# Revit family: ADSK_Балка_Двутавр_ГОСТ Р 57837-2017
name_source: partatom
category: Каркас несущий
units: mm (PartAtom-declared; Revit-internal decimal feet)

## family parameters
Всегда вертикально = Да
Всегда экспортировать в виде геометрии = Нет
Материал для поведения модели = Сталь
Общий = Нет
Округление длины несущего каркаса = 0 мм
Показывать семейство разрезанным на планах = Да
При загрузке вырезать с полостями = Нет
Условное обозначение = Из настроек проекта
Форма сечения = Двутавровая параллельная полка

## types (340) — shared parameters
ADSK_Версия Revit = v2019
ADSK_Версия семейства = 1.3
ADSK_Высота строки_Изображение = 8 мм.png
ADSK_Группа конструкций = 1
ADSK_Деталь наоборот = Нет
ADSK_Наименование профиля = Двутавры стальные горячекатаные с параллельными гранями полок
ADSK_Наименование_Текст1 = Двутавр
ADSK_НаименованиеСоставное_Префикс = <unrecoverable-encoding: 3 bytes ee9ca9>
ADSK_Обозначение = ГОСТ Р 57837-2017
ADSK_Тип элемента КМ = 2
ТВ = Двутавр_ГОСТ Р 57837-2017

## per-type parameters (varying)
- 10Б1: ADSK_Масса на единицу длины=8.10 кг/м; Ix=171.01 см4; Iy=15.92 см4; Sx=19.7 см³; Sy=4.6 см³; Wx=34.2 см³; Wy=5.8 см³; b=55.00 мм; h=100.00 мм; ix=40.70 мм; iy=12.42 мм; r=7.00 мм; s=4.10 мм; t=5.70 мм; Вертикальный центроид=50.00 мм; Высота=100.00 мм; Горизонтальный центроид=27.50 мм; Номинальный вес=8.10 килограмм-сила/м; Носок полки сопряжения=9.05 мм; Носок ребра жесткости сопряжения=12.70 мм; Площадь сечения=10.3 см²; Сопряжение ребра жесткости=7.00 мм; Толщина полки=5.70 мм; Толщина ребра жесткости=4.10 мм; Чистая высота ребра жесткости=88.60 мм; Ширина=55.00 мм
- 12Б1: ADSK_Масса на единицу длины=8.70 кг/м; Ix=257.36 см4; Iy=22.39 см4; Sx=24.9 см³; Sy=5.5 см³; Wx=43.8 см³; Wy=7.0 см³; b=64.00 мм; h=117.60 мм; ix=48.30 мм; iy=14.25 мм; r=7.00 мм; s=3.80 мм; t=5.10 мм; Вертикальный центроид=58.80 мм; Высота=117.60 мм; Горизонтальный центроид=32.00 мм; Номинальный вес=8.70 килограмм-сила/м; Носок полки сопряжения=8.90 мм; Носок ребра жесткости сопряжения=12.10 мм; Площадь сечения=11.0 см²; Сопряжение ребра жесткости=7.00 мм; Толщина полки=5.10 мм; Толщина ребра жесткости=3.80 мм; Чистая высота ребра жесткости=107.40 мм; Ширина=64.00 мм
- 12Б2: ADSK_Масса на единицу длины=10.40 кг/м; Ix=317.75 см4; Iy=27.67 см4; Sx=30.4 см³; Sy=6.8 см³; Wx=53.0 см³; Wy=8.7 см³; b=64.00 мм; h=120.00 мм; ix=49.04 мм; iy=14.47 мм; r=7.00 мм; s=4.40 мм; t=6.30 мм; Вертикальный центроид=60.00 мм; Высота=120.00 мм; Горизонтальный центроид=32.00 мм; Номинальный вес=10.40 килограмм-сила/м; Носок полки сопряжения=9.20 мм; Носок ребра жесткости сопряжения=13.30 мм; Площадь сечения=13.2 см²; Сопряжение ребра жесткости=7.00 мм; Толщина полки=6.30 мм; Толщина ребра жесткости=4.40 мм; Чистая высота ребра жесткости=107.40 мм; Ширина=64.00 мм
- 14Б1: ADSK_Масса на единицу длины=10.50 кг/м; Ix=434.86 см4; Iy=36.42 см4; Sx=35.8 см³; Sy=7.8 см³; Wx=63.3 см³; Wy=10.0 см³; b=73.00 мм; h=137.40 мм; ix=56.98 мм; iy=16.49 мм; r=7.00 мм; s=3.80 мм; t=5.60 мм; Вертикальный центроид=68.70 мм; Высота=137.40 мм; Горизонтальный центроид=36.50 мм; Номинальный вес=10.50 килограмм-сила/м; Носок полки сопряжения=8.90 мм; Носок ребра жесткости сопряжения=12.60 мм; Площадь сечения=13.4 см²; Сопряжение ребра жесткости=7.00 мм; Толщина полки=5.60 мм; Толщина ребра жесткости=3.80 мм; Чистая высота ребра жесткости=126.20 мм; Ширина=73.00 мм
- 14Б2: ADSK_Масса на единицу длины=12.90 кг/м; Ix=541.22 см4; Iy=44.92 см4; Sx=44.2 см³; Sy=9.6 см³; Wx=77.3 см³; Wy=12.3 см³; b=73.00 мм; h=140.00 мм; ix=57.40 мм; iy=16.54 мм; r=7.00 мм; s=4.70 мм; t=6.90 мм; Вертикальный центроид=70.00 мм; Высота=140.00 мм; Горизонтальный центроид=36.50 мм; Номинальный вес=12.90 килограмм-сила/м; Носок полки сопряжения=9.35 мм; Носок ребра жесткости сопряжения=13.90 мм; Площадь сечения=16.4 см²; Сопряжение ребра жесткости=7.00 мм; Толщина полки=6.90 мм; Толщина ребра жесткости=4.70 мм; Чистая высота ребра жесткости=126.20 мм; Ширина=73.00 мм
- 16Б1: ADSK_Масса на единицу длины=12.70 кг/м; Ix=689.28 см4; Iy=54.43 см4; Sx=49.6 см³; Sy=10.4 см³; Wx=87.8 см³; Wy=13.3 см³; b=82.00 мм; h=157.00 мм; ix=65.27 мм; iy=18.34 мм; r=9.00 мм; s=4.00 мм; t=5.90 мм; Вертикальный центроид=78.50 мм; Высота=157.00 мм; Горизонтальный центроид=41.00 мм; Номинальный вес=12.70 килограмм-сила/м; Носок полки сопряжения=11.00 мм; Носок ребра жесткости сопряжения=14.90 мм; Площадь сечения=16.2 см²; Сопряжение ребра жесткости=9.00 мм; Толщина полки=5.90 мм; Толщина ребра жесткости=4.00 мм; Чистая высота ребра жесткости=145.20 мм; Ширина=82.00 мм
- 16Б2: ADSK_Масса на единицу длины=15.80 кг/м; Ix=869.29 см4; Iy=68.31 см4; Sx=61.9 см³; Sy=13.1 см³; Wx=108.7 см³; Wy=16.7 см³; b=82.00 мм; h=160.00 мм; ix=65.78 мм; iy=18.44 мм; r=9.00 мм; s=5.00 мм; t=7.40 мм; Вертикальный центроид=80.00 мм; Высота=160.00 мм; Горизонтальный центроид=41.00 мм; Номинальный вес=15.80 килограмм-сила/м; Носок полки сопряжения=11.50 мм; Носок ребра жесткости сопряжения=16.40 мм; Площадь сечения=20.1 см²; Сопряжение ребра жесткости=9.00 мм; Толщина полки=7.40 мм; Толщина ребра жесткости=5.00 мм; Чистая высота ребра жесткости=145.20 мм; Ширина=82.00 мм
- 18Б1: ADSK_Масса на единицу длины=15.40 кг/м; Ix=1062.74 см4; Iy=81.89 см4; Sx=67.7 см³; Sy=14.0 см³; Wx=120.1 см³; Wy=18.0 см³; b=91.00 мм; h=177.00 мм; ix=73.68 мм; iy=20.45 мм; r=9.00 мм; s=4.30 мм; t=6.50 мм; Вертикальный центроид=88.50 мм; Высота=177.00 мм; Горизонтальный центроид=45.50 мм; Номинальный вес=15.40 килограмм-сила/м; Носок полки сопряжения=11.15 мм; Носок ребра жесткости сопряжения=15.50 мм; Площадь сечения=19.6 см²; Сопряжение ребра жесткости=9.00 мм; Толщина полки=6.50 мм; Толщина ребра жесткости=4.30 мм; Чистая высота ребра жесткости=164.00 мм; Ширина=91.00 мм
- 18Б2: ADSK_Масса на единицу длины=18.80 кг/м; Ix=1316.96 см4; Iy=100.85 см4; Sx=83.2 см³; Sy=17.3 см³; Wx=146.3 см³; Wy=22.2 см³; b=91.00 мм; h=180.00 мм; ix=74.16 мм; iy=20.52 мм; r=9.00 мм; s=5.30 мм; t=8.00 мм; Вертикальный центроид=90.00 мм; Высота=180.00 мм; Горизонтальный центроид=45.50 мм; Номинальный вес=18.80 килограмм-сила/м; Носок полки сопряжения=11.65 мм; Носок ребра жесткости сопряжения=17.00 мм; Площадь сечения=24.0 см²; Сопряжение ребра жесткости=9.00 мм; Толщина полки=8.00 мм; Толщина ребра жесткости=5.30 мм; Чистая высота ребра жесткости=164.00 мм; Ширина=91.00 мм
- 20Б1: ADSK_Масса на единицу длины=21.30 кг/м; Ix=1844.26 см4; Iy=133.91 см4; Sx=104.7 см³; Sy=21.0 см³; Wx=184.4 см³; Wy=26.8 см³; b=100.00 мм; h=200.00 мм; ix=82.41 мм; iy=22.21 мм; r=11.00 мм; s=5.50 мм; t=8.00 мм; Вертикальный центроид=100.00 мм; Высота=200.00 мм; Горизонтальный центроид=50.00 мм; Номинальный вес=21.30 килограмм-сила/м; Носок полки сопряжения=13.75 мм; Носок ребра жесткости сопряжения=19.00 мм; Площадь сечения=27.2 см²; Сопряжение ребра жесткости=11.00 мм; Толщина полки=8.00 мм; Толщина ребра жесткости=5.50 мм; Чистая высота ребра жесткости=184.00 мм; Ширина=100.00 мм
- 20Б2: ADSK_Масса на единицу длины=25.30 кг/м; Ix=2218.49 см4; Iy=163.93 см4; Sx=125.0 см³; Sy=25.5 см³; Wx=218.6 см³; Wy=32.5 см³; b=101.00 мм; h=203.00 мм; ix=83.02 мм; iy=22.57 мм; r=11.00 мм; s=6.50 мм; t=9.50 мм; Вертикальный центроид=101.50 мм; Высота=203.00 мм; Горизонтальный центроид=50.50 мм; Номинальный вес=25.30 килограмм-сила/м; Носок полки сопряжения=14.25 мм; Носок ребра жесткости сопряжения=20.50 мм; Площадь сечения=32.2 см²; Сопряжение ребра жесткости=11.00 мм; Толщина полки=9.50 мм; Толщина ребра жесткости=6.50 мм; Чистая высота ребра жесткости=184.00 мм; Ширина=101.00 мм
- 20Б3: ADSK_Масса на единицу длины=31.60 кг/м; Ix=2852.62 см4; Iy=213.50 см4; Sx=158.5 см³; Sy=33.0 см³; Wx=274.3 см³; Wy=41.9 см³; b=102.00 мм; h=208.00 мм; ix=84.20 мм; iy=23.03 мм; r=11.00 мм; s=8.00 мм; t=12.00 мм; Вертикальный центроид=104.00 мм; Высота=208.00 мм; Горизонтальный центроид=51.00 мм; Номинальный вес=31.60 килограмм-сила/м; Носок полки сопряжения=15.00 мм; Носок ребра жесткости сопряжения=23.00 мм; Площадь сечения=40.2 см²; Сопряжение ребра жесткости=11.00 мм; Толщина полки=12.00 мм; Толщина ребра жесткости=8.00 мм; Чистая высота ребра жесткости=184.00 мм; Ширина=102.00 мм
- 25Б1: ADSK_Масса на единицу длины=25.70 кг/м; Ix=3537.11 см4; Iy=254.85 см4; Sx=159.7 см³; Sy=31.8 см³; Wx=285.3 см³; Wy=41.1 см³; b=124.00 мм; h=248.00 мм; ix=104.04 мм; iy=27.93 мм; r=12.00 мм; s=5.00 мм; t=8.00 мм; Вертикальный центроид=124.00 мм; Высота=248.00 мм; Горизонтальный центроид=62.00 мм; Номинальный вес=25.70 килограмм-сила/м; Носок полки сопряжения=14.50 мм; Носок ребра жесткости сопряжения=20.00 мм; Площадь сечения=32.7 см²; Сопряжение ребра жесткости=12.00 мм; Толщина полки=8.00 мм; Толщина ребра жесткости=5.00 мм; Чистая высота ребра жесткости=232.00 мм; Ширина=124.00 мм
- 25Б2: ADSK_Масса на единицу длины=29.60 кг/м; Ix=4051.73 см4; Iy=293.85 см4; Sx=182.9 см³; Sy=36.6 см³; Wx=324.1 см³; Wy=47.0 см³; b=125.00 мм; h=250.00 мм; ix=103.73 мм; iy=27.93 мм; r=12.00 мм; s=6.00 мм; t=9.00 мм; Вертикальный центроид=125.00 мм; Высота=250.00 мм; Горизонтальный центроид=62.50 мм; Номинальный вес=29.60 килограмм-сила/м; Носок полки сопряжения=15.00 мм; Носок ребра жесткости сопряжения=21.00 мм; Площадь сечения=37.7 см²; Сопряжение ребра жесткости=12.00 мм; Толщина полки=9.00 мм; Толщина ребра жесткости=6.00 мм; Чистая высота ребра жесткости=232.00 мм; Ширина=125.00 мм
- 25Б3: ADSK_Масса на единицу длины=37.40 кг/м; Ix=5238.16 см4; Iy=384.79 см4; Sx=233.9 см³; Sy=47.7 см³; Wx=410.8 см³; Wy=61.1 см³; b=126.00 мм; h=255.00 мм; ix=104.88 мм; iy=28.43 мм; r=12.00 мм; s=7.50 мм; t=11.50 мм; Вертикальный центроид=127.50 мм; Высота=255.00 мм; Горизонтальный центроид=63.00 мм; Номинальный вес=37.40 килограмм-сила/м; Носок полки сопряжения=15.75 мм; Носок ребра жесткости сопряжения=23.50 мм; Площадь сечения=47.6 см²; Сопряжение ребра жесткости=12.00 мм; Толщина полки=11.50 мм; Толщина ребра жесткости=7.50 мм; Чистая высота ребра жесткости=232.00 мм; Ширина=126.00 мм
- 25Б4: ADSK_Масса на единицу длины=45.30 кг/м; Ix=6481.01 см4; Iy=480.07 см4; Sx=286.3 см³; Sy=59.2 см³; Wx=498.5 см³; Wy=75.6 см³; b=127.00 мм; h=260.00 мм; ix=106.00 мм; iy=28.85 мм; r=12.00 мм; s=9.00 мм; t=14.00 мм; Вертикальный центроид=130.00 мм; Высота=260.00 мм; Горизонтальный центроид=63.50 мм; Номинальный вес=45.30 килограмм-сила/м; Носок полки сопряжения=16.50 мм; Носок ребра жесткости сопряжения=26.00 мм; Площадь сечения=57.7 см²; Сопряжение ребра жесткости=12.00 мм; Толщина полки=14.00 мм; Толщина ребра жесткости=9.00 мм; Чистая высота ребра жесткости=232.00 мм; Ширина=127.00 мм
- 30Б1: ADSK_Масса на единицу длины=32.00 кг/м; Ix=6318.22 см4; Iy=442.00 см4; Sx=237.5 см³; Sy=45.9 см³; Wx=424.0 см³; Wy=59.3 см³; b=149.00 мм; h=298.00 мм; ix=124.44 мм; iy=32.91 мм; r=13.00 мм; s=5.50 мм; t=8.00 мм; Вертикальный центроид=149.00 мм; Высота=298.00 мм; Горизонтальный центроид=74.50 мм; Номинальный вес=32.00 килограмм-сила/м; Носок полки сопряжения=15.75 мм; Носок ребра жесткости сопряжения=21.00 мм; Площадь сечения=40.8 см²; Сопряжение ребра жесткости=13.00 мм; Толщина полки=8.00 мм; Толщина ребра жесткости=5.50 мм; Чистая высота ребра жесткости=282.00 мм; Ширина=149.00 мм
- 30Б2: ADSK_Масса на единицу длины=36.70 кг/м; Ix=7209.26 см4; Iy=507.53 см4; Sx=271.1 см³; Sy=52.6 см³; Wx=480.6 см³; Wy=67.7 см³; b=150.00 мм; h=300.00 мм; ix=124.14 мм; iy=32.94 мм; r=13.00 мм; s=6.50 мм; t=9.00 мм; Вертикальный центроид=150.00 мм; Высота=300.00 мм; Горизонтальный центроид=75.00 мм; Номинальный вес=36.70 килограмм-сила/м; Носок полки сопряжения=16.25 мм; Носок ребра жесткости сопряжения=22.00 мм; Площадь сечения=46.8 см²; Сопряжение ребра жесткости=13.00 мм; Толщина полки=9.00 мм; Толщина ребра жесткости=6.50 мм; Чистая высота ребра жесткости=282.00 мм; Ширина=150.00 мм
- 30Б3: ADSK_Масса на единицу длины=46.10 кг/м; Ix=9254.92 см4; Iy=661.88 см4; Sx=344.4 см³; Sy=68.3 см³; Wx=606.9 см³; Wy=87.7 см³; b=151.00 мм; h=305.00 мм; ix=125.52 мм; iy=33.57 мм; r=13.00 мм; s=8.00 мм; t=11.50 мм; Вертикальный центроид=152.50 мм; Высота=305.00 мм; Горизонтальный центроид=75.50 мм; Номинальный вес=46.10 килограмм-сила/м; Носок полки сопряжения=17.00 мм; Носок ребра жесткости сопряжения=24.50 мм; Площадь сечения=58.7 см²; Сопряжение ребра жесткости=13.00 мм; Толщина полки=11.50 мм; Толщина ребра жесткости=8.00 мм; Чистая высота ребра жесткости=282.00 мм; Ширина=151.00 мм
- 30Б4: ADSK_Масса на единицу длины=55.60 кг/м; Ix=11381.41 см4; Iy=822.37 см4; Sx=419.4 см³; Sy=84.6 см³; Wx=734.3 см³; Wy=108.2 см³; b=152.00 мм; h=310.00 мм; ix=126.79 мм; iy=34.08 мм; r=13.00 мм; s=9.50 мм; t=14.00 мм; Вертикальный центроид=155.00 мм; Высота=310.00 мм; Горизонтальный центроид=76.00 мм; Номинальный вес=55.60 килограмм-сила/м; Носок полки сопряжения=17.75 мм; Носок ребра жесткости сопряжения=27.00 мм; Площадь сечения=70.8 см²; Сопряжение ребра жесткости=13.00 мм; Толщина полки=14.00 мм; Толщина ребра жесткости=9.50 мм; Чистая высота ребра жесткости=282.00 мм; Ширина=152.00 мм
- 35Б1: ADSK_Масса на единицу длины=41.40 кг/м; Ix=11094.49 см4; Iy=791.54 см4; Sx=358.1 см³; Sy=70.1 см³; Wx=641.3 см³; Wy=91.0 см³; b=174.00 мм; h=346.00 мм; ix=145.12 мм; iy=38.76 мм; r=14.00 мм; s=6.00 мм; t=9.00 мм; Вертикальный центроид=173.00 мм; Высота=346.00 мм; Горизонтальный центроид=87.00 мм; Номинальный вес=41.40 килограмм-сила/м; Носок полки сопряжения=17.00 мм; Носок ребра жесткости сопряжения=23.00 мм; Площадь сечения=52.7 см²; Сопряжение ребра жесткости=14.00 мм; Толщина полки=9.00 мм; Толщина ребра жесткости=6.00 мм; Чистая высота ребра жесткости=328.00 мм; Ширина=174.00 мм
- 35Б2: ADSK_Масса на единицу длины=49.60 кг/м; Ix=13559.01 см4; Iy=984.34 см4; Sx=434.0 см³; Sy=86.8 см³; Wx=774.8 см³; Wy=112.5 см³; b=175.00 мм; h=350.00 мм; ix=146.54 мм; iy=39.48 мм; r=14.00 мм; s=7.00 мм; t=11.00 мм; Вертикальный центроид=175.00 мм; Высота=350.00 мм; Горизонтальный центроид=87.50 мм; Номинальный вес=49.60 килограмм-сила/м; Носок полки сопряжения=17.50 мм; Носок ребра жесткости сопряжения=25.00 мм; Площадь сечения=63.1 см²; Сопряжение ребра жесткости=14.00 мм; Толщина полки=11.00 мм; Толщина ребра жесткости=7.00 мм; Чистая высота ребра жесткости=328.00 мм; Ширина=175.00 мм
- 35Б3: ADSK_Масса на единицу длины=60.50 кг/м; Ix=16797.02 см4; Iy=1229.36 см4; Sx=533.5 см³; Sy=108.1 см³; Wx=946.3 см³; Wy=139.7 см³; b=176.00 мм; h=355.00 мм; ix=147.62 мм; iy=39.94 мм; r=14.00 мм; s=8.50 мм; t=13.50 мм; Вертикальный центроид=177.50 мм; Высота=355.00 мм; Горизонтальный центроид=88.00 мм; Номинальный вес=60.50 килограмм-сила/м; Носок полки сопряжения=18.25 мм; Носок ребра жесткости сопряжения=27.50 мм; Площадь сечения=77.1 см²; Сопряжение ребра жесткости=14.00 мм; Толщина полки=13.50 мм; Толщина ребра жесткости=8.50 мм; Чистая высота ребра жесткости=328.00 мм; Ширина=176.00 мм
- 35Б4: ADSK_Масса на единицу длины=72.90 кг/м; Ix=20719.71 см4; Iy=1528.90 см4; Sx=651.1 см³; Sy=134.0 см³; Wx=1147.9 см³; Wy=172.8 см³; b=177.00 мм; h=361.00 мм; ix=149.35 мм; iy=40.57 мм; r=14.00 мм; s=10.00 мм; t=16.50 мм; Вертикальный центроид=180.50 мм; Высота=361.00 мм; Горизонтальный центроид=88.50 мм; Номинальный вес=72.90 килограмм-сила/м; Носок полки сопряжения=19.00 мм; Носок ребра жесткости сопряжения=30.50 мм; Площадь сечения=92.9 см²; Сопряжение ребра жесткости=14.00 мм; Толщина полки=16.50 мм; Толщина ребра жесткости=10.00 мм; Чистая высота ребра жесткости=328.00 мм; Ширина=177.00 мм
- 40Б1: ADSK_Масса на единицу длины=56.60 кг/м; Ix=20018.83 см4; Iy=1447.14 см4; Sx=563.9 см³; Sy=112.0 см³; Wx=1011.1 см³; Wy=145.4 см³; b=199.00 мм; h=396.00 мм; ix=166.56 мм; iy=44.78 мм; r=16.00 мм; s=7.00 мм; t=11.00 мм; Вертикальный центроид=198.00 мм; Высота=396.00 мм; Горизонтальный центроид=99.50 мм; Номинальный вес=56.60 килограмм-сила/м; Носок полки сопряжения=19.50 мм; Носок ребра жесткости сопряжения=27.00 мм; Площадь сечения=72.2 см²; Сопряжение ребра жесткости=16.00 мм; Толщина полки=11.00 мм; Толщина ребра жесткости=7.00 мм; Чистая высота ребра жесткости=374.00 мм; Ширина=199.00 мм
- 40Б2: ADSK_Масса на единицу длины=66.00 кг/м; Ix=23704.43 см4; Iy=1736.39 см4; Sx=663.1 см³; Sy=133.8 см³; Wx=1185.2 см³; Wy=173.6 см³; b=200.00 мм; h=400.00 мм; ix=167.87 мм; iy=45.43 мм; r=16.00 мм; s=8.00 мм; t=13.00 мм; Вертикальный центроид=200.00 мм; Высота=400.00 мм; Горизонтальный центроид=100.00 мм; Номинальный вес=66.00 килограмм-сила/м; Носок полки сопряжения=20.00 мм; Носок ребра жесткости сопряжения=29.00 мм; Площадь сечения=84.1 см²; Сопряжение ребра жесткости=16.00 мм; Толщина полки=13.00 мм; Толщина ребра жесткости=8.00 мм; Чистая высота ребра жесткости=374.00 мм; Ширина=200.00 мм
- 40Б3: ADSK_Масса на единицу длины=80.10 кг/м; Ix=29352.45 см4; Iy=2169.89 см4; Sx=813.4 см³; Sy=166.7 см³; Wx=1445.9 см³; Wy=215.9 см³; b=201.00 мм; h=406.00 мм; ix=169.60 мм; iy=46.11 мм; r=16.00 мм; s=9.50 мм; t=16.00 мм; Вертикальный центроид=203.00 мм; Высота=406.00 мм; Горизонтальный центроид=100.50 мм; Номинальный вес=80.10 килограмм-сила/м; Носок полки сопряжения=20.75 мм; Носок ребра жесткости сопряжения=32.00 мм; Площадь сечения=102.1 см²; Сопряжение ребра жесткости=16.00 мм; Толщина полки=16.00 мм; Толщина ребра жесткости=9.50 мм; Чистая высота ребра жесткости=374.00 мм; Ширина=201.00 мм
- 40Б4: ADSK_Масса на единицу длины=94.30 кг/м; Ix=35196.83 см4; Iy=2616.25 см4; Sx=966.7 см³; Sy=200.5 см³; Wx=1708.6 см³; Wy=259.0 см³; b=202.00 мм; h=412.00 мм; ix=171.19 мм; iy=46.67 мм; r=16.00 мм; s=11.00 мм; t=19.00 мм; Вертикальный центроид=206.00 мм; Высота=412.00 мм; Горизонтальный центроид=101.00 мм; Номинальный вес=94.30 килограмм-сила/м; Носок полки сопряжения=21.50 мм; Носок ребра жесткости сопряжения=35.00 мм; Площадь сечения=120.1 см²; Сопряжение ребра жесткости=16.00 мм; Толщина полки=19.00 мм; Толщина ребра жесткости=11.00 мм; Чистая высота ребра жесткости=374.00 мм; Ширина=202.00 мм
- 45Б1: ADSK_Масса на единицу длины=66.20 кг/м; Ix=28697.35 см4; Iy=1580.03 см4; Sx=725.1 см³; Sy=123.3 см³; Wx=1286.9 см³; Wy=158.8 см³; b=199.00 мм; h=446.00 мм; ix=184.50 мм; iy=43.29 мм; r=18.00 мм; s=8.00 мм; t=12.00 мм; Вертикальный центроид=223.00 мм; Высота=446.00 мм; Горизонтальный центроид=99.50 мм; Номинальный вес=66.20 килограмм-сила/м; Носок полки сопряжения=22.00 мм; Носок ребра жесткости сопряжения=30.00 мм; Площадь сечения=84.3 см²; Сопряжение ребра жесткости=18.00 мм; Толщина полки=12.00 мм; Толщина ребра жесткости=8.00 мм; Чистая высота ребра жесткости=422.00 мм; Ширина=199.00 мм
- 45Б2: ADSK_Масса на единицу длины=76.00 кг/м; Ix=33450.76 см4; Iy=1871.57 см4; Sx=839.5 см³; Sy=145.5 см³; Wx=1486.7 см³; Wy=187.2 см³; b=200.00 мм; h=450.00 мм; ix=185.93 мм; iy=43.98 мм; r=18.00 мм; s=9.00 мм; t=14.00 мм; Вертикальный центроид=225.00 мм; Высота=450.00 мм; Горизонтальный центроид=100.00 мм; Номинальный вес=76.00 килограмм-сила/м; Носок полки сопряжения=22.50 мм; Носок ребра жесткости сопряжения=32.00 мм; Площадь сечения=96.8 см²; Сопряжение ребра жесткости=18.00 мм; Толщина полки=14.00 мм; Толщина ребра жесткости=9.00 мм; Чистая высота ребра жесткости=422.00 мм; Ширина=200.00 мм
- 45БЗ: ADSK_Масса на единицу длины=90.60 кг/м; Ix=40710.41 см4; Iy=2307.62 см4; Sx=1012.6 см³; Sy=178.8 см³; Wx=1785.5 см³; Wy=229.6 см³; b=201.00 мм; h=456.00 мм; ix=187.80 мм; iy=44.71 мм; r=18.00 мм; s=10.50 мм; t=17.00 мм; Вертикальный центроид=228.00 мм; Высота=456.00 мм; Горизонтальный центроид=100.50 мм; Номинальный вес=90.60 килограмм-сила/м; Носок полки сопряжения=23.25 мм; Носок ребра жесткости сопряжения=35.00 мм; Площадь сечения=115.4 см²; Сопряжение ребра жесткости=18.00 мм; Толщина полки=17.00 мм; Толщина ребра жесткости=10.50 мм; Чистая высота ребра жесткости=422.00 мм; Ширина=201.00 мм
- 45Б4: ADSK_Масса на единицу длины=105.40 кг/м; Ix=48197.42 см4; Iy=2756.66 см4; Sx=1188.8 см³; Sy=213.0 см³; Wx=2086.5 см³; Wy=272.9 см³; b=202.00 мм; h=462.00 мм; ix=189.50 мм; iy=45.32 мм; r=18.00 мм; s=12.00 мм; t=20.00 мм; Вертикальный центроид=231.00 мм; Высота=462.00 мм; Горизонтальный центроид=101.00 мм; Номинальный вес=105.40 килограмм-сила/м; Носок полки сопряжения=24.00 мм; Носок ребра жесткости сопряжения=38.00 мм; Площадь сечения=134.2 см²; Сопряжение ребра жесткости=18.00 мм; Толщина полки=20.00 мм; Толщина ребра жесткости=12.00 мм; Чистая высота ребра жесткости=422.00 мм; Ширина=202.00 мм
- 50Б1: ADSK_Масса на единицу длины=72.50 кг/м; Ix=36841.89 см4; Iy=1581.96 см4; Sx=853.5 см³; Sy=124.9 см³; Wx=1497.6 см³; Wy=159.0 см³; b=199.00 мм; h=492.00 мм; ix=199.70 мм; iy=41.38 мм; r=20.00 мм; s=8.80 мм; t=12.00 мм; Вертикальный центроид=246.00 мм; Высота=492.00 мм; Горизонтальный центроид=99.50 мм; Номинальный вес=72.50 килограмм-сила/м; Носок полки сопряжения=24.40 мм; Носок ребра жесткости сопряжения=32.00 мм; Площадь сечения=92.4 см²; Сопряжение ребра жесткости=20.00 мм; Толщина полки=12.00 мм; Толщина ребра жесткости=8.80 мм; Чистая высота ребра жесткости=468.00 мм; Ширина=199.00 мм
- 50Б2: ADSK_Масса на единицу длины=79.50 кг/м; Ix=41869.08 см4; Iy=1844.89 см4; Sx=957.2 см³; Sy=144.9 см³; Wx=1688.3 см³; Wy=185.4 см³; b=199.00 мм; h=496.00 мм; ix=203.33 мм; iy=42.68 мм; r=20.00 мм; s=9.00 мм; t=14.00 мм; Вертикальный центроид=248.00 мм; Высота=496.00 мм; Горизонтальный центроид=99.50 мм; Номинальный вес=79.50 килограмм-сила/м; Носок полки сопряжения=24.50 мм; Носок ребра жесткости сопряжения=34.00 мм; Площадь сечения=101.3 см²; Сопряжение ребра жесткости=20.00 мм; Толщина полки=14.00 мм; Толщина ребра жесткости=9.00 мм; Чистая высота ребра жесткости=468.00 мм; Ширина=199.00 мм
- 50Б3: ADSK_Масса на единицу длины=89.70 кг/м; Ix=47846.05 см4; Iy=2140.79 см4; Sx=1087.6 см³; Sy=167.5 см³; Wx=1913.8 см³; Wy=214.1 см³; b=200.00 мм; h=500.00 мм; ix=204.66 мм; iy=43.29 мм; r=20.00 мм; s=10.00 мм; t=16.00 мм; Вертикальный центроид=250.00 мм; Высота=500.00 мм; Горизонтальный центроид=100.00 мм; Номинальный вес=89.70 килограмм-сила/м; Носок полки сопряжения=25.00 мм; Носок ребра жесткости сопряжения=36.00 мм; Площадь сечения=114.2 см²; Сопряжение ребра жесткости=20.00 мм; Толщина полки=16.00 мм; Толщина ребра жесткости=10.00 мм; Чистая высота ребра жесткости=468.00 мм; Ширина=200.00 мм
- 50Б4: ADSK_Масса на единицу длины=109.90 кг/м; Ix=59953.57 см4; Iy=2717.85 см4; Sx=1348.8 см³; Sy=212.2 см³; Wx=2360.4 см³; Wy=270.4 см³; b=201.00 мм; h=508.00 мм; ix=206.94 мм; iy=44.06 мм; r=20.00 мм; s=12.00 мм; t=20.00 мм; Вертикальный центроид=254.00 мм; Высота=508.00 мм; Горизонтальный центроид=100.50 мм; Номинальный вес=109.90 килограмм-сила/м; Носок полки сопряжения=26.00 мм; Носок ребра жесткости сопряжения=40.00 мм; Площадь сечения=140.0 см²; Сопряжение ребра жесткости=20.00 мм; Толщина полки=20.00 мм; Толщина ребра жесткости=12.00 мм; Чистая высота ребра жесткости=468.00 мм; Ширина=201.00 мм
- 50Б5: ADSK_Масса на единицу длины=133.90 кг/м; Ix=73345.26 см4; Iy=3315.53 см4; Sx=1642.7 см³; Sy=260.0 см³; Wx=2842.8 см³; Wy=328.3 см³; b=202.00 мм; h=516.00 мм; ix=207.35 мм; iy=44.09 мм; r=20.00 мм; s=15.00 мм; t=24.00 мм; Вертикальный центроид=258.00 мм; Высота=516.00 мм; Горизонтальный центроид=101.00 мм; Номинальный вес=133.90 килограмм-сила/м; Носок полки сопряжения=27.50 мм; Носок ребра жесткости сопряжения=44.00 мм; Площадь сечения=170.6 см²; Сопряжение ребра жесткости=20.00 мм; Толщина полки=24.00 мм; Толщина ребра жесткости=15.00 мм; Чистая высота ребра жесткости=468.00 мм; Ширина=202.00 мм
- 55Б1: ADSK_Масса на единицу длины=89.00 кг/м; Ix=55677.42 см4; Iy=2405.54 см4; Sx=1164.9 см³; Sy=171.7 см³; Wx=2050.7 см³; Wy=218.7 см³; b=220.00 мм; h=543.00 мм; ix=221.62 мм; iy=46.06 мм; r=24.00 мм; s=9.50 мм; t=13.50 мм; Вертикальный центроид=271.50 мм; Высота=543.00 мм; Горизонтальный центроид=110.00 мм; Номинальный вес=89.00 килограмм-сила/м; Носок полки сопряжения=28.75 мм; Носок ребра жесткости сопряжения=37.50 мм; Площадь сечения=113.4 см²; Сопряжение ребра жесткости=24.00 мм; Толщина полки=13.50 мм; Толщина ребра жесткости=9.50 мм; Чистая высота ребра жесткости=516.00 мм; Ширина=220.00 мм
- 55Б2: ADSK_Масса на единицу длины=97.90 кг/м; Ix=62784.45 см4; Iy=2761.34 см4; Sx=1301.5 см³; Sy=196.6 см³; Wx=2295.6 см³; Wy=251.0 см³; b=220.00 мм; h=547.00 мм; ix=224.34 мм; iy=47.05 мм; r=24.00 мм; s=10.00 мм; t=15.50 мм; Вертикальный центроид=273.50 мм; Высота=547.00 мм; Горизонтальный центроид=110.00 мм; Номинальный вес=97.90 килограмм-сила/м; Носок полки сопряжения=29.00 мм; Носок ребра жесткости сопряжения=39.50 мм; Площадь сечения=124.7 см²; Сопряжение ребра жесткости=24.00 мм; Толщина полки=15.50 мм; Толщина ребра жесткости=10.00 мм; Чистая высота ребра жесткости=516.00 мм; Ширина=220.00 мм
- 55Б3: ADSK_Масса на единицу длины=116.70 кг/м; Ix=75321.22 см4; Iy=3342.92 см4; Sx=1554.5 см³; Sy=238.0 см³; Wx=2724.1 см³; Wy=302.5 см³; b=221.00 мм; h=553.00 мм; ix=225.11 мм; iy=47.42 мм; r=24.00 мм; s=12.00 мм; t=18.50 мм; Вертикальный центроид=276.50 мм; Высота=553.00 мм; Горизонтальный центроид=110.50 мм; Номинальный вес=116.70 килограмм-сила/м; Носок полки сопряжения=30.00 мм; Носок ребра жесткости сопряжения=42.50 мм; Площадь сечения=148.6 см²; Сопряжение ребра жесткости=24.00 мм; Толщина полки=18.50 мм; Толщина ребра жесткости=12.00 мм; Чистая высота ребра жесткости=516.00 мм; Ширина=221.00 мм
- 55Б4: ADSK_Масса на единицу длины=137.30 кг/м; Ix=89907.09 см4; Iy=4032.07 см4; Sx=1842.2 см³; Sy=286.8 см³; Wx=3211.0 см³; Wy=363.3 см³; b=222.00 мм; h=560.00 мм; ix=226.75 мм; iy=48.02 мм; r=24.00 мм; s=14.00 мм; t=22.00 мм; Вертикальный центроид=280.00 мм; Высота=560.00 мм; Горизонтальный центроид=111.00 мм; Номинальный вес=137.30 килограмм-сила/м; Носок полки сопряжения=31.00 мм; Носок ребра жесткости сопряжения=46.00 мм; Площадь сечения=174.9 см²; Сопряжение ребра жесткости=24.00 мм; Толщина полки=22.00 мм; Толщина ребра жесткости=14.00 мм; Чистая высота ребра жесткости=516.00 мм; Ширина=222.00 мм
- 60Б1: ADSK_Масса на единицу длины=94.60 кг/м; Ix=68715.90 см4; Iy=1979.66 см4; Sx=1325.4 см³; Sy=157.6 см³; Wx=2305.9 см³; Wy=199.0 см³; b=199.00 мм; h=596.00 мм; ix=238.85 мм; iy=40.54 мм; r=22.00 мм; s=10.00 мм; t=15.00 мм; Вертикальный центроид=298.00 мм; Высота=596.00 мм; Горизонтальный центроид=99.50 мм; Номинальный вес=94.60 килограмм-сила/м; Носок полки сопряжения=27.00 мм; Носок ребра жесткости сопряжения=37.00 мм; Площадь сечения=120.5 см²; Сопряжение ребра жесткости=22.00 мм; Толщина полки=15.00 мм; Толщина ребра жесткости=10.00 мм; Чистая высота ребра жесткости=566.00 мм; Ширина=199.00 мм
- 60Б2: ADSK_Масса на единицу длины=105.50 кг/м; Ix=77632.25 см4; Iy=2278.16 см4; Sx=1489.4 см³; Sy=180.7 см³; Wx=2587.7 см³; Wy=227.8 см³; b=200.00 мм; h=600.00 мм; ix=240.32 мм; iy=41.17 мм; r=22.00 мм; s=11.00 мм; t=17.00 мм; Вертикальный центроид=300.00 мм; Высота=600.00 мм; Горизонтальный центроид=100.00 мм; Номинальный вес=105.50 килограмм-сила/м; Носок полки сопряжения=27.50 мм; Носок ребра жесткости сопряжения=39.00 мм; Площадь сечения=134.4 см²; Сопряжение ребра жесткости=22.00 мм; Толщина полки=17.00 мм; Толщина ребра жесткости=11.00 мм; Чистая высота ребра жесткости=566.00 мм; Ширина=200.00 мм
- 60Б3: ADSK_Масса на единицу длины=118.80 кг/м; Ix=87472.10 см4; Iy=2586.62 см4; Sx=1675.4 см³; Sy=205.3 см³; Wx=2896.4 см³; Wy=257.4 см³; b=201.00 мм; h=604.00 мм; ix=240.46 мм; iy=41.35 мм; r=22.00 мм; s=12.50 мм; t=19.00 мм; Вертикальный центроид=302.00 мм; Высота=604.00 мм; Горизонтальный центроид=100.50 мм; Номинальный вес=118.80 килограмм-сила/м; Носок полки сопряжения=28.25 мм; Носок ребра жесткости сопряжения=41.00 мм; Площадь сечения=151.3 см²; Сопряжение ребра жесткости=22.00 мм; Толщина полки=19.00 мм; Толщина ребра жесткости=12.50 мм; Чистая высота ребра жесткости=566.00 мм; Ширина=201.00 мм
- 60Б4: ADSK_Масса на единицу длины=142.90 кг/м; Ix=106509.50 см4; Iy=3182.62 см4; Sx=2026.7 см³; Sy=253.1 см³; Wx=3480.7 см³; Wy=315.1 см³; b=202.00 мм; h=612.00 мм; ix=241.93 мм; iy=41.82 мм; r=22.00 мм; s=15.00 мм; t=23.00 мм; Вертикальный центроид=306.00 мм; Высота=612.00 мм; Горизонтальный центроид=101.00 мм; Номинальный вес=142.90 килограмм-сила/м; Носок полки сопряжения=29.50 мм; Носок ребра жесткости сопряжения=45.00 мм; Площадь сечения=182.0 см²; Сопряжение ребра жесткости=22.00 мм; Толщина полки=23.00 мм; Толщина ребра жесткости=15.00 мм; Чистая высота ребра жесткости=566.00 мм; Ширина=202.00 мм
- 70Б1: ADSK_Масса на единицу длины=129.30 кг/м; Ix=125922.20 см4; Iy=4557.35 см4; Sx=2094.8 см³; Sy=276.6 см³; Wx=3644.6 см³; Wy=350.6 см³; b=260.00 мм; h=691.00 мм; ix=276.47 мм; iy=52.60 мм; r=24.00 мм; s=12.00 мм; t=15.50 мм; Вертикальный центроид=345.50 мм; Высота=691.00 мм; Горизонтальный центроид=130.00 мм; Номинальный вес=129.30 килограмм-сила/м; Носок полки сопряжения=30.00 мм; Носок ребра жесткости сопряжения=39.50 мм; Площадь сечения=164.7 см²; Сопряжение ребра жесткости=24.00 мм; Толщина полки=15.50 мм; Толщина ребра жесткости=12.00 мм; Чистая высота ребра жесткости=660.00 мм; Ширина=260.00 мм
- 70Б2: ADSK_Масса на единицу длины=144.16 кг/м; Ix=145904.02 см4; Iy=5437.68 см4; Sx=2392.7 см³; Sy=328.4 см³; Wx=4186.6 см³; Wy=418.3 см³; b=260.00 мм; h=697.00 мм; ix=281.87 мм; iy=54.41 мм; r=24.00 мм; s=12.50 мм; t=18.50 мм; Вертикальный центроид=348.50 мм; Высота=697.00 мм; Горизонтальный центроид=130.00 мм; Номинальный вес=144.16 килограмм-сила/м; Носок полки сопряжения=30.25 мм; Носок ребра жесткости сопряжения=42.50 мм; Площадь сечения=183.6 см²; Сопряжение ребра жесткости=24.00 мм; Толщина полки=18.50 мм; Толщина ребра жесткости=12.50 мм; Чистая высота ребра жесткости=660.00 мм; Ширина=260.00 мм
- 70Б3: ADSK_Масса на единицу длины=165.10 кг/м; Ix=167085.05 см4; Iy=6248.49 см4; Sx=2736.1 см³; Sy=378.1 см³; Wx=4760.3 см³; Wy=478.8 см³; b=261.00 мм; h=702.00 мм; ix=281.89 мм; iy=54.51 мм; r=24.00 мм; s=14.50 мм; t=21.00 мм; Вертикальный центроид=351.00 мм; Высота=702.00 мм; Горизонтальный центроид=130.50 мм; Номинальный вес=165.10 килограмм-сила/м; Носок полки сопряжения=31.25 мм; Носок ребра жесткости сопряжения=45.00 мм; Площадь сечения=210.3 см²; Сопряжение ребра жесткости=24.00 мм; Толщина полки=21.00 мм; Толщина ребра жесткости=14.50 мм; Чистая высота ребра жесткости=660.00 мм; Ширина=261.00 мм
- 70Б4: ADSK_Масса на единицу длины=194.80 кг/м; Ix=199679.98 см4; Iy=7531.16 см4; Sx=3249.3 см³; Sy=456.3 см³; Wx=5624.8 см³; Wy=574.9 см³; b=262.00 мм; h=710.00 мм; ix=283.67 мм; iy=55.09 мм; r=24.00 мм; s=17.00 мм; t=25.00 мм; Вертикальный центроид=355.00 мм; Высота=710.00 мм; Горизонтальный центроид=131.00 мм; Номинальный вес=194.80 килограмм-сила/м; Носок полки сопряжения=32.50 мм; Носок ребра жесткости сопряжения=49.00 мм; Площадь сечения=248.1 см²; Сопряжение ребра жесткости=24.00 мм; Толщина полки=25.00 мм; Толщина ребра жесткости=17.00 мм; Чистая высота ребра жесткости=660.00 мм; Ширина=262.00 мм
- 20Ш0: ADSK_Масса на единицу длины=24.40 кг/м; Ix=2079.60 см4; Iy=386.62 см4; Sx=121.0 см³; Sy=39.8 см³; Wx=218.9 см³; Wy=51.9 см³; b=149.00 мм; h=190.00 мм; ix=81.76 мм; iy=35.25 мм; r=13.00 мм; s=5.00 мм; t=7.00 мм; Вертикальный центроид=95.00 мм; Высота=190.00 мм; Горизонтальный центроид=74.50 мм; Номинальный вес=24.40 килограмм-сила/м; Носок полки сопряжения=15.50 мм; Носок ребра жесткости сопряжения=20.00 мм; Площадь сечения=31.1 см²; Сопряжение ребра жесткости=13.00 мм; Толщина полки=7.00 мм; Толщина ребра жесткости=5.00 мм; Чистая высота ребра жесткости=176.00 мм; Ширина=149.00 мм
- 20Ш1: ADSK_Масса на единицу длины=30.60 кг/м; Ix=2689.74 см4; Iy=507.16 см4; Sx=154.3 см³; Sy=51.9 см³; Wx=277.3 см³; Wy=67.6 см³; b=150.00 мм; h=194.00 мм; ix=83.04 мм; iy=36.06 мм; r=13.00 мм; s=6.00 мм; t=9.00 мм; Вертикальный центроид=97.00 мм; Высота=194.00 мм; Горизонтальный центроид=75.00 мм; Номинальный вес=30.60 килограмм-сила/м; Носок полки сопряжения=16.00 мм; Носок ребра жесткости сопряжения=22.00 мм; Площадь сечения=39.0 см²; Сопряжение ребра жесткости=13.00 мм; Толщина полки=9.00 мм; Толщина ребра жесткости=6.00 мм; Чистая высота ребра жесткости=176.00 мм; Ширина=150.00 мм
- 20Ш2: ADSK_Масса на единицу длины=38.80 кг/м; Ix=3502.14 см4; Iy=661.25 см4; Sx=198.0 см³; Sy=67.3 см³; Wx=352.0 см³; Wy=87.6 см³; b=151.00 мм; h=199.00 мм; ix=84.21 мм; iy=36.59 мм; r=13.00 мм; s=7.50 мм; t=11.50 мм; Вертикальный центроид=99.50 мм; Высота=199.00 мм; Горизонтальный центроид=75.50 мм; Номинальный вес=38.80 килограмм-сила/м; Носок полки сопряжения=16.75 мм; Носок ребра жесткости сопряжения=24.50 мм; Площадь сечения=49.4 см²; Сопряжение ребра жесткости=13.00 мм; Толщина полки=11.50 мм; Толщина ребра жесткости=7.50 мм; Чистая высота ребра жесткости=176.00 мм; Ширина=151.00 мм
- 20Ш3: ADSK_Масса на единицу длины=47.00 кг/м; Ix=4362.01 см4; Iy=821.37 см4; Sx=243.2 см³; Sy=83.2 см³; Wx=427.7 см³; Wy=108.1 см³; b=152.00 мм; h=204.00 мм; ix=85.37 мм; iy=37.05 мм; r=13.00 мм; s=9.00 мм; t=14.00 мм; Вертикальный центроид=102.00 мм; Высота=204.00 мм; Горизонтальный центроид=76.00 мм; Номинальный вес=47.00 килограмм-сила/м; Носок полки сопряжения=17.50 мм; Носок ребра жесткости сопряжения=27.00 мм; Площадь сечения=59.9 см²; Сопряжение ребра жесткости=13.00 мм; Толщина полки=14.00 мм; Толщина ребра жесткости=9.00 мм; Чистая высота ребра жесткости=176.00 мм; Ширина=152.00 мм
- 20Ш4: ADSK_Масса на единицу длины=58.90 кг/м; Ix=5696.83 см4; Iy=1089.19 см4; Sx=311.2 см³; Sy=108.4 см³; Wx=540.0 см³; Wy=140.5 см³; b=155.00 мм; h=211.00 мм; ix=87.12 мм; iy=38.09 мм; r=13.00 мм; s=11.00 мм; t=17.50 мм; Вертикальный центроид=105.50 мм; Высота=211.00 мм; Горизонтальный центроид=77.50 мм; Номинальный вес=58.90 килограмм-сила/м; Носок полки сопряжения=18.50 мм; Носок ребра жесткости сопряжения=30.50 мм; Площадь сечения=75.1 см²; Сопряжение ребра жесткости=13.00 мм; Толщина полки=17.50 мм; Толщина ребра жесткости=11.00 мм; Чистая высота ребра жесткости=176.00 мм; Ширина=155.00 мм
- 20Ш5: ADSK_Масса на единицу длины=70.90 кг/м; Ix=7117.64 см4; Iy=1359.05 см4; Sx=381.3 см³; Sy=133.8 см³; Wx=653.0 см³; Wy=173.1 см³; b=157.00 мм; h=218.00 мм; ix=88.80 мм; iy=38.80 мм; r=13.00 мм; s=13.00 мм; t=21.00 мм; Вертикальный центроид=109.00 мм; Высота=218.00 мм; Горизонтальный центроид=78.50 мм; Номинальный вес=70.90 килограмм-сила/м; Носок полки сопряжения=19.50 мм; Носок ребра жесткости сопряжения=34.00 мм; Площадь сечения=90.3 см²; Сопряжение ребра жесткости=13.00 мм; Толщина полки=21.00 мм; Толщина ребра жесткости=13.00 мм; Чистая высота ребра жесткости=176.00 мм; Ширина=157.00 мм
- 20Ш6: ADSK_Масса на единицу длины=88.20 кг/м; Ix=9312.80 см4; Iy=1749.68 см4; Sx=485.7 см³; Sy=170.8 см³; Wx=816.9 см³; Wy=220.1 см³; b=159.00 мм; h=228.00 мм; ix=91.07 мм; iy=39.47 мм; r=13.00 мм; s=16.00 мм; t=26.00 мм; Вертикальный центроид=114.00 мм; Высота=228.00 мм; Горизонтальный центроид=79.50 мм; Номинальный вес=88.20 килограмм-сила/м; Носок полки сопряжения=21.00 мм; Носок ребра жесткости сопряжения=39.00 мм; Площадь сечения=112.3 см²; Сопряжение ребра жесткости=13.00 мм; Толщина полки=26.00 мм; Толщина ребра жесткости=16.00 мм; Чистая высота ребра жесткости=176.00 мм; Ширина=159.00 мм
- 25Ш0: ADSK_Масса на единицу длины=36.80 кг/м; Ix=4981.13 см4; Iy=791.75 см4; Sx=229.6 см³; Sy=69.8 см³; Wx=415.1 см³; Wy=91.0 см³; b=174.00 мм; h=240.00 мм; ix=103.13 мм; iy=41.11 мм; r=16.00 мм; s=6.00 мм; t=9.00 мм; Вертикальный центроид=120.00 мм; Высота=240.00 мм; Горизонтальный центроид=87.00 мм; Номинальный вес=36.80 килограмм-сила/м; Носок полки сопряжения=19.00 мм; Носок ребра жесткости сопряжения=25.00 мм; Площадь сечения=46.8 см²; Сопряжение ребра жесткости=16.00 мм; Толщина полки=9.00 мм; Толщина ребра жесткости=6.00 мм; Чистая высота ребра жесткости=222.00 мм; Ширина=174.00 мм
- 25Ш1: ADSK_Масса на единицу длины=44.20 кг/м; Ix=6121.23 см4; Iy=984.48 см4; Sx=279.2 см³; Sy=86.4 см³; Wx=501.7 см³; Wy=112.5 см³; b=175.00 мм; h=244.00 мм; ix=104.33 мм; iy=41.84 мм; r=16.00 мм; s=7.00 мм; t=11.00 мм; Вертикальный центроид=122.00 мм; Высота=244.00 мм; Горизонтальный центроид=87.50 мм; Номинальный вес=44.20 килограмм-сила/м; Носок полки сопряжения=19.50 мм; Носок ребра жесткости сопряжения=27.00 мм; Площадь сечения=56.2 см²; Сопряжение ребра жесткости=16.00 мм; Толщина полки=11.00 мм; Толщина ребра жесткости=7.00 мм; Чистая высота ребра жесткости=222.00 мм; Ширина=175.00 мм
- 25Ш2: ADSK_Масса на единицу длины=53.80 кг/м; Ix=7624.69 см4; Iy=1229.33 см4; Sx=343.9 см³; Sy=107.4 см³; Wx=612.4 см³; Wy=139.7 см³; b=176.00 мм; h=249.00 мм; ix=105.44 мм; iy=42.34 мм; r=16.00 мм; s=8.50 мм; t=13.50 мм; Вертикальный центроид=124.50 мм; Высота=249.00 мм; Горизонтальный центроид=88.00 мм; Номинальный вес=53.80 килограмм-сила/м; Носок полки сопряжения=20.25 мм; Носок ребра жесткости сопряжения=29.50 мм; Площадь сечения=68.6 см²; Сопряжение ребра жесткости=16.00 мм; Толщина полки=13.50 мм; Толщина ребра жесткости=8.50 мм; Чистая высота ребра жесткости=222.00 мм; Ширина=176.00 мм
- 25Ш3: ADSK_Масса на единицу длины=67.30 кг/м; Ix=9819.49 см4; Iy=1575.20 см4; Sx=436.1 см³; Sy=137.2 см³; Wx=767.2 см³; Wy=178.0 см³; b=177.00 мм; h=256.00 мм; ix=107.05 мм; iy=42.88 мм; r=16.00 мм; s=10.50 мм; t=17.00 мм; Вертикальный центроид=128.00 мм; Высота=256.00 мм; Горизонтальный центроид=88.50 мм; Номинальный вес=67.30 килограмм-сила/м; Носок полки сопряжения=21.25 мм; Носок ребра жесткости сопряжения=33.00 мм; Площадь сечения=85.7 см²; Сопряжение ребра жесткости=16.00 мм; Толщина полки=17.00 мм; Толщина ребра жесткости=10.50 мм; Чистая высота ребра жесткости=222.00 мм; Ширина=177.00 мм
- 25Ш4: ADSK_Масса на единицу длины=84.40 кг/м; Ix=12751.44 см4; Iy=2116.49 см4; Sx=556.3 см³; Sy=179.7 см³; Wx=966.0 см³; Wy=232.6 см³; b=182.00 мм; h=264.00 мм; ix=108.91 мм; iy=44.37 мм; r=16.00 мм; s=13.00 мм; t=21.00 мм; Вертикальный центроид=132.00 мм; Высота=264.00 мм; Горизонтальный центроид=91.00 мм; Номинальный вес=84.40 килограмм-сила/м; Носок полки сопряжения=22.50 мм; Носок ребра жесткости сопряжения=37.00 мм; Площадь сечения=107.5 см²; Сопряжение ребра жесткости=16.00 мм; Толщина полки=21.00 мм; Толщина ребра жесткости=13.00 мм; Чистая высота ребра жесткости=222.00 мм; Ширина=182.00 мм
- 25Ш5: ADSK_Масса на единицу длины=104.70 кг/м; Ix=16478.26 см4; Iy=2710.17 см4; Sx=703.6 см³; Sy=228.4 см³; Wx=1202.8 см³; Wy=294.6 см³; b=184.00 мм; h=274.00 мм; ix=111.14 мм; iy=45.07 мм; r=16.00 мм; s=16.00 мм; t=26.00 мм; Вертикальный центроид=137.00 мм; Высота=274.00 мм; Горизонтальный центроид=92.00 мм; Номинальный вес=104.70 килограмм-сила/м; Носок полки сопряжения=24.00 мм; Носок ребра жесткости сопряжения=42.00 мм; Площадь сечения=133.4 см²; Сопряжение ребра жесткости=16.00 мм; Толщина полки=26.00 мм; Толщина ребра жесткости=16.00 мм; Чистая высота ребра жесткости=222.00 мм; Ширина=184.00 мм
- 25Ш6: ADSK_Масса на единицу длины=128.30 кг/м; Ix=21287.68 см4; Iy=3448.57 см4; Sx=884.8 см³; Sy=288.2 см³; Wx=1488.7 см³; Wy=370.8 см³; b=186.00 мм; h=286.00 мм; ix=114.13 мм; iy=45.94 мм; r=16.00 мм; s=19.00 мм; t=32.00 мм; Вертикальный центроид=143.00 мм; Высота=286.00 мм; Горизонтальный центроид=93.00 мм; Номинальный вес=128.30 килограмм-сила/м; Носок полки сопряжения=25.50 мм; Носок ребра жесткости сопряжения=48.00 мм; Площадь сечения=163.4 см²; Сопряжение ребра жесткости=16.00 мм; Толщина полки=32.00 мм; Толщина ребра жесткости=19.00 мм; Чистая высота ребра жесткости=222.00 мм; Ширина=186.00 мм
- 30Ш0: ADSK_Масса на единицу длины=48.30 кг/м; Ix=9429.75 см4; Iy=1316.09 см4; Sx=360.6 см³; Sy=101.7 см³; Wx=650.3 см³; Wy=132.3 см³; b=199.00 мм; h=290.00 мм; ix=123.85 мм; iy=46.27 мм; r=18.00 мм; s=7.00 мм; t=10.00 мм; Вертикальный центроид=145.00 мм; Высота=290.00 мм; Горизонтальный центроид=99.50 мм; Номинальный вес=48.30 килограмм-сила/м; Носок полки сопряжения=21.50 мм; Носок ребра жесткости сопряжения=28.00 мм; Площадь сечения=61.5 см²; Сопряжение ребра жесткости=18.00 мм; Толщина полки=10.00 мм; Толщина ребра жесткости=7.00 мм; Чистая высота ребра жесткости=270.00 мм; Ширина=199.00 мм
- 30Ш1: ADSK_Масса на единицу длины=56.80 кг/м; Ix=11338.30 см4; Iy=1603.26 см4; Sx=429.5 см³; Sy=123.3 см³; Wx=771.3 см³; Wy=160.3 см³; b=200.00 мм; h=294.00 мм; ix=125.16 мм; iy=47.06 мм; r=18.00 мм; s=8.00 мм; t=12.00 мм; Вертикальный центроид=147.00 мм; Высота=294.00 мм; Горизонтальный центроид=100.00 мм; Номинальный вес=56.80 килограмм-сила/м; Носок полки сопряжения=22.00 мм; Носок ребра жесткости сопряжения=30.00 мм; Площадь сечения=72.4 см²; Сопряжение ребра жесткости=18.00 мм; Толщина полки=12.00 мм; Толщина ребра жесткости=8.00 мм; Чистая высота ребра жесткости=270.00 мм; Ширина=200.00 мм
- 30Ш2: ADSK_Масса на единицу длины=68.60 кг/м; Ix=14209.66 см4; Iy=2034.13 см4; Sx=529.9 см³; Sy=155.4 см³; Wx=947.3 см³; Wy=202.4 см³; b=201.00 мм; h=300.00 мм; ix=127.52 мм; iy=48.25 мм; r=18.00 мм; s=9.00 мм; t=15.00 мм; Вертикальный центроид=150.00 мм; Высота=300.00 мм; Горизонтальный центроид=100.50 мм; Номинальный вес=68.60 килограмм-сила/м; Носок полки сопряжения=22.50 мм; Носок ребра жесткости сопряжения=33.00 мм; Площадь сечения=87.4 см²; Сопряжение ребра жесткости=18.00 мм; Толщина полки=15.00 мм; Толщина ребра жесткости=9.00 мм; Чистая высота ребра жесткости=270.00 мм; Ширина=201.00 мм
- 30Ш3: ADSK_Масса на единицу длины=82.90 кг/м; Ix=17455.33 см4; Iy=2515.46 см4; Sx=644.6 см³; Sy=190.9 см³; Wx=1140.9 см³; Wy=247.8 см³; b=203.00 мм; h=306.00 мм; ix=128.59 мм; iy=48.82 мм; r=18.00 мм; s=11.00 мм; t=18.00 мм; Вертикальный центроид=153.00 мм; Высота=306.00 мм; Горизонтальный центроид=101.50 мм; Номинальный вес=82.90 килограмм-сила/м; Носок полки сопряжения=23.50 мм; Носок ребра жесткости сопряжения=36.00 мм; Площадь сечения=105.6 см²; Сопряжение ребра жесткости=18.00 мм; Толщина полки=18.00 мм; Толщина ребра жесткости=11.00 мм; Чистая высота ребра жесткости=270.00 мм; Ширина=203.00 мм
- 30Ш4: ADSK_Масса на единицу длины=100.90 кг/м; Ix=21967.16 см4; Iy=3213.67 см4; Sx=798.4 см³; Sy=240.6 см³; Wx=1399.2 см³; Wy=312.0 см³; b=206.00 мм; h=314.00 мм; ix=130.74 мм; iy=50.00 мм; r=18.00 мм; s=13.00 мм; t=22.00 мм; Вертикальный центроид=157.00 мм; Высота=314.00 мм; Горизонтальный центроид=103.00 мм; Номинальный вес=100.90 килограмм-сила/м; Носок полки сопряжения=24.50 мм; Носок ребра жесткости сопряжения=40.00 мм; Площадь сечения=128.5 см²; Сопряжение ребра жесткости=18.00 мм; Толщина полки=22.00 мм; Толщина ребра жесткости=13.00 мм; Чистая высота ребра жесткости=270.00 мм; Ширина=206.00 мм
- 30Ш5: ADSK_Масса на единицу длины=127.50 кг/м; Ix=29037.68 см4; Iy=4213.04 см4; Sx=1031.8 см³; Sy=313.2 см³; Wx=1781.5 см³; Wy=405.1 см³; b=208.00 мм; h=326.00 мм; ix=133.69 мм; iy=50.92 мм; r=18.00 мм; s=16.00 мм; t=28.00 мм; Вертикальный центроид=163.00 мм; Высота=326.00 мм; Горизонтальный центроид=104.00 мм; Номинальный вес=127.50 килограмм-сила/м; Носок полки сопряжения=26.00 мм; Носок ребра жесткости сопряжения=46.00 мм; Площадь сечения=162.5 см²; Сопряжение ребра жесткости=18.00 мм; Толщина полки=28.00 мм; Толщина ребра жесткости=16.00 мм; Чистая высота ребра жесткости=270.00 мм; Ширина=208.00 мм
- 30Ш6: ADSK_Масса на единицу длины=163.30 кг/м; Ix=39315.66 см4; Iy=5580.38 см4; Sx=1357.1 см³; Sy=412.4 см³; Wx=2299.2 см³; Wy=531.5 см³; b=210.00 мм; h=342.00 мм; ix=137.49 мм; iy=51.80 мм; r=18.00 мм; s=20.00 мм; t=95.00 мм; Вертикальный центроид=171.00 мм; Высота=342.00 мм; Горизонтальный центроид=105.00 мм; Номинальный вес=163.30 килограмм-сила/м; Носок полки сопряжения=28.00 мм; Носок ребра жесткости сопряжения=113.00 мм; Площадь сечения=208.0 см²; Сопряжение ребра жесткости=18.00 мм; Толщина полки=95.00 мм; Толщина ребра жесткости=20.00 мм; Чистая высота ребра жесткости=152.00 мм; Ширина=210.00 мм
- 35Ш1: ADSK_Масса на единицу длины=65.30 кг/м; Ix=17107.05 см4; Iy=2834.62 см4; Sx=565.7 см³; Sy=174.5 см³; Wx=1024.4 см³; Wy=227.7 см³; b=249.00 мм; h=334.00 мм; ix=143.42 мм; iy=58.38 мм; r=20.00 мм; s=8.00 мм; t=11.00 мм; Вертикальный центроид=167.00 мм; Высота=334.00 мм; Горизонтальный центроид=124.50 мм; Номинальный вес=65.30 килограмм-сила/м; Носок полки сопряжения=24.00 мм; Носок ребра жесткости сопряжения=31.00 мм; Площадь сечения=83.2 см²; Сопряжение ребра жесткости=20.00 мм; Толщина полки=11.00 мм; Толщина ребра жесткости=8.00 мм; Чистая высота ребра жесткости=312.00 мм; Ширина=249.00 мм
- 35Ш2: ADSK_Масса на единицу длины=79.70 кг/м; Ix=21676.50 см4; Iy=3650.97 см4; Sx=706.0 см³; Sy=223.5 см³; Wx=1275.1 см³; Wy=292.1 см³; b=250.00 мм; h=340.00 мм; ix=146.13 мм; iy=59.97 мм; r=20.00 мм; s=9.00 мм; t=14.00 мм; Вертикальный центроид=170.00 мм; Высота=340.00 мм; Горизонтальный центроид=125.00 мм; Номинальный вес=79.70 килограмм-сила/м; Носок полки сопряжения=24.50 мм; Носок ребра жесткости сопряжения=34.00 мм; Площадь сечения=101.5 см²; Сопряжение ребра жесткости=20.00 мм; Толщина полки=14.00 мм; Толщина ребра жесткости=9.00 мм; Чистая высота ребра жесткости=312.00 мм; Ширина=250.00 мм
- 35Ш3: ADSK_Масса на единицу длины=98.90 кг/м; Ix=27535.21 см4; Iy=4674.90 см4; Sx=886.4 см³; Sy=284.3 см³; Wx=1587.0 см³; Wy=371.0 см³; b=252.00 мм; h=347.00 мм; ix=147.86 мм; iy=60.92 мм; r=20.00 мм; s=11.00 мм; t=17.50 мм; Вертикальный центроид=173.50 мм; Высота=347.00 мм; Горизонтальный центроид=126.00 мм; Номинальный вес=98.90 килограмм-сила/м; Носок полки сопряжения=25.50 мм; Носок ребра жесткости сопряжения=37.50 мм; Площадь сечения=126.0 см²; Сопряжение ребра жесткости=20.00 мм; Толщина полки=17.50 мм; Толщина ребра жесткости=11.00 мм; Чистая высота ребра жесткости=312.00 мм; Ширина=252.00 мм
- 35Ш4: ADSK_Масса на единицу длины=118.30 кг/м; Ix=33692.45 см4; Iy=5745.80 см4; Sx=1072.3 см³; Sy=347.2 см³; Wx=1903.5 см³; Wy=452.4 см³; b=254.00 мм; h=354.00 мм; ix=149.54 мм; iy=61.75 мм; r=20.00 мм; s=13.00 мм; t=21.00 мм; Вертикальный центроид=177.00 мм; Высота=354.00 мм; Горизонтальный центроид=127.00 мм; Номинальный вес=118.30 килограмм-сила/м; Носок полки сопряжения=26.50 мм; Носок ребра жесткости сопряжения=41.00 мм; Площадь сечения=150.7 см²; Сопряжение ребра жесткости=20.00 мм; Толщина полки=21.00 мм; Толщина ребра жесткости=13.00 мм; Чистая высота ребра жесткости=312.00 мм; Ширина=254.00 мм
- 35Ш5: ADSK_Масса на единицу длины=147.20 кг/м; Ix=43231.44 см4; Iy=7458.32 см4; Sx=1354.4 см³; Sy=444.8 см³; Wx=2375.4 см³; Wy=578.2 см³; b=258.00 мм; h=364.00 мм; ix=151.84 мм; iy=63.07 мм; r=20.00 мм; s=16.00 мм; t=26.00 мм; Вертикальный центроид=182.00 мм; Высота=364.00 мм; Горизонтальный центроид=129.00 мм; Номинальный вес=147.20 килограмм-сила/м; Носок полки сопряжения=28.00 мм; Носок ребра жесткости сопряжения=46.00 мм; Площадь сечения=187.5 см²; Сопряжение ребра жесткости=20.00 мм; Толщина полки=26.00 мм; Толщина ребра жесткости=16.00 мм; Чистая высота ребра жесткости=312.00 мм; Ширина=258.00 мм
- 35Ш6: ADSK_Масса на единицу длины=179.90 кг/м; Ix=54967.48 см4; Iy=9398.88 см4; Sx=1688.3 см³; Sy=557.3 см³; Wx=2923.8 см³; Wy=723.0 см³; b=260.00 мм; h=376.00 мм; ix=154.89 мм; iy=64.05 мм; r=20.00 мм; s=19.00 мм; t=32.00 мм; Вертикальный центроид=188.00 мм; Высота=376.00 мм; Горизонтальный центроид=130.00 мм; Номинальный вес=179.90 килограмм-сила/м; Носок полки сопряжения=29.50 мм; Носок ребра жесткости сопряжения=52.00 мм; Площадь сечения=229.1 см²; Сопряжение ребра жесткости=20.00 мм; Толщина полки=32.00 мм; Толщина ребра жесткости=19.00 мм; Чистая высота ребра жесткости=312.00 мм; Ширина=260.00 мм
- 35Ш7: ADSK_Масса на единицу длины=223.60 кг/м; Ix=71815.25 см4; Iy=12030.69 см4; Sx=2150.4 см³; Sy=709.8 см³; Wx=3664.0 см³; Wy=918.4 см³; b=262.00 мм; h=392.00 мм; ix=158.80 мм; iy=65.00 мм; r=20.00 мм; s=23.00 мм; t=40.00 мм; Вертикальный центроид=196.00 мм; Высота=392.00 мм; Горизонтальный центроид=131.00 мм; Номинальный вес=223.60 килограмм-сила/м; Носок полки сопряжения=31.50 мм; Носок ребра жесткости сопряжения=60.00 мм; Площадь сечения=284.8 см²; Сопряжение ребра жесткости=20.00 мм; Толщина полки=40.00 мм; Толщина ребра жесткости=23.00 мм; Чистая высота ребра жесткости=312.00 мм; Ширина=262.00 мм
- 40Ш1: ADSK_Масса на единицу длины=88.60 кг/м; Ix=30554.32 см4; Iy=5576.08 см4; Sx=880.7 см³; Sy=285.4 см³; Wx=1595.5 см³; Wy=373.0 см³; b=299.00 мм; h=383.00 мм; ix=164.50 мм; iy=70.27 мм; r=22.00 мм; s=9.50 мм; t=12.50 мм; Вертикальный центроид=191.50 мм; Высота=383.00 мм; Горизонтальный центроид=149.50 мм; Номинальный вес=88.60 килограмм-сила/м; Носок полки сопряжения=26.75 мм; Носок ребра жесткости сопряжения=34.50 мм; Площадь сечения=112.9 см²; Сопряжение ребра жесткости=22.00 мм; Толщина полки=12.50 мм; Толщина ребра жесткости=9.50 мм; Чистая высота ребра жесткости=358.00 мм; Ширина=299.00 мм
- 40Ш2: ADSK_Масса на единицу длины=106.70 кг/м; Ix=38674.10 см4; Iy=7207.77 см4; Sx=1094.0 см³; Sy=366.5 см³; Wx=1983.3 см³; Wy=480.5 см³; b=300.00 мм; h=390.00 мм; ix=168.66 мм; iy=72.81 мм; r=22.00 мм; s=10.00 мм; t=16.00 мм; Вертикальный центроид=195.00 мм; Высота=390.00 мм; Горизонтальный центроид=150.00 мм; Номинальный вес=106.70 килограмм-сила/м; Носок полки сопряжения=27.00 мм; Носок ребра жесткости сопряжения=38.00 мм; Площадь сечения=136.0 см²; Сопряжение ребра жесткости=22.00 мм; Толщина полки=16.00 мм; Толщина ребра жесткости=10.00 мм; Чистая высота ребра жесткости=358.00 мм; Ширина=300.00 мм
- 40Ш3: ADSK_Масса на единицу длины=129.40 кг/м; Ix=47846.38 см4; Iy=8962.48 см4; Sx=1340.0 см³; Sy=453.3 см³; Wx=2410.4 см³; Wy=593.5 см³; b=302.00 мм; h=397.00 мм; ix=170.34 мм; iy=73.72 мм; r=22.00 мм; s=12.00 мм; t=19.50 мм; Вертикальный центроид=198.50 мм; Высота=397.00 мм; Горизонтальный центроид=151.00 мм; Номинальный вес=129.40 килограмм-сила/м; Носок полки сопряжения=28.00 мм; Носок ребра жесткости сопряжения=41.50 мм; Площадь сечения=164.9 см²; Сопряжение ребра жесткости=22.00 мм; Толщина полки=19.50 мм; Толщина ребра жесткости=12.00 мм; Чистая высота ребра жесткости=358.00 мм; Ширина=302.00 мм
- 40Ш4: ADSK_Масса на единицу длины=158.60 кг/м; Ix=60107.10 см4; Iy=11253.74 см4; Sx=1662.0 см³; Sy=566.4 см³; Wx=2960.9 см³; Wy=740.4 см³; b=304.00 мм; h=406.00 мм; ix=172.51 мм; iy=74.64 мм; r=22.00 мм; s=14.50 мм; t=24.00 мм; Вертикальный центроид=203.00 мм; Высота=406.00 мм; Горизонтальный центроид=152.00 мм; Номинальный вес=158.60 килограмм-сила/м; Носок полки сопряжения=29.25 мм; Носок ребра жесткости сопряжения=46.00 мм; Площадь сечения=202.0 см²; Сопряжение ребра жесткости=22.00 мм; Толщина полки=24.00 мм; Толщина ребра жесткости=14.50 мм; Чистая высота ребра жесткости=358.00 мм; Ширина=304.00 мм
- 40Ш5: ADSK_Масса на единицу длины=198.00 кг/м; Ix=77867.25 см4; Iy=14776.27 см4; Sx=2114.9 см³; Sy=732.7 см³; Wx=3725.7 см³; Wy=956.4 см³; b=309.00 мм; h=418.00 мм; ix=175.71 мм; iy=76.54 мм; r=22.00 мм; s=17.50 мм; t=30.00 мм; Вертикальный центроид=209.00 мм; Высота=418.00 мм; Горизонтальный центроид=154.50 мм; Номинальный вес=198.00 килограмм-сила/м; Носок полки сопряжения=30.75 мм; Носок ребра жесткости сопряжения=52.00 мм; Площадь сечения=252.2 см²; Сопряжение ребра жесткости=22.00 мм; Толщина полки=30.00 мм; Толщина ребра жесткости=17.50 мм; Чистая высота ребра жесткости=358.00 мм; Ширина=309.00 мм
- 40Ш6: ADSK_Масса на единицу длины=238.10 кг/м; Ix=96432.24 см4; Iy=18086.35 см4; Sx=2578.2 см³; Sy=893.4 см³; Wx=4485.2 см³; Wy=1163.1 см³; b=311.00 мм; h=430.00 мм; ix=178.32 мм; iy=77.23 мм; r=22.00 мм; s=21.00 мм; t=36.00 мм; Вертикальный центроид=215.00 мм; Высота=430.00 мм; Горизонтальный центроид=155.50 мм; Номинальный вес=238.10 килограмм-сила/м; Носок полки сопряжения=32.50 мм; Носок ребра жесткости сопряжения=58.00 мм; Площадь сечения=303.3 см²; Сопряжение ребра жесткости=22.00 мм; Толщина полки=36.00 мм; Толщина ребра жесткости=21.00 мм; Чистая высота ребра жесткости=358.00 мм; Ширина=311.00 мм
- 40Ш7: ADSK_Масса на единицу длины=289.70 кг/м; Ix=122543.61 см4; Iy=22547.07 см4; Sx=3204.9 см³; Sy=1109.3 см³; Wx=5495.2 см³; Wy=1440.7 см³; b=313.00 мм; h=446.00 мм; ix=182.21 мм; iy=78.16 мм; r=22.00 мм; s=25.00 мм; t=44.00 мм; Вертикальный центроид=223.00 мм; Высота=446.00 мм; Горизонтальный центроид=156.50 мм; Номинальный вес=289.70 килограмм-сила/м; Носок полки сопряжения=34.50 мм; Носок ребра жесткости сопряжения=66.00 мм; Площадь сечения=369.1 см²; Сопряжение ребра жесткости=22.00 мм; Толщина полки=44.00 мм; Толщина ребра жесткости=25.00 мм; Чистая высота ребра жесткости=358.00 мм; Ширина=313.00 мм
- 45Ш0: ADSK_Масса на единицу длины=106.00 кг/м; Ix=46794.17 см4; Iy=6692.40 см4; Sx=1192.2 см³; Sy=342.9 см³; Wx=2156.4 см³; Wy=447.7 см³; b=299.00 мм; h=434.00 мм; ix=186.15 мм; iy=70.40 мм; r=24.00 мм; s=10.00 мм; t=15.00 мм; Вертикальный центроид=217.00 мм; Высота=434.00 мм; Горизонтальный центроид=149.50 мм; Номинальный вес=106.00 килограмм-сила/м; Носок полки сопряжения=29.00 мм; Носок ребра жесткости сопряжения=39.00 мм; Площадь сечения=135.0 см²; Сопряжение ребра жесткости=24.00 мм; Толщина полки=15.00 мм; Толщина ребра жесткости=10.00 мм; Чистая высота ребра жесткости=404.00 мм; Ширина=299.00 мм
- 45Ш1: ADSK_Масса на единицу длины=123.60 кг/м; Ix=56069.13 см4; Iy=8111.31 см4; Sx=1412.4 см³; Sy=413.8 см³; Wx=2548.6 см³; Wy=540.8 см³; b=300.00 мм; h=440.00 мм; ix=188.75 мм; iy=71.79 мм; r=24.00 мм; s=11.00 мм; t=18.00 мм; Вертикальный центроид=220.00 мм; Высота=440.00 мм; Горизонтальный центроид=150.00 мм; Номинальный вес=123.60 килограмм-сила/м; Носок полки сопряжения=29.50 мм; Носок ребра жесткости сопряжения=42.00 мм; Площадь сечения=157.4 см²; Сопряжение ребра жесткости=24.00 мм; Толщина полки=18.00 мм; Толщина ребра жесткости=11.00 мм; Чистая высота ребра жесткости=404.00 мм; Ширина=300.00 мм
- 45Ш2: ADSK_Масса на единицу длины=144.70 кг/м; Ix=66379.08 см4; Iy=9655.62 см4; Sx=1661.5 см³; Sy=490.3 см³; Wx=2976.6 см³; Wy=639.4 см³; b=302.00 мм; h=446.00 мм; ix=189.78 мм; iy=72.38 мм; r=24.00 мм; s=13.00 мм; t=21.00 мм; Вертикальный центроид=223.00 мм; Высота=446.00 мм; Горизонтальный центроид=151.00 мм; Номинальный вес=144.70 килограмм-сила/м; Носок полки сопряжения=30.50 мм; Носок ребра жесткости сопряжения=45.00 мм; Площадь сечения=184.3 см²; Сопряжение ребра жесткости=24.00 мм; Толщина полки=21.00 мм; Толщина ребра жесткости=13.00 мм; Чистая высота ребра жесткости=404.00 мм; Ширина=302.00 мм
- 45Ш3: ADSK_Масса на единицу длины=166.00 кг/м; Ix=77050.83 см4; Iy=11258.33 см4; Sx=1916.0 см³; Sy=569.0 см³; Wx=3409.3 см³; Wy=740.7 см³; b=304.00 мм; h=452.00 мм; ix=190.88 мм; iy=72.97 мм; r=24.00 мм; s=15.00 мм; t=24.00 мм; Вертикальный центроид=226.00 мм; Высота=452.00 мм; Горизонтальный центроид=152.00 мм; Номинальный вес=166.00 килограмм-сила/м; Носок полки сопряжения=31.50 мм; Носок ребра жесткости сопряжения=48.00 мм; Площадь сечения=211.5 см²; Сопряжение ребра жесткости=24.00 мм; Толщина полки=24.00 мм; Толщина ребра жесткости=15.00 мм; Чистая высота ребра жесткости=404.00 мм; Ширина=304.00 мм
- 45Ш4: ADSK_Масса на единицу длины=206.00 кг/м; Ix=98962.82 см4; Iy=14639.89 см4; Sx=2420.9 см³; Sy=731.4 см³; Wx=4265.6 см³; Wy=950.6 см³; b=308.00 мм; h=464.00 мм; ix=194.18 мм; iy=74.69 мм; r=24.00 мм; s=18.00 мм; t=30.00 мм; Вертикальный центроид=232.00 мм; Высота=464.00 мм; Горизонтальный центроид=154.00 мм; Номинальный вес=206.00 килограмм-сила/м; Носок полки сопряжения=33.00 мм; Носок ребра жесткости сопряжения=54.00 мм; Площадь сечения=262.5 см²; Сопряжение ребра жесткости=24.00 мм; Толщина полки=30.00 мм; Толщина ребра жесткости=18.00 мм; Чистая высота ребра жесткости=404.00 мм; Ширина=308.00 мм
- 45Ш5: ADSK_Масса на единицу длины=245.70 кг/м; Ix=121722.09 см4; Iy=17919.22 см4; Sx=2932.3 см³; Sy=891.1 см³; Wx=5114.4 см³; Wy=1156.1 см³; b=310.00 мм; h=476.00 мм; ix=197.21 мм; iy=75.67 мм; r=24.00 мм; s=21.00 мм; t=36.00 мм; Вертикальный центроид=238.00 мм; Высота=476.00 мм; Горизонтальный центроид=155.00 мм; Номинальный вес=245.70 килограмм-сила/м; Носок полки сопряжения=34.50 мм; Носок ребра жесткости сопряжения=60.00 мм; Площадь сечения=313.0 см²; Сопряжение ребра жесткости=24.00 мм; Толщина полки=36.00 мм; Толщина ребра жесткости=21.00 мм; Чистая высота ребра жесткости=404.00 мм; Ширина=310.00 мм
- 45Ш6: ADSK_Масса на единицу длины=298.70 кг/м; Ix=153856.39 см4; Iy=22341.69 см4; Sx=3633.7 см³; Sy=1106.8 см³; Wx=6254.3 см³; Wy=1432.2 см³; b=312.00 мм; h=492.00 мм; ix=201.08 мм; iy=76.63 мм; r=24.00 мм; s=25.00 мм; t=44.00 мм; Вертикальный центроид=246.00 мм; Высота=492.00 мм; Горизонтальный центроид=156.00 мм; Номинальный вес=298.70 килограмм-сила/м; Носок полки сопряжения=36.50 мм; Носок ребра жесткости сопряжения=68.00 мм; Площадь сечения=380.5 см²; Сопряжение ребра жесткости=24.00 мм; Толщина полки=44.00 мм; Толщина ребра жесткости=25.00 мм; Чистая высота ребра жесткости=404.00 мм; Ширина=312.00 мм
- 50Ш1: ADSK_Масса на единицу длины=114.20 кг/м; Ix=60366.76 см4; Iy=6763.81 см4; Sx=1395.6 см³; Sy=347.6 см³; Wx=2504.8 см³; Wy=450.9 см³; b=300.00 мм; h=482.00 мм; ix=203.67 мм; iy=68.18 мм; r=26.00 мм; s=11.00 мм; t=15.00 мм; Вертикальный центроид=241.00 мм; Высота=482.00 мм; Горизонтальный центроид=150.00 мм; Номинальный вес=114.20 килограмм-сила/м; Носок полки сопряжения=31.50 мм; Носок ребра жесткости сопряжения=41.00 мм; Площадь сечения=145.5 см²; Сопряжение ребра жесткости=26.00 мм; Толщина полки=15.00 мм; Толщина ребра жесткости=11.00 мм; Чистая высота ребра жесткости=452.00 мм; Ширина=300.00 мм
- 50Ш2: ADSK_Масса на единицу длины=138.40 кг/м; Ix=71863.01 см4; Iy=7897.76 см4; Sx=1666.6 см³; Sy=409.4 см³; Wx=2951.3 см³; Wy=526.5 см³; b=300.00 мм; h=487.00 мм; ix=201.87 мм; iy=66.92 мм; r=26.00 мм; s=14.50 мм; t=17.50 мм; Вертикальный центроид=243.50 мм; Высота=487.00 мм; Горизонтальный центроид=150.00 мм; Номинальный вес=138.40 килограмм-сила/м; Носок полки сопряжения=33.25 мм; Носок ребра жесткости сопряжения=43.50 мм; Площадь сечения=176.3 см²; Сопряжение ребра жесткости=26.00 мм; Толщина полки=17.50 мм; Толщина ребра жесткости=14.50 мм; Чистая высота ребра жесткости=452.00 мм; Ширина=300.00 мм
- 50Ш3: ADSK_Масса на единицу длины=156.10 кг/м; Ix=83437.19 см4; Iy=9251.07 см4; Sx=1912.7 см³; Sy=478.8 см³; Wx=3384.9 см³; Wy=616.7 см³; b=300.00 мм; h=493.00 мм; ix=204.83 мм; iy=68.21 мм; r=26.00 мм; s=15.50 мм; t=20.50 мм; Вертикальный центроид=246.50 мм; Высота=493.00 мм; Горизонтальный центроид=150.00 мм; Номинальный вес=156.10 килограмм-сила/м; Носок полки сопряжения=33.75 мм; Носок ребра жесткости сопряжения=46.50 мм; Площадь сечения=198.9 см²; Сопряжение ребра жесткости=26.00 мм; Толщина полки=20.50 мм; Толщина ребра жесткости=15.50 мм; Чистая высота ребра жесткости=452.00 мм; Ширина=300.00 мм
- 50Ш4: ADSK_Масса на единицу длины=173.80 кг/м; Ix=95277.59 см4; Iy=10604.77 см4; Sx=2161.4 см³; Sy=548.2 см³; Wx=3818.7 см³; Wy=707.0 см³; b=300.00 мм; h=499.00 мм; ix=207.45 мм; iy=69.21 мм; r=26.00 мм; s=16.50 мм; t=23.50 мм; Вертикальный центроид=249.50 мм; Высота=499.00 мм; Горизонтальный центроид=150.00 мм; Номинальный вес=173.80 килограмм-сила/м; Носок полки сопряжения=34.25 мм; Носок ребра жесткости сопряжения=49.50 мм; Площадь сечения=221.4 см²; Сопряжение ребра жесткости=26.00 мм; Толщина полки=23.50 мм; Толщина ребра жесткости=16.50 мм; Чистая высота ребра жесткости=452.00 мм; Ширина=300.00 мм
- 50Ш5: ADSK_Масса на единицу длины=204.70 кг/м; Ix=114959.83 см4; Iy=12894.50 см4; Sx=2578.6 см³; Sy=663.3 см³; Wx=4526.0 см³; Wy=853.9 см³; b=302.00 мм; h=508.00 мм; ix=209.95 мм; iy=70.31 мм; r=26.00 мм; s=19.00 мм; t=28.00 мм; Вертикальный центроид=254.00 мм; Высота=508.00 мм; Горизонтальный центроид=151.00 мм; Номинальный вес=204.70 килограмм-сила/м; Носок полки сопряжения=35.50 мм; Носок ребра жесткости сопряжения=54.00 мм; Площадь сечения=260.8 см²; Сопряжение ребра жесткости=26.00 мм; Толщина полки=28.00 мм; Толщина ребра жесткости=19.00 мм; Чистая высота ребра жесткости=452.00 мм; Ширина=302.00 мм
- 50Ш6: ADSK_Масса на единицу длины=243.20 кг/м; Ix=140248.12 см4; Iy=16442.93 см4; Sx=3106.5 см³; Sy=825.1 см³; Wx=5415.0 см³; Wy=1060.8 см³; b=310.00 мм; h=518.00 мм; ix=212.75 мм; iy=72.85 мм; r=26.00 мм; s=22.00 мм; t=33.00 мм; Вертикальный центроид=259.00 мм; Высота=518.00 мм; Горизонтальный центроид=155.00 мм; Номинальный вес=243.20 килограмм-сила/м; Носок полки сопряжения=37.00 мм; Носок ребра жесткости сопряжения=59.00 мм; Площадь сечения=309.8 см²; Сопряжение ребра жесткости=26.00 мм; Толщина полки=33.00 мм; Толщина ребра жесткости=22.00 мм; Чистая высота ребра жесткости=452.00 мм; Ширина=310.00 мм
- 50Ш7: ADSK_Масса на единицу длины=292.70 кг/м; Ix=174203.77 см4; Iy=20335.66 см4; Sx=3798.0 см³; Sy=1017.1 см³; Wx=6549.0 см³; Wy=1303.6 см³; b=312.00 мм; h=532.00 мм; ix=216.13 мм; iy=73.84 мм; r=26.00 мм; s=26.00 мм; t=40.00 мм; Вертикальный центроид=266.00 мм; Высота=532.00 мм; Горизонтальный центроид=156.00 мм; Номинальный вес=292.70 килограмм-сила/м; Носок полки сопряжения=39.00 мм; Носок ребра жесткости сопряжения=66.00 мм; Площадь сечения=372.9 см²; Сопряжение ребра жесткости=26.00 мм; Толщина полки=40.00 мм; Толщина ребра жесткости=26.00 мм; Чистая высота ребра жесткости=452.00 мм; Ширина=312.00 мм
- 50Ш8: ADSK_Масса на единицу длины=347.60 кг/м; Ix=214879.98 см4; Iy=24895.52 см4; Sx=4598.0 см³; Sy=1240.0 см³; Wx=7842.3 см³; Wy=1585.7 см³; b=314.00 мм; h=548.00 мм; ix=220.28 мм; iy=74.98 мм; r=26.00 мм; s=30.00 мм; t=48.00 мм; Вертикальный центроид=274.00 мм; Высота=548.00 мм; Горизонтальный центроид=157.00 мм; Номинальный вес=347.60 килограмм-сила/м; Носок полки сопряжения=41.00 мм; Носок ребра жесткости сопряжения=74.00 мм; Площадь сечения=442.8 см²; Сопряжение ребра жесткости=26.00 мм; Толщина полки=48.00 мм; Толщина ребра жесткости=30.00 мм; Чистая высота ребра жесткости=452.00 мм; Ширина=314.00 мм
- 60Ш1: ADSK_Масса на единицу длины=137.00 кг/м; Ix=102709.98 см4; Iy=7669.85 см4; Sx=1981.3 см³; Sy=396.5 см³; Wx=3529.6 см³; Wy=511.3 см³; b=300.00 мм; h=582.00 мм; ix=242.62 мм; iy=66.30 мм; r=28.00 мм; s=12.00 мм; t=17.00 мм; Вертикальный центроид=291.00 мм; Высота=582.00 мм; Горизонтальный центроид=150.00 мм; Номинальный вес=137.00 килограмм-сила/м; Носок полки сопряжения=34.00 мм; Носок ребра жесткости сопряжения=45.00 мм; Площадь сечения=174.5 см²; Сопряжение ребра жесткости=28.00 мм; Толщина полки=17.00 мм; Толщина ребра жесткости=12.00 мм; Чистая высота ребра жесткости=548.00 мм; Ширина=300.00 мм
- 60Ш2: ADSK_Масса на единицу длины=170.70 кг/м; Ix=126193.28 см4; Iy=9259.23 см4; Sx=2438.8 см³; Sy=483.6 см³; Wx=4285.0 см³; Wy=617.3 см³; b=300.00 мм; h=589.00 мм; ix=240.92 мм; iy=65.26 мм; r=28.00 мм; s=16.00 мм; t=20.50 мм; Вертикальный центроид=294.50 мм; Высота=589.00 мм; Горизонтальный центроид=150.00 мм; Номинальный вес=170.70 килограмм-сила/м; Носок полки сопряжения=36.00 мм; Носок ребра жесткости сопряжения=48.50 мм; Площадь сечения=217.4 см²; Сопряжение ребра жесткости=28.00 мм; Толщина полки=20.50 мм; Толщина ребра жесткости=16.00 мм; Чистая высота ребра жесткости=548.00 мм; Ширина=300.00 мм
- 60Ш3: ADSK_Масса на единицу длины=198.10 кг/м; Ix=150035.32 см4; Iy=11069.15 см4; Sx=2869.7 см³; Sy=578.6 см³; Wx=5026.3 см³; Wy=737.9 см³; b=300.00 мм; h=597.00 мм; ix=243.82 мм; iy=66.23 мм; r=28.00 мм; s=18.00 мм; t=24.50 мм; Вертикальный центроид=298.50 мм; Высота=597.00 мм; Горизонтальный центроид=150.00 мм; Номинальный вес=198.10 килограмм-сила/м; Носок полки сопряжения=37.00 мм; Носок ребра жесткости сопряжения=52.50 мм; Площадь сечения=252.4 см²; Сопряжение ребра жесткости=28.00 мм; Толщина полки=24.50 мм; Толщина ребра жесткости=18.00 мм; Чистая высота ребра жесткости=548.00 мм; Ширина=300.00 мм
- 60Ш4: ADSK_Масса на единицу длины=225.60 кг/м; Ix=174450.48 см4; Iy=12881.17 см4; Sx=3305.4 см³; Sy=674.1 см³; Wx=5767.0 см³; Wy=858.7 см³; b=300.00 мм; h=605.00 мм; ix=246.40 мм; iy=66.96 мм; r=28.00 мм; s=20.00 мм; t=28.50 мм; Вертикальный центроид=302.50 мм; Высота=605.00 мм; Горизонтальный центроид=150.00 мм; Номинальный вес=225.60 килограмм-сила/м; Носок полки сопряжения=38.00 мм; Носок ребра жесткости сопряжения=56.50 мм; Площадь сечения=287.3 см²; Сопряжение ребра жесткости=28.00 мм; Толщина полки=28.50 мм; Толщина ребра жесткости=20.00 мм; Чистая высота ребра жесткости=548.00 мм; Ширина=300.00 мм
- 60Ш5: ADSK_Масса на единицу длины=265.40 кг/м; Ix=210467.04 см4; Iy=15686.68 см4; Sx=3941.5 см³; Sy=817.4 см³; Wx=6833.4 см³; Wy=1038.9 см³; b=302.00 мм; h=616.00 мм; ix=249.49 мм; iy=68.11 мм; r=28.00 мм; s=23.00 мм; t=34.00 мм; Вертикальный центроид=308.00 мм; Высота=616.00 мм; Горизонтальный центроид=151.00 мм; Номинальный вес=265.40 килограмм-сила/м; Носок полки сопряжения=39.50 мм; Носок ребра жесткости сопряжения=62.00 мм; Площадь сечения=338.1 см²; Сопряжение ребра жесткости=28.00 мм; Толщина полки=34.00 мм; Толщина ребра жесткости=23.00 мм; Чистая высота ребра жесткости=548.00 мм; Ширина=302.00 мм
- 60Ш6: ADSK_Масса на единицу длины=324.20 кг/м; Ix=266239.93 см4; Iy=21476.18 см4; Sx=4907.1 см³; Sy=1073.6 см³; Wx=8452.1 см³; Wy=1363.6 см³; b=315.00 мм; h=630.00 мм; ix=253.90 мм; iy=72.11 мм; r=28.00 мм; s=27.00 мм; t=41.00 мм; Вертикальный центроид=315.00 мм; Высота=630.00 мм; Горизонтальный центроид=157.50 мм; Номинальный вес=324.20 килограмм-сила/м; Носок полки сопряжения=41.50 мм; Носок ребра жесткости сопряжения=69.00 мм; Площадь сечения=413.0 см²; Сопряжение ребра жесткости=28.00 мм; Толщина полки=41.00 мм; Толщина ребра жесткости=27.00 мм; Чистая высота ребра жесткости=548.00 мм; Ширина=315.00 мм
- 60Ш7: ADSK_Масса на единицу длины=377.50 кг/м; Ix=318172.04 см4; Iy=25653.76 см4; Sx=5788.1 см³; Sy=1279.0 см³; Wx=9881.1 см³; Wy=1618.5 см³; b=317.00 мм; h=644.00 мм; ix=257.21 мм; iy=73.04 мм; r=28.00 мм; s=31.00 мм; t=48.00 мм; Вертикальный центроид=322.00 мм; Высота=644.00 мм; Горизонтальный центроид=158.50 мм; Номинальный вес=377.50 килограмм-сила/м; Носок полки сопряжения=43.50 мм; Носок ребра жесткости сопряжения=76.00 мм; Площадь сечения=480.9 см²; Сопряжение ребра жесткости=28.00 мм; Толщина полки=48.00 мм; Толщина ребра жесткости=31.00 мм; Чистая высота ребра жесткости=548.00 мм; Ширина=317.00 мм
- 60Ш8: ADSK_Масса на единицу длины=450.60 кг/м; Ix=394963.73 см4; Iy=31634.21 см4; Sx=7047.6 см³; Sy=1572.5 см³; Wx=11896.5 см³; Wy=1983.3 см³; b=319.00 мм; h=664.00 мм; ix=262.30 мм; iy=74.23 мм; r=28.00 мм; s=36.00 мм; t=58.00 мм; Вертикальный центроид=332.00 мм; Высота=664.00 мм; Горизонтальный центроид=159.50 мм; Номинальный вес=450.60 килограмм-сила/м; Носок полки сопряжения=46.00 мм; Носок ребра жесткости сопряжения=86.00 мм; Площадь сечения=574.1 см²; Сопряжение ребра жесткости=28.00 мм; Толщина полки=58.00 мм; Толщина ребра жесткости=36.00 мм; Чистая высота ребра жесткости=548.00 мм; Ширина=319.00 мм
- 70Ш1: ADSK_Масса на единицу длины=166.00 кг/м; Ix=172424.05 см4; Iy=9024.74 см4; Sx=2814.4 см³; Sy=468.1 см³; Wx=4983.4 см³; Wy=601.7 см³; b=300.00 мм; h=692.00 мм; ix=285.53 мм; iy=65.32 мм; r=28.00 мм; s=13.00 мм; t=20.00 мм; Вертикальный центроид=346.00 мм; Высота=692.00 мм; Горизонтальный центроид=150.00 мм; Номинальный вес=166.00 килограмм-сила/м; Носок полки сопряжения=34.50 мм; Носок ребра жесткости сопряжения=48.00 мм; Площадь сечения=211.5 см²; Сопряжение ребра жесткости=28.00 мм; Толщина полки=20.00 мм; Толщина ребра жесткости=13.00 мм; Чистая высота ребра жесткости=652.00 мм; Ширина=300.00 мм
- 70Ш2: ADSK_Масса на единицу длины=190.40 кг/м; Ix=198779.77 см4; Iy=10382.92 см4; Sx=3233.4 см³; Sy=540.5 см³; Wx=5695.7 см³; Wy=692.2 см³; b=300.00 мм; h=698.00 мм; ix=286.29 мм; iy=65.43 мм; r=28.00 мм; s=15.00 мм; t=23.00 мм; Вертикальный центроид=349.00 мм; Высота=698.00 мм; Горизонтальный центроид=150.00 мм; Номинальный вес=190.40 килограмм-сила/м; Носок полки сопряжения=35.50 мм; Носок ребра жесткости сопряжения=51.00 мм; Площадь сечения=242.5 см²; Сопряжение ребра жесткости=28.00 мм; Толщина полки=23.00 мм; Толщина ребра жесткости=15.00 мм; Чистая высота ребра жесткости=652.00 мм; Ширина=300.00 мм
- 70Ш3: ADSK_Масса на единицу длины=226.90 кг/м; Ix=239021.10 см4; Iy=12424.20 см4; Sx=3867.0 см³; Sy=650.3 см³; Wx=6761.6 см³; Wy=828.3 см³; b=300.00 мм; h=707.00 мм; ix=287.54 мм; iy=65.56 мм; r=28.00 мм; s=18.00 мм; t=27.50 мм; Вертикальный центроид=353.50 мм; Высота=707.00 мм; Горизонтальный центроид=150.00 мм; Номинальный вес=226.90 килограмм-сила/м; Носок полки сопряжения=37.00 мм; Носок ребра жесткости сопряжения=55.50 мм; Площадь сечения=289.1 см²; Сопряжение ребра жесткости=28.00 мм; Толщина полки=27.50 мм; Толщина ребра жесткости=18.00 мм; Чистая высота ребра жесткости=652.00 мм; Ширина=300.00 мм
- 70Ш4: ADSK_Масса на единицу длины=258.60 кг/м; Ix=275127.01 см4; Iy=14242.00 см4; Sx=4426.5 см³; Sy=748.6 см³; Wx=7695.9 см³; Wy=949.5 см³; b=300.00 мм; h=715.00 мм; ix=289.01 мм; iy=65.76 мм; r=28.00 мм; s=20.50 мм; t=31.50 мм; Вертикальный центроид=357.50 мм; Высота=715.00 мм; Горизонтальный центроид=150.00 мм; Номинальный вес=258.60 килограмм-сила/м; Носок полки сопряжения=38.25 мм; Носок ребра жесткости сопряжения=59.50 мм; Площадь сечения=329.4 см²; Сопряжение ребра жесткости=28.00 мм; Толщина полки=31.50 мм; Толщина ребра жесткости=20.50 мм; Чистая высота ребра жесткости=652.00 мм; Ширина=300.00 мм
- 70Ш5: ADSK_Масса на единицу длины=294.90 кг/м; Ix=319781.96 см4; Iy=16514.18 см4; Sx=5099.3 см³; Sy=870.3 см³; Wx=8821.6 см³; Wy=1101.0 см³; b=300.00 мм; h=725.00 мм; ix=291.75 мм; iy=66.30 мм; r=28.00 мм; s=23.00 мм; t=36.50 мм; Вертикальный центроид=362.50 мм; Высота=725.00 мм; Горизонтальный центроид=150.00 мм; Номинальный вес=294.90 килограмм-сила/м; Носок полки сопряжения=39.50 мм; Носок ребра жесткости сопряжения=64.50 мм; Площадь сечения=375.7 см²; Сопряжение ребра жесткости=28.00 мм; Толщина полки=36.50 мм; Толщина ребра жесткости=23.00 мм; Чистая высота ребра жесткости=652.00 мм; Ширина=300.00 мм
- 70Ш6: ADSK_Масса на единицу длины=359.70 кг/м; Ix=403258.33 см4; Iy=22622.21 см4; Sx=6335.0 см³; Sy=1143.7 см³; Wx=10898.9 см³; Wy=1445.5 см³; b=313.00 мм; h=740.00 мм; ix=296.66 мм; iy=70.26 мм; r=28.00 мм; s=27.00 мм; t=44.00 мм; Вертикальный центроид=370.00 мм; Высота=740.00 мм; Горизонтальный центроид=156.50 мм; Номинальный вес=359.70 килограмм-сила/м; Носок полки сопряжения=41.50 мм; Носок ребра жесткости сопряжения=72.00 мм; Площадь сечения=458.2 см²; Сопряжение ребра жесткости=28.00 мм; Толщина полки=44.00 мм; Толщина ребра жесткости=27.00 мм; Чистая высота ребра жесткости=652.00 мм; Ширина=313.00 мм
- 70Ш7: ADSK_Масса на единицу длины=431.20 кг/м; Ix=496466.98 см4; Iy=27822.58 см4; Sx=7693.0 см³; Sy=1405.7 см³; Wx=13099.4 см³; Wy=1766.5 см³; b=315.00 мм; h=758.00 мм; ix=300.64 мм; iy=71.17 мм; r=28.00 мм; s=32.00 мм; t=53.00 мм; Вертикальный центроид=379.00 мм; Высота=758.00 мм; Горизонтальный центроид=157.50 мм; Номинальный вес=431.20 килограмм-сила/м; Носок полки сопряжения=44.00 мм; Носок ребра жесткости сопряжения=81.00 мм; Площадь сечения=549.3 см²; Сопряжение ребра жесткости=28.00 мм; Толщина полки=53.00 мм; Толщина ребра жесткости=32.00 мм; Чистая высота ребра жесткости=652.00 мм; Ширина=315.00 мм
- 70Ш8: ADSK_Масса на единицу длины=518.30 кг/м; Ix=616075.38 см4; Iy=34321.60 см4; Sx=9389.9 см³; Sy=1734.0 см³; Wx=15796.8 см³; Wy=2165.4 см³; b=317.00 мм; h=780.00 мм; ix=305.47 мм; iy=72.10 мм; r=28.00 мм; s=38.00 мм; t=64.00 мм; Вертикальный центроид=390.00 мм; Высота=780.00 мм; Горизонтальный центроид=158.50 мм; Номинальный вес=518.30 килограмм-сила/м; Носок полки сопряжения=47.00 мм; Носок ребра жесткости сопряжения=92.00 мм; Площадь сечения=660.3 см²; Сопряжение ребра жесткости=28.00 мм; Толщина полки=64.00 мм; Толщина ребра жесткости=38.00 мм; Чистая высота ребра жесткости=652.00 мм; Ширина=317.00 мм
- 80Ш1: ADSK_Масса на единицу длины=164.60 кг/м; Ix=205458.00 см4; Iy=7676.70 см4; Sx=3018.9 см³; Sy=401.3 см³; Wx=5254.7 см³; Wy=511.8 см³; b=300.00 мм; h=782.00 мм; ix=313.01 мм; iy=60.50 мм; r=28.00 мм; s=13.50 мм; t=17.00 мм; Вертикальный центроид=391.00 мм; Высота=782.00 мм; Горизонтальный центроид=150.00 мм; Номинальный вес=164.60 килограмм-сила/м; Носок полки сопряжения=34.75 мм; Носок ребра жесткости сопряжения=45.00 мм; Площадь сечения=209.7 см²; Сопряжение ребра жесткости=28.00 мм; Толщина полки=17.00 мм; Толщина ребра жесткости=13.50 мм; Чистая высота ребра жесткости=748.00 мм; Ширина=300.00 мм
- 80Ш2: ADSK_Масса на единицу длины=191.10 кг/м; Ix=253655.00 см4; Iy=9928.90 см4; Sx=3644.1 см³; Sy=517.8 см³; Wx=6405.4 см³; Wy=661.9 см³; b=300.00 мм; h=792.00 мм; ix=322.79 мм; iy=63.86 мм; r=28.00 мм; s=14.00 мм; t=22.00 мм; Вертикальный центроид=396.00 мм; Высота=792.00 мм; Горизонтальный центроид=150.00 мм; Номинальный вес=191.10 килограмм-сила/м; Носок полки сопряжения=35.00 мм; Носок ребра жесткости сопряжения=50.00 мм; Площадь сечения=243.5 см²; Сопряжение ребра жесткости=28.00 мм; Толщина полки=22.00 мм; Толщина ребра жесткости=14.00 мм; Чистая высота ребра жесткости=748.00 мм; Ширина=300.00 мм
- 90Ш1: ADSK_Масса на единицу длины=191.50 кг/м; Ix=292583.00 см4; Iy=8278.50 см4; Sx=3861.2 см³; Sy=270.9 см³; Wx=6642.1 см³; Wy=553.7 см³; b=299.00 мм; h=881.00 мм; ix=346.31 мм; iy=58.25 мм; r=28.00 мм; s=15.00 мм; t=18.50 мм; Вертикальный центроид=440.50 мм; Высота=881.00 мм; Горизонтальный центроид=149.50 мм; Номинальный вес=191.50 килограмм-сила/м; Носок полки сопряжения=35.50 мм; Носок ребра жесткости сопряжения=46.50 мм; Площадь сечения=244.0 см²; Сопряжение ребра жесткости=28.00 мм; Толщина полки=18.50 мм; Толщина ребра жесткости=15.00 мм; Чистая высота ребра жесткости=844.00 мм; Ширина=299.00 мм
- 90Ш2: ADSK_Масса на единицу длины=212.60 кг/м; Ix=345335.00 см4; Iy=10283.30 см4; Sx=4457.0 см³; Sy=543.1 см³; Wx=7760.3 см³; Wy=687.8 см³; b=299.00 мм; h=890.00 мм; ix=357.06 мм; iy=61.61 мм; r=28.00 мм; s=15.00 мм; t=23.00 мм; Вертикальный центроид=445.00 мм; Высота=890.00 мм; Горизонтальный центроид=149.50 мм; Номинальный вес=212.60 килограмм-сила/м; Носок полки сопряжения=35.50 мм; Носок ребра жесткости сопряжения=51.00 мм; Площадь сечения=270.9 см²; Сопряжение ребра жесткости=28.00 мм; Толщина полки=23.00 мм; Толщина ребра жесткости=15.00 мм; Чистая высота ребра жесткости=844.00 мм; Ширина=299.00 мм
- 100Ш1: ADSK_Масса на единицу длины=230.60 кг/м; Ix=446000.00 см4; Iy=11520.00 см4; Sx=5234.0 см³; Sy=573.7 см³; Wx=9011.0 см³; Wy=719.9 см³; b=320.00 мм; h=990.00 мм; ix=389.61 мм; iy=62.62 мм; r=30.00 мм; s=16.00 мм; t=21.00 мм; Вертикальный центроид=495.00 мм; Высота=990.00 мм; Горизонтальный центроид=160.00 мм; Номинальный вес=230.60 килограмм-сила/м; Носок полки сопряжения=38.00 мм; Носок ребра жесткости сопряжения=51.00 мм; Площадь сечения=293.8 см²; Сопряжение ребра жесткости=30.00 мм; Толщина полки=21.00 мм; Толщина ребра жесткости=16.00 мм; Чистая высота ребра жесткости=948.00 мм; Ширина=320.00 мм
- 100Ш2: ADSK_Масса на единицу длины=258.20 кг/м; Ix=516400.00 см4; Iy=13710.00 см4; Sx=5980.0 см³; Sy=680.1 см³; Wx=10350.0 см³; Wy=856.9 см³; b=320.00 мм; h=998.00 мм; ix=396.24 мм; iy=64.56 мм; r=30.00 мм; s=17.00 мм; t=25.00 мм; Вертикальный центроид=499.00 мм; Высота=998.00 мм; Горизонтальный центроид=160.00 мм; Номинальный вес=258.20 килограмм-сила/м; Носок полки сопряжения=38.50 мм; Носок ребра жесткости сопряжения=55.00 мм; Площадь сечения=328.9 см²; Сопряжение ребра жесткости=30.00 мм; Толщина полки=25.00 мм; Толщина ребра жесткости=17.00 мм; Чистая высота ребра жесткости=948.00 мм; Ширина=320.00 мм
- 100Ш3: ADSK_Масса на единицу длины=285.70 кг/м; Ix=587700.00 см4; Iy=15900.00 см4; Sx=6736.0 см³; Sy=786.9 см³; Wx=11680.0 см³; Wy=993.9 см³; b=320.00 мм; h=1006.00 мм; ix=401.82 мм; iy=66.09 мм; r=30.00 мм; s=18.00 мм; t=29.00 мм; Вертикальный центроид=503.00 мм; Высота=1006.00 мм; Горизонтальный центроид=160.00 мм; Номинальный вес=285.70 килограмм-сила/м; Носок полки сопряжения=39.00 мм; Носок ребра жесткости сопряжения=59.00 мм; Площадь сечения=364.0 см²; Сопряжение ребра жесткости=30.00 мм; Толщина полки=29.00 мм; Толщина ребра жесткости=18.00 мм; Чистая высота ребра жесткости=948.00 мм; Ширина=320.00 мм
- 100Ш4: ADSK_Масса на единицу длины=314.50 кг/м; Ix=655400.00 см4; Iy=17830.00 см4; Sx=7470.0 см³; Sy=883.5 см³; Wx=12940.0 см³; Wy=1114.3 см³; b=320.00 мм; h=1013.00 мм; ix=404.48 мм; iy=66.71 мм; r=30.00 мм; s=19.50 мм; t=32.50 мм; Вертикальный центроид=506.50 мм; Высота=1013.00 мм; Горизонтальный центроид=160.00 мм; Номинальный вес=314.50 килограмм-сила/м; Носок полки сопряжения=39.75 мм; Носок ребра жесткости сопряжения=62.50 мм; Площадь сечения=400.6 см²; Сопряжение ребра жесткости=30.00 мм; Толщина полки=32.50 мм; Толщина ребра жесткости=19.50 мм; Чистая высота ребра жесткости=948.00 мм; Ширина=320.00 мм
- 15К1: ADSK_Масса на единицу длины=26.80 кг/м; Ix=1366.76 см4; Iy=469.21 см4; Sx=103.6 см³; Sy=48.1 см³; Wx=186.0 см³; Wy=63.0 см³; b=149.00 мм; h=147.00 мм; ix=63.25 мм; iy=37.06 мм; r=11.00 мм; s=6.00 мм; t=8.50 мм; Вертикальный центроид=73.50 мм; Высота=147.00 мм; Горизонтальный центроид=74.50 мм; Номинальный вес=26.80 килограмм-сила/м; Носок полки сопряжения=14.00 мм; Носок ребра жесткости сопряжения=19.50 мм; Площадь сечения=34.2 см²; Сопряжение ребра жесткости=11.00 мм; Толщина полки=8.50 мм; Толщина ребра жесткости=6.00 мм; Чистая высота ребра жесткости=130.00 мм; Ширина=149.00 мм
- 15К2: ADSK_Масса на единицу длины=31.50 кг/м; Ix=1641.33 см4; Iy=563.28 см4; Sx=123.0 см³; Sy=57.4 см³; Wx=218.8 см³; Wy=75.1 см³; b=150.00 мм; h=150.00 мм; ix=63.95 мм; iy=37.46 мм; r=11.00 мм; s=7.00 мм; t=10.00 мм; Вертикальный центроид=75.00 мм; Высота=150.00 мм; Горизонтальный центроид=75.00 мм; Номинальный вес=31.50 килограмм-сила/м; Носок полки сопряжения=14.50 мм; Носок ребра жесткости сопряжения=21.00 мм; Площадь сечения=40.1 см²; Сопряжение ребра жесткости=11.00 мм; Толщина полки=10.00 мм; Толщина ребра жесткости=7.00 мм; Чистая высота ребра жесткости=130.00 мм; Ширина=150.00 мм
- 15К3: ADSK_Масса на единицу длины=39.10 кг/м; Ix=2117.61 см4; Iy=718.46 см4; Sx=155.7 см³; Sy=72.8 см³; Wx=273.2 см³; Wy=95.2 см³; b=151.00 мм; h=155.00 мм; ix=65.18 мм; iy=37.97 мм; r=11.00 мм; s=8.50 мм; t=12.50 мм; Вертикальный центроид=77.50 мм; Высота=155.00 мм; Горизонтальный центроид=75.50 мм; Номинальный вес=39.10 килограмм-сила/м; Носок полки сопряжения=15.25 мм; Носок ребра жесткости сопряжения=23.50 мм; Площадь сечения=49.8 см²; Сопряжение ребра жесткости=11.00 мм; Толщина полки=12.50 мм; Толщина ребра жесткости=8.50 мм; Чистая высота ребра жесткости=130.00 мм; Ширина=151.00 мм
- 15К4: ADSK_Масса на единицу длины=46.80 кг/м; Ix=2629.16 см4; Iy=879.66 см4; Sx=189.7 см³; Sy=88.7 см³; Wx=328.6 см³; Wy=115.7 см³; b=152.00 мм; h=160.00 мм; ix=66.40 мм; iy=38.41 мм; r=11.00 мм; s=10.00 мм; t=15.00 мм; Вертикальный центроид=80.00 мм; Высота=160.00 мм; Горизонтальный центроид=76.00 мм; Номинальный вес=46.80 килограмм-сила/м; Носок полки сопряжения=16.00 мм; Носок ребра жесткости сопряжения=26.00 мм; Площадь сечения=59.6 см²; Сопряжение ребра жесткости=11.00 мм; Толщина полки=15.00 мм; Толщина ребра жесткости=10.00 мм; Чистая высота ребра жесткости=130.00 мм; Ширина=152.00 мм
- 15К5: ADSK_Масса на единицу длины=56.30 кг/м; Ix=3291.43 см4; Iy=1077.13 см4; Sx=232.4 см³; Sy=108.1 см³; Wx=396.6 см³; Wy=140.8 см³; b=153.00 мм; h=166.00 мм; ix=67.74 мм; iy=38.75 мм; r=11.00 мм; s=12.00 мм; t=18.00 мм; Вертикальный центроид=83.00 мм; Высота=166.00 мм; Горизонтальный центроид=76.50 мм; Номинальный вес=56.30 килограмм-сила/м; Носок полки сопряжения=17.00 мм; Носок ребра жесткости сопряжения=29.00 мм; Площадь сечения=71.7 см²; Сопряжение ребра жесткости=11.00 мм; Толщина полки=18.00 мм; Толщина ребра жесткости=12.00 мм; Чистая высота ребра жесткости=130.00 мм; Ширина=153.00 мм
- 20К1: ADSK_Масса на единицу длины=41.40 кг/м; Ix=3846.06 см4; Iy=1314.47 см4; Sx=216.4 см³; Sy=100.4 см³; Wx=392.5 см³; Wy=132.1 см³; b=199.00 мм; h=196.00 мм; ix=85.44 мм; iy=49.95 мм; r=13.00 мм; s=6.50 мм; t=10.00 мм; Вертикальный центроид=98.00 мм; Высота=196.00 мм; Горизонтальный центроид=99.50 мм; Номинальный вес=41.40 килограмм-сила/м; Носок полки сопряжения=16.25 мм; Носок ребра жесткости сопряжения=23.00 мм; Площадь сечения=52.7 см²; Сопряжение ребра жесткости=13.00 мм; Толщина полки=10.00 мм; Толщина ребра жесткости=6.50 мм; Чистая высота ребра жесткости=176.00 мм; Ширина=199.00 мм
- 20К2: ADSK_Масса на единицу длины=49.90 кг/м; Ix=4715.63 см4; Iy=1601.53 см4; Sx=262.8 см³; Sy=121.9 см³; Wx=471.6 см³; Wy=160.2 см³; b=200.00 мм; h=200.00 мм; ix=86.15 мм; iy=50.21 мм; r=13.00 мм; s=8.00 мм; t=12.00 мм; Вертикальный центроид=100.00 мм; Высота=200.00 мм; Горизонтальный центроид=100.00 мм; Номинальный вес=49.90 килограмм-сила/м; Носок полки сопряжения=17.00 мм; Носок ребра жесткости сопряжения=25.00 мм; Площадь сечения=63.5 см²; Сопряжение ребра жесткости=13.00 мм; Толщина полки=12.00 мм; Толщина ребра жесткости=8.00 мм; Чистая высота ребра жесткости=176.00 мм; Ширина=200.00 мм
- 20К3: ADSK_Масса на единицу длины=57.80 кг/м; Ix=5602.48 см4; Iy=1896.76 см4; Sx=308.4 см³; Sy=143.7 см³; Wx=549.3 см³; Wy=188.7 см³; b=201.00 мм; h=204.00 мм; ix=87.26 мм; iy=50.78 мм; r=13.00 мм; s=9.00 мм; t=14.00 мм; Вертикальный центроид=102.00 мм; Высота=204.00 мм; Горизонтальный центроид=100.50 мм; Номинальный вес=57.80 килограмм-сила/м; Носок полки сопряжения=17.50 мм; Носок ребра жесткости сопряжения=27.00 мм; Площадь сечения=73.6 см²; Сопряжение ребра жесткости=13.00 мм; Толщина полки=14.00 мм; Толщина ребра жесткости=9.00 мм; Чистая высота ребра жесткости=176.00 мм; Ширина=201.00 мм
- 20К4: ADSK_Масса на единицу длины=69.30 кг/м; Ix=6962.62 см4; Iy=2303.59 см4; Sx=376.6 см³; Sy=174.7 см³; Wx=663.1 см³; Wy=229.2 см³; b=201.00 мм; h=210.00 мм; ix=88.81 мм; iy=51.09 мм; r=13.00 мм; s=10.50 мм; t=17.00 мм; Вертикальный центроид=105.00 мм; Высота=210.00 мм; Горизонтальный центроид=100.50 мм; Номинальный вес=69.30 килограмм-сила/м; Носок полки сопряжения=18.25 мм; Носок ребра жесткости сопряжения=30.00 мм; Площадь сечения=88.3 см²; Сопряжение ребра жесткости=13.00 мм; Толщина полки=17.00 мм; Толщина ребра жесткости=10.50 мм; Чистая высота ребра жесткости=176.00 мм; Ширина=201.00 мм
- 20К5: ADSK_Масса на единицу длины=78.00 кг/м; Ix=7970.40 см4; Iy=2613.87 см4; Sx=426.8 см³; Sy=197.6 см³; Wx=744.9 см³; Wy=258.8 см³; b=202.00 мм; h=214.00 мм; ix=89.58 мм; iy=51.30 мм; r=13.00 мм; s=12.00 мм; t=19.00 мм; Вертикальный центроид=107.00 мм; Высота=214.00 мм; Горизонтальный центроид=101.00 мм; Номинальный вес=78.00 килограмм-сила/м; Носок полки сопряжения=19.00 мм; Носок ребра жесткости сопряжения=32.00 мм; Площадь сечения=99.3 см²; Сопряжение ребра жесткости=13.00 мм; Толщина полки=19.00 мм; Толщина ребра жесткости=12.00 мм; Чистая высота ребра жесткости=176.00 мм; Ширина=202.00 мм
- 20К6: ADSK_Масса на единицу длины=90.30 кг/м; Ix=9488.15 см4; Iy=3027.75 см4; Sx=500.3 см³; Sy=229.5 см³; Wx=862.6 см³; Wy=299.8 см³; b=202.00 мм; h=220.00 мм; ix=90.84 мм; iy=51.32 мм; r=13.00 мм; s=14.00 мм; t=22.00 мм; Вертикальный центроид=110.00 мм; Высота=220.00 мм; Горизонтальный центроид=101.00 мм; Номинальный вес=90.30 килограмм-сила/м; Носок полки сопряжения=20.00 мм; Носок ребра жесткости сопряжения=35.00 мм; Площадь сечения=115.0 см²; Сопряжение ребра жесткости=13.00 мм; Толщина полки=22.00 мм; Толщина ребра жесткости=14.00 мм; Чистая высота ребра жесткости=176.00 мм; Ширина=202.00 мм
- 20К7: ADSK_Масса на единицу длины=102.90 кг/м; Ix=11136.66 см4; Iy=3493.41 см4; Sx=578.2 см³; Sy=264.0 см³; Wx=985.6 см³; Wy=344.2 см³; b=203.00 мм; h=226.00 мм; ix=92.16 мм; iy=51.62 мм; r=13.00 мм; s=16.00 мм; t=25.00 мм; Вертикальный центроид=113.00 мм; Высота=226.00 мм; Горизонтальный центроид=101.50 мм; Номинальный вес=102.90 килограмм-сила/м; Носок полки сопряжения=21.00 мм; Носок ребра жесткости сопряжения=38.00 мм; Площадь сечения=131.1 см²; Сопряжение ребра жесткости=13.00 мм; Толщина полки=25.00 мм; Толщина ребра жесткости=16.00 мм; Чистая высота ребра жесткости=176.00 мм; Ширина=203.00 мм
- 20К8: ADSK_Масса на единицу длины=118.40 кг/м; Ix=13375.48 см4; Iy=4053.99 см4; Sx=679.3 см³; Sy=306.8 см³; Wx=1143.2 см³; Wy=399.4 см³; b=203.00 мм; h=234.00 мм; ix=94.16 мм; iy=51.84 мм; r=13.00 мм; s=18.00 мм; t=29.00 мм; Вертикальный центроид=117.00 мм; Высота=234.00 мм; Горизонтальный центроид=101.50 мм; Номинальный вес=118.40 килограмм-сила/м; Носок полки сопряжения=22.00 мм; Носок ребра жесткости сопряжения=42.00 мм; Площадь сечения=150.9 см²; Сопряжение ребра жесткости=13.00 мм; Толщина полки=29.00 мм; Толщина ребра жесткости=18.00 мм; Чистая высота ребра жесткости=176.00 мм; Ширина=203.00 мм
- 25К1: ADSK_Масса на единицу длины=62.60 кг/м; Ix=9170.92 см4; Iy=3090.06 см4; Sx=410.7 см³; Sy=188.6 см³; Wx=745.6 см³; Wy=248.2 см³; b=249.00 мм; h=246.00 мм; ix=107.26 мм; iy=62.26 мм; r=16.00 мм; s=8.00 мм; t=12.00 мм; Вертикальный центроид=123.00 мм; Высота=246.00 мм; Горизонтальный центроид=124.50 мм; Номинальный вес=62.60 килограмм-сила/м; Носок полки сопряжения=20.00 мм; Носок ребра жесткости сопряжения=28.00 мм; Площадь сечения=79.7 см²; Сопряжение ребра жесткости=16.00 мм; Толщина полки=12.00 мм; Толщина ребра жесткости=8.00 мм; Чистая высота ребра жесткости=222.00 мм; Ширина=249.00 мм
- 25К2: ADSK_Масса на единицу длины=72.40 кг/м; Ix=10832.61 см4; Iy=3648.81 см4; Sx=480.3 см³; Sy=221.9 см³; Wx=866.6 см³; Wy=291.9 см³; b=250.00 мм; h=250.00 мм; ix=108.41 мм; iy=62.92 мм; r=16.00 мм; s=9.00 мм; t=14.00 мм; Вертикальный центроид=125.00 мм; Высота=250.00 мм; Горизонтальный центроид=125.00 мм; Номинальный вес=72.40 килограмм-сила/м; Носок полки сопряжения=20.50 мм; Носок ребра жесткости сопряжения=30.00 мм; Площадь сечения=92.2 см²; Сопряжение ребра жесткости=16.00 мм; Толщина полки=14.00 мм; Толщина ребра жесткости=9.00 мм; Чистая высота ребра жесткости=222.00 мм; Ширина=250.00 мм
- 25К3: ADSK_Масса на единицу длины=80.20 кг/м; Ix=12153.56 см4; Iy=4088.75 см4; Sx=535.4 см³; Sy=247.9 см³; Wx=960.8 см³; Wy=325.8 см³; b=251.00 мм; h=253.00 мм; ix=109.05 мм; iy=63.25 мм; r=16.00 мм; s=10.00 мм; t=15.50 мм; Вертикальный центроид=126.50 мм; Высота=253.00 мм; Горизонтальный центроид=125.50 мм; Номинальный вес=80.20 килограмм-сила/м; Носок полки сопряжения=21.00 мм; Носок ребра жесткости сопряжения=31.50 мм; Площадь сечения=102.2 см²; Сопряжение ребра жесткости=16.00 мм; Толщина полки=15.50 мм; Толщина ребра жесткости=10.00 мм; Чистая высота ребра жесткости=222.00 мм; Ширина=251.00 мм
- 25К4: ADSK_Масса на единицу длины=90.10 кг/м; Ix=13927.17 см4; Iy=4672.01 см4; Sx=607.7 см³; Sy=282.2 см³; Wx=1083.8 см³; Wy=370.8 см³; b=252.00 мм; h=257.00 мм; ix=110.14 мм; iy=63.79 мм; r=16.00 мм; s=11.00 мм; t=17.50 мм; Вертикальный центроид=128.50 мм; Высота=257.00 мм; Горизонтальный центроид=126.00 мм; Номинальный вес=90.10 килограмм-сила/м; Носок полки сопряжения=21.50 мм; Носок ребра жесткости сопряжения=33.50 мм; Площадь сечения=114.8 см²; Сопряжение ребра жесткости=16.00 мм; Толщина полки=17.50 мм; Толщина ребра жесткости=11.00 мм; Чистая высота ребра жесткости=222.00 мм; Ширина=252.00 мм
- 25К5: ADSK_Масса на единицу длины=103.00 кг/м; Ix=16243.92 см4; Iy=5404.02 см4; Sx=701.1 см³; Sy=325.5 см³; Wx=1240.0 см³; Wy=427.2 см³; b=253.00 мм; h=262.00 мм; ix=111.29 мм; iy=64.19 мм; r=16.00 мм; s=12.50 мм; t=20.00 мм; Вертикальный центроид=131.00 мм; Высота=262.00 мм; Горизонтальный центроид=126.50 мм; Номинальный вес=103.00 килограмм-сила/м; Носок полки сопряжения=22.25 мм; Носок ребра жесткости сопряжения=36.00 мм; Площадь сечения=131.2 см²; Сопряжение ребра жесткости=16.00 мм; Толщина полки=20.00 мм; Толщина ребра жесткости=12.50 мм; Чистая высота ребра жесткости=222.00 мм; Ширина=253.00 мм
- 25К6: ADSK_Масса на единицу длины=115.50 кг/м; Ix=18593.24 см4; Iy=6080.59 см4; Sx=794.0 см³; Sy=366.7 см³; Wx=1392.8 см³; Wy=480.7 см³; b=253.00 мм; h=267.00 мм; ix=112.42 мм; iy=64.29 мм; r=16.00 мм; s=14.00 мм; t=22.50 мм; Вертикальный центроид=133.50 мм; Высота=267.00 мм; Горизонтальный центроид=126.50 мм; Номинальный вес=115.50 килограмм-сила/м; Носок полки сопряжения=23.00 мм; Носок ребра жесткости сопряжения=38.50 мм; Площадь сечения=147.1 см²; Сопряжение ребра жесткости=16.00 мм; Толщина полки=22.50 мм; Толщина ребра жесткости=14.00 мм; Чистая высота ребра жесткости=222.00 мм; Ширина=253.00 мм
- 25К7: ADSK_Масса на единицу длины=134.90 кг/м; Ix=22416.62 см4; Iy=7452.57 см4; Sx=942.2 см³; Sy=441.0 см³; Wx=1636.3 см³; Wy=577.7 см³; b=258.00 мм; h=274.00 мм; ix=114.20 мм; iy=65.85 мм; r=16.00 мм; s=16.00 мм; t=26.00 мм; Вертикальный центроид=137.00 мм; Высота=274.00 мм; Горизонтальный центроид=129.00 мм; Номинальный вес=134.90 килограмм-сила/м; Носок полки сопряжения=24.00 мм; Носок ребра жесткости сопряжения=42.00 мм; Площадь сечения=171.9 см²; Сопряжение ребра жесткости=16.00 мм; Толщина полки=26.00 мм; Толщина ребра жесткости=16.00 мм; Чистая высота ребра жесткости=222.00 мм; Ширина=258.00 мм
- 25К8: ADSK_Масса на единицу длины=153.10 кг/м; Ix=26169.72 см4; Iy=8556.67 см4; Sx=1083.5 см³; Sy=505.1 см³; Wx=1862.6 см³; Wy=660.8 см³; b=259.00 мм; h=281.00 мм; ix=115.86 мм; iy=66.25 мм; r=16.00 мм; s=18.00 мм; t=29.50 мм; Вертикальный центроид=140.50 мм; Высота=281.00 мм; Горизонтальный центроид=129.50 мм; Номинальный вес=153.10 килограмм-сила/м; Носок полки сопряжения=25.00 мм; Носок ребра жесткости сопряжения=45.50 мм; Площадь сечения=195.0 см²; Сопряжение ребра жесткости=16.00 мм; Толщина полки=29.50 мм; Толщина ребра жесткости=18.00 мм; Чистая высота ребра жесткости=222.00 мм; Ширина=259.00 мм
- 25К9: ADSK_Масса на единицу длины=171.30 кг/м; Ix=30128.76 см4; Iy=9685.85 см4; Sx=1229.0 см³; Sy=570.3 см³; Wx=2092.3 см³; Wy=745.1 см³; b=260.00 мм; h=288.00 мм; ix=117.51 мм; iy=66.63 мм; r=16.00 мм; s=20.00 мм; t=33.00 мм; Вертикальный центроид=144.00 мм; Высота=288.00 мм; Горизонтальный центроид=130.00 мм; Номинальный вес=171.30 килограмм-сила/м; Носок полки сопряжения=26.00 мм; Носок ребра жесткости сопряжения=49.00 мм; Площадь сечения=218.2 см²; Сопряжение ребра жесткости=16.00 мм; Толщина полки=33.00 мм; Толщина ребра жесткости=20.00 мм; Чистая высота ребра жесткости=222.00 мм; Ширина=260.00 мм
- 25К10: ADSK_Масса на единицу длины=197.50 кг/м; Ix=36112.37 см4; Iy=11288.10 см4; Sx=1442.8 см³; Sy=663.5 см³; Wx=2423.7 см³; Wy=865.0 см³; b=261.00 мм; h=298.00 мм; ix=119.80 мм; iy=66.98 мм; r=16.00 мм; s=23.00 мм; t=38.00 мм; Вертикальный центроид=149.00 мм; Высота=298.00 мм; Горизонтальный центроид=130.50 мм; Номинальный вес=197.50 килограмм-сила/м; Носок полки сопряжения=27.50 мм; Носок ребра жесткости сопряжения=54.00 мм; Площадь сечения=251.6 см²; Сопряжение ребра жесткости=16.00 мм; Толщина полки=38.00 мм; Толщина ребра жесткости=23.00 мм; Чистая высота ребра жесткости=222.00 мм; Ширина=261.00 мм
- 30К1: ADSK_Масса на единицу длины=87.00 кг/м; Ix=18848.66 см4; Iy=6241.19 см4; Sx=694.6 см³; Sy=316.8 см³; Wx=1265.0 см³; Wy=417.5 см³; b=299.00 мм; h=298.00 мм; ix=130.43 мм; iy=75.05 мм; r=18.00 мм; s=9.00 мм; t=14.00 мм; Вертикальный центроид=149.00 мм; Высота=298.00 мм; Горизонтальный центроид=149.50 мм; Номинальный вес=87.00 килограмм-сила/м; Носок полки сопряжения=22.50 мм; Носок ребра жесткости сопряжения=32.00 мм; Площадь сечения=110.8 см²; Сопряжение ребра жесткости=18.00 мм; Толщина полки=14.00 мм; Толщина ребра жесткости=9.00 мм; Чистая высота ребра жесткости=270.00 мм; Ширина=299.00 мм
- 30К2: ADSK_Масса на единицу длины=94.00 кг/м; Ix=20410.21 см4; Iy=6754.83 см4; Sx=750.6 см³; Sy=342.1 см³; Wx=1360.7 см³; Wy=450.3 см³; b=300.00 мм; h=300.00 мм; ix=130.54 мм; iy=75.10 мм; r=18.00 мм; s=10.00 мм; t=15.00 мм; Вертикальный центроид=150.00 мм; Высота=300.00 мм; Горизонтальный центроид=150.00 мм; Номинальный вес=94.00 килограмм-сила/м; Носок полки сопряжения=23.00 мм; Носок ребра жесткости сопряжения=33.00 мм; Площадь сечения=119.8 см²; Сопряжение ребра жесткости=18.00 мм; Толщина полки=15.00 мм; Толщина ребра жесткости=10.00 мм; Чистая высота ребра жесткости=270.00 мм; Ширина=300.00 мм
- 30К3: ADSK_Масса на единицу длины=105.80 кг/м; Ix=21535.21 см4; Iy=7104.76 см4; Sx=806.8 см³; Sy=358.0 см³; Wx=1435.7 см³; Wy=465.9 см³; b=305.00 мм; h=300.00 мм; ix=126.40 мм; iy=72.60 мм; r=18.00 мм; s=15.00 мм; t=15.00 мм; Вертикальный центроид=150.00 мм; Высота=300.00 мм; Горизонтальный центроид=152.50 мм; Номинальный вес=105.80 килограмм-сила/м; Носок полки сопряжения=25.50 мм; Носок ребра жесткости сопряжения=33.00 мм; Площадь сечения=134.8 см²; Сопряжение ребра жесткости=18.00 мм; Толщина полки=15.00 мм; Толщина ребра жесткости=15.00 мм; Чистая высота ребра жесткости=270.00 мм; Ширина=305.00 мм
- 30К4: ADSK_Масса на единицу длины=105.80 кг/м; Ix=23380.49 см4; Iy=7732.59 см4; Sx=852.7 см³; Sy=390.5 см³; Wx=1538.2 см³; Wy=513.8 см³; b=301.00 мм; h=304.00 мм; ix=131.69 мм; iy=75.73 мм; r=18.00 мм; s=11.00 мм; t=17.00 мм; Вертикальный центроид=152.00 мм; Высота=304.00 мм; Горизонтальный центроид=150.50 мм; Номинальный вес=105.80 килограмм-сила/м; Носок полки сопряжения=23.50 мм; Носок ребра жесткости сопряжения=35.00 мм; Площадь сечения=134.8 см²; Сопряжение ребра жесткости=18.00 мм; Толщина полки=17.00 мм; Толщина ребра жесткости=11.00 мм; Чистая высота ребра жесткости=270.00 мм; Ширина=301.00 мм
- 30К5: ADSK_Масса на единицу длины=117.40 кг/м; Ix=26362.99 см4; Iy=8642.78 см4; Sx=954.0 см³; Sy=436.6 см³; Wx=1711.9 см³; Wy=574.3 см³; b=301.00 мм; h=308.00 мм; ix=132.77 мм; iy=76.02 мм; r=18.00 мм; s=12.00 мм; t=19.00 мм; Вертикальный центроид=154.00 мм; Высота=308.00 мм; Горизонтальный центроид=150.50 мм; Номинальный вес=117.40 килограмм-сила/м; Носок полки сопряжения=24.00 мм; Носок ребра жесткости сопряжения=37.00 мм; Площадь сечения=149.6 см²; Сопряжение ребра жесткости=18.00 мм; Толщина полки=19.00 мм; Толщина ребра жесткости=12.00 мм; Чистая высота ребра жесткости=270.00 мм; Ширина=301.00 мм
- 30К6: ADSK_Масса на единицу длины=129.30 кг/м; Ix=29508.74 см4; Iy=9648.60 см4; Sx=1059.4 см³; Sy=486.0 см³; Wx=1891.6 см³; Wy=639.0 см³; b=302.00 мм; h=312.00 мм; ix=133.84 мм; iy=76.53 мм; r=18.00 мм; s=13.00 мм; t=21.00 мм; Вертикальный центроид=156.00 мм; Высота=312.00 мм; Горизонтальный центроид=151.00 мм; Номинальный вес=129.30 килограмм-сила/м; Носок полки сопряжения=24.50 мм; Носок ребра жесткости сопряжения=39.00 мм; Площадь сечения=164.7 см²; Сопряжение ребра жесткости=18.00 мм; Толщина полки=21.00 мм; Толщина ребра жесткости=13.00 мм; Чистая высота ребра жесткости=270.00 мм; Ширина=302.00 мм
- 30К7: ADSK_Масса на единицу длины=142.00 кг/м; Ix=32732.42 см4; Iy=10569.09 см4; Sx=1167.9 см³; Sy=533.1 см³; Wx=2071.7 см³; Wy=699.9 см³; b=302.00 мм; h=316.00 мм; ix=134.53 мм; iy=76.45 мм; r=18.00 мм; s=14.50 мм; t=23.00 мм; Вертикальный центроид=158.00 мм; Высота=316.00 мм; Горизонтальный центроид=151.00 мм; Номинальный вес=142.00 килограмм-сила/м; Носок полки сопряжения=25.25 мм; Носок ребра жесткости сопряжения=41.00 мм; Площадь сечения=180.9 см²; Сопряжение ребра жесткости=18.00 мм; Толщина полки=23.00 мм; Толщина ребра жесткости=14.50 мм; Чистая высота ребра жесткости=270.00 мм; Ширина=302.00 мм
- 30К8: ADSK_Масса на единицу длины=161.80 кг/м; Ix=38173.52 см4; Iy=17452.10 см4; Sx=1353.3 см³; Sy=741.5 см³; Wx=2416.1 см³; Wy=977.7 см³; b=357.00 мм; h=316.00 мм; ix=136.08 мм; iy=92.01 мм; r=18.00 мм; s=14.50 мм; t=23.00 мм; Вертикальный центроид=158.00 мм; Высота=316.00 мм; Горизонтальный центроид=178.50 мм; Номинальный вес=161.80 килограмм-сила/м; Носок полки сопряжения=25.25 мм; Носок ребра жесткости сопряжения=41.00 мм; Площадь сечения=206.2 см²; Сопряжение ребра жесткости=18.00 мм; Толщина полки=23.00 мм; Толщина ребра жесткости=14.50 мм; Чистая высота ребра жесткости=270.00 мм; Ширина=357.00 мм
- 30К9: ADSK_Масса на единицу длины=182.20 кг/м; Ix=43983.21 см4; Iy=19896.06 см4; Sx=1541.6 см³; Sy=843.4 см³; Wx=2731.9 см³; Wy=1111.5 см³; b=358.00 мм; h=322.00 мм; ix=137.65 мм; iy=92.58 мм; r=18.00 мм; s=16.00 мм; t=26.00 мм; Вертикальный центроид=161.00 мм; Высота=322.00 мм; Горизонтальный центроид=179.00 мм; Номинальный вес=182.20 килограмм-сила/м; Носок полки сопряжения=26.00 мм; Носок ребра жесткости сопряжения=44.00 мм; Площадь сечения=232.1 см²; Сопряжение ребра жесткости=18.00 мм; Толщина полки=26.00 мм; Толщина ребра жесткости=16.00 мм; Чистая высота ребра жесткости=270.00 мм; Ширина=358.00 мм
- 30К10: ADSK_Масса на единицу длины=203.80 кг/м; Ix=50113.52 см4; Iy=22381.16 см4; Sx=1738.7 см³; Sy=947.1 см³; Wx=3055.7 см³; Wy=1246.9 см³; b=359.00 мм; h=328.00 мм; ix=138.94 мм; iy=92.85 мм; r=18.00 мм; s=18.00 мм; t=29.00 мм; Вертикальный центроид=164.00 мм; Высота=328.00 мм; Горизонтальный центроид=179.50 мм; Номинальный вес=203.80 килограмм-сила/м; Носок полки сопряжения=27.00 мм; Носок ребра жесткости сопряжения=47.00 мм; Площадь сечения=259.6 см²; Сопряжение ребра жесткости=18.00 мм; Толщина полки=29.00 мм; Толщина ребра жесткости=18.00 мм; Чистая высота ребра жесткости=270.00 мм; Ширина=359.00 мм
- 30К11: ADSK_Масса на единицу длины=225.40 кг/м; Ix=56488.07 см4; Iy=24906.98 см4; Sx=1940.0 см³; Sy=1052.3 см³; Wx=3382.5 см³; Wy=1383.7 см³; b=360.00 мм; h=334.00 мм; ix=140.25 мм; iy=93.13 мм; r=18.00 мм; s=20.00 мм; t=32.00 мм; Вертикальный центроид=167.00 мм; Высота=334.00 мм; Горизонтальный центроид=180.00 мм; Номинальный вес=225.40 килограмм-сила/м; Носок полки сопряжения=28.00 мм; Носок ребра жесткости сопряжения=50.00 мм; Площадь сечения=287.2 см²; Сопряжение ребра жесткости=18.00 мм; Толщина полки=32.00 мм; Толщина ребра жесткости=20.00 мм; Чистая высота ребра жесткости=270.00 мм; Ширина=360.00 мм
- 30К12: ADSK_Масса на единицу длины=250.00 кг/м; Ix=64158.87 см4; Iy=27866.03 см4; Sx=2176.3 см³; Sy=1175.0 см³; Wx=3763.0 см³; Wy=1543.8 см³; b=361.00 мм; h=341.00 мм; ix=141.93 мм; iy=93.54 мм; r=18.00 мм; s=22.00 мм; t=35.50 мм; Вертикальный центроид=170.50 мм; Высота=341.00 мм; Горизонтальный центроид=180.50 мм; Номинальный вес=250.00 килограмм-сила/м; Носок полки сопряжения=29.00 мм; Носок ребра жесткости сопряжения=53.50 мм; Площадь сечения=318.5 см²; Сопряжение ребра жесткости=18.00 мм; Толщина полки=35.50 мм; Толщина ребра жесткости=22.00 мм; Чистая высота ребра жесткости=270.00 мм; Ширина=361.00 мм
- 30К13: ADSK_Масса на единицу длины=280.40 кг/м; Ix=74376.59 см4; Iy=31663.84 см4; Sx=2481.3 см³; Sy=1332.1 см³; Wx=4250.1 см³; Wy=1749.4 см³; b=362.00 мм; h=350.00 мм; ix=144.30 мм; iy=94.15 мм; r=18.00 мм; s=24.00 мм; t=40.00 мм; Вертикальный центроид=175.00 мм; Высота=350.00 мм; Горизонтальный центроид=181.00 мм; Номинальный вес=280.40 килограмм-сила/м; Носок полки сопряжения=30.00 мм; Носок ребра жесткости сопряжения=58.00 мм; Площадь сечения=357.2 см²; Сопряжение ребра жесткости=18.00 мм; Толщина полки=40.00 мм; Толщина ребра жесткости=24.00 мм; Чистая высота ребра жесткости=270.00 мм; Ширина=362.00 мм
- 30К14: ADSK_Масса на единицу длины=309.90 кг/м; Ix=83542.72 см4; Iy=36649.59 см4; Sx=2760.9 см³; Sy=1506.7 см³; Wx=4693.4 см³; Wy=1975.7 см³; b=371.00 мм; h=356.00 мм; ix=145.48 мм; iy=96.36 мм; r=18.00 мм; s=27.00 мм; t=43.00 мм; Вертикальный центроид=178.00 мм; Высота=356.00 мм; Горизонтальный центроид=185.50 мм; Номинальный вес=309.90 килограмм-сила/м; Носок полки сопряжения=31.50 мм; Носок ребра жесткости сопряжения=61.00 мм; Площадь сечения=394.7 см²; Сопряжение ребра жесткости=18.00 мм; Толщина полки=43.00 мм; Толщина ребра жесткости=27.00 мм; Чистая высота ребра жесткости=270.00 мм; Ширина=371.00 мм
- 30К15: ADSK_Масса на единицу длины=340.30 кг/м; Ix=93889.39 см4; Iy=40396.23 см4; Sx=3062.8 см³; Sy=1659.0 см³; Wx=5158.8 см³; Wy=2171.8 см³; b=372.00 мм; h=364.00 мм; ix=147.17 мм; iy=96.54 мм; r=18.00 мм; s=30.00 мм; t=47.00 мм; Вертикальный центроид=182.00 мм; Высота=364.00 мм; Горизонтальный центроид=186.00 мм; Номинальный вес=340.30 килограмм-сила/м; Носок полки сопряжения=33.00 мм; Носок ребра жесткости сопряжения=65.00 мм; Площадь сечения=433.5 см²; Сопряжение ребра жесткости=18.00 мм; Толщина полки=47.00 мм; Толщина ребра жесткости=30.00 мм; Чистая высота ребра жесткости=270.00 мм; Ширина=372.00 мм
- 30К16: ADSK_Масса на единицу длины=376.60 кг/м; Ix=107317.14 см4; Iy=45068.65 см4; Sx=3441.7 см³; Sy=1848.3 см³; Wx=5738.9 см³; Wy=2416.6 см³; b=373.00 мм; h=374.00 мм; ix=149.56 мм; iy=96.92 мм; r=18.00 мм; s=33.00 мм; t=52.00 мм; Вертикальный центроид=187.00 мм; Высота=374.00 мм; Горизонтальный центроид=186.50 мм; Номинальный вес=376.60 килограмм-сила/м; Носок полки сопряжения=34.50 мм; Носок ребра жесткости сопряжения=70.00 мм; Площадь сечения=479.8 см²; Сопряжение ребра жесткости=18.00 мм; Толщина полки=52.00 мм; Толщина ребра жесткости=33.00 мм; Чистая высота ребра жесткости=270.00 мм; Ширина=373.00 мм
- 30К17: ADSK_Масса на единицу длины=413.20 кг/м; Ix=121512.35 см4; Iy=49816.72 см4; Sx=3831.8 см³; Sy=2040.0 см³; Wx=6328.8 см³; Wy=2664.0 см³; b=374.00 мм; h=384.00 мм; ix=151.94 мм; iy=97.29 мм; r=18.00 мм; s=36.00 мм; t=57.00 мм; Вертикальный центроид=192.00 мм; Высота=384.00 мм; Горизонтальный центроид=187.00 мм; Номинальный вес=413.20 килограмм-сила/м; Носок полки сопряжения=36.00 мм; Носок ребра жесткости сопряжения=75.00 мм; Площадь сечения=526.3 см²; Сопряжение ребра жесткости=18.00 мм; Толщина полки=57.00 мм; Толщина ребра жесткости=36.00 мм; Чистая высота ребра жесткости=270.00 мм; Ширина=374.00 мм
- 30К18: ADSK_Масса на единицу длины=455.80 кг/м; Ix=139424.86 см4; Iy=55520.26 см4; Sx=4307.2 см³; Sy=2269.5 см³; Wx=7041.7 см³; Wy=2961.1 см³; b=375.00 мм; h=396.00 мм; ix=154.97 мм; iy=97.79 мм; r=18.00 мм; s=39.00 мм; t=63.00 мм; Вертикальный центроид=198.00 мм; Высота=396.00 мм; Горизонтальный центроид=187.50 мм; Номинальный вес=455.80 килограмм-сила/м; Носок полки сопряжения=37.50 мм; Носок ребра жесткости сопряжения=81.00 мм; Площадь сечения=580.6 см²; Сопряжение ребра жесткости=18.00 мм; Толщина полки=63.00 мм; Толщина ребра жесткости=39.00 мм; Чистая высота ребра жесткости=270.00 мм; Ширина=375.00 мм
- 30К19: ADSK_Масса на единицу длины=510.40 кг/м; Ix=162282.28 см4; Iy=65823.94 см4; Sx=4912.8 см³; Sy=2622.8 см³; Wx=7955.0 см³; Wy=3419.4 см³; b=385.00 мм; h=408.00 мм; ix=157.99 мм; iy=100.62 мм; r=18.00 мм; s=43.00 мм; t=69.00 мм; Вертикальный центроид=204.00 мм; Высота=408.00 мм; Горизонтальный центроид=192.50 мм; Номинальный вес=510.40 килограмм-сила/м; Носок полки сопряжения=39.50 мм; Носок ребра жесткости сопряжения=87.00 мм; Площадь сечения=650.2 см²; Сопряжение ребра жесткости=18.00 мм; Толщина полки=69.00 мм; Толщина ребра жесткости=43.00 мм; Чистая высота ребра жесткости=270.00 мм; Ширина=385.00 мм
- 30К20: ADSK_Масса на единицу длины=563.60 кг/м; Ix=187072.37 см4; Iy=73671.75 см4; Sx=5534.8 см³; Sy=2924.0 см³; Wx=8866.0 см³; Wy=3807.3 см³; b=387.00 мм; h=422.00 мм; ix=161.42 мм; iy=101.30 мм; r=18.00 мм; s=47.00 мм; t=76.00 мм; Вертикальный центроид=211.00 мм; Высота=422.00 мм; Горизонтальный центроид=193.50 мм; Номинальный вес=563.60 килограмм-сила/м; Носок полки сопряжения=41.50 мм; Носок ребра жесткости сопряжения=94.00 мм; Площадь сечения=717.9 см²; Сопряжение ребра жесткости=18.00 мм; Толщина полки=76.00 мм; Толщина ребра жесткости=47.00 мм; Чистая высота ребра жесткости=270.00 мм; Ширина=387.00 мм
- 30К21: ADSK_Масса на единицу длины=631.50 кг/м; Ix=221339.16 см4; Iy=83732.23 см4; Sx=6361.1 см³; Sy=3311.0 см³; Wx=10060.9 см³; Wy=4305.0 см³; b=389.00 мм; h=440.00 мм; ix=165.87 мм; iy=102.02 мм; r=18.00 мм; s=52.00 мм; t=85.00 мм; Вертикальный центроид=220.00 мм; Высота=440.00 мм; Горизонтальный центроид=194.50 мм; Номинальный вес=631.50 килограмм-сила/м; Носок полки сопряжения=44.00 мм; Носок ребра жесткости сопряжения=103.00 мм; Площадь сечения=804.5 см²; Сопряжение ребра жесткости=18.00 мм; Толщина полки=85.00 мм; Толщина ребра жесткости=52.00 мм; Чистая высота ребра жесткости=270.00 мм; Ширина=389.00 мм
- 35К1: ADSK_Масса на единицу длины=109.10 кг/м; Ix=31247.91 см4; Iy=10542.21 см4; Sx=1001.2 см³; Sy=459.7 см³; Wx=1827.4 см³; Wy=605.9 см³; b=348.00 мм; h=342.00 мм; ix=149.92 мм; iy=87.08 мм; r=20.00 мм; s=10.00 мм; t=15.00 мм; Вертикальный центроид=171.00 мм; Высота=342.00 мм; Горизонтальный центроид=174.00 мм; Номинальный вес=109.10 килограмм-сила/м; Носок полки сопряжения=25.00 мм; Носок ребра жесткости сопряжения=35.00 мм; Площадь сечения=139.0 см²; Сопряжение ребра жесткости=20.00 мм; Толщина полки=15.00 мм; Толщина ребра жесткости=10.00 мм; Чистая высота ребра жесткости=312.00 мм; Ширина=348.00 мм
- 35К1.5: ADSK_Масса на единицу длины=122.80 кг/м; Ix=35711.23 см4; Iy=12051.44 см4; Sx=1135.8 см³; Sy=524.1 см³; Wx=2064.2 см³; Wy=690.6 см³; b=349.00 мм; h=346.00 мм; ix=151.10 мм; iy=87.78 мм; r=20.00 мм; s=11.00 мм; t=17.00 мм; Вертикальный центроид=173.00 мм; Высота=346.00 мм; Горизонтальный центроид=174.50 мм; Номинальный вес=122.80 килограмм-сила/м; Носок полки сопряжения=25.50 мм; Носок ребра жесткости сопряжения=37.00 мм; Площадь сечения=156.4 см²; Сопряжение ребра жесткости=20.00 мм; Толщина полки=17.00 мм; Толщина ребра жесткости=11.00 мм; Чистая высота ребра жесткости=312.00 мм; Ширина=349.00 мм
- 35К2: ADSK_Масса на единицу длины=136.50 кг/м; Ix=40295.09 см4; Iy=13585.82 см4; Sx=1272.6 см³; Sy=589.3 см³; Wx=2302.6 см³; Wy=776.3 см³; b=350.00 мм; h=350.00 мм; ix=152.23 мм; iy=88.39 мм; r=20.00 мм; s=12.00 мм; t=19.00 мм; Вертикальный центроид=175.00 мм; Высота=350.00 мм; Горизонтальный центроид=175.00 мм; Номинальный вес=136.50 килограмм-сила/м; Носок полки сопряжения=26.00 мм; Носок ребра жесткости сопряжения=39.00 мм; Площадь сечения=173.9 см²; Сопряжение ребра жесткости=20.00 мм; Толщина полки=19.00 мм; Толщина ребра жесткости=12.00 мм; Чистая высота ребра жесткости=312.00 мм; Ширина=350.00 мм
- 35К3: ADSK_Масса на единицу длины=154.20 кг/м; Ix=46230.77 см4; Iy=15506.81 см4; Sx=1448.7 см³; Sy=671.2 см³; Wx=2604.6 см³; Wy=883.6 см³; b=351.00 мм; h=355.00 мм; ix=153.39 мм; iy=88.84 мм; r=20.00 мм; s=13.50 мм; t=21.50 мм; Вертикальный центроид=177.50 мм; Высота=355.00 мм; Горизонтальный центроид=175.50 мм; Номинальный вес=154.20 килограмм-сила/м; Носок полки сопряжения=26.75 мм; Носок ребра жесткости сопряжения=41.50 мм; Площадь сечения=196.5 см²; Сопряжение ребра жесткости=20.00 мм; Толщина полки=21.50 мм; Толщина ребра жесткости=13.50 мм; Чистая высота ребра жесткости=312.00 мм; Ширина=351.00 мм
- 35К4: ADSK_Масса на единицу длины=172.10 кг/м; Ix=52353.70 см4; Iy=17459.86 см4; Sx=1627.8 см³; Sy=754.3 см³; Wx=2908.5 см³; Wy=992.0 см³; b=352.00 мм; h=360.00 мм; ix=154.55 мм; iy=89.25 мм; r=20.00 мм; s=15.00 мм; t=24.00 мм; Вертикальный центроид=180.00 мм; Высота=360.00 мм; Горизонтальный центроид=176.00 мм; Номинальный вес=172.10 килограмм-сила/м; Носок полки сопряжения=27.50 мм; Носок ребра жесткости сопряжения=44.00 мм; Площадь сечения=219.2 см²; Сопряжение ребра жесткости=20.00 мм; Толщина полки=24.00 мм; Толщина ребра жесткости=15.00 мм; Чистая высота ребра жесткости=312.00 мм; Ширина=352.00 мм
- 35К5: ADSK_Масса на единицу длины=190.00 кг/м; Ix=58667.44 см4; Iy=19445.30 см4; Sx=1810.0 см³; Sy=838.3 см³; Wx=3214.7 см³; Wy=1101.7 см³; b=353.00 мм; h=365.00 мм; ix=155.70 мм; iy=89.64 мм; r=20.00 мм; s=16.50 мм; t=26.50 мм; Вертикальный центроид=182.50 мм; Высота=365.00 мм; Горизонтальный центроид=176.50 мм; Номинальный вес=190.00 килограмм-сила/м; Носок полки сопряжения=28.25 мм; Носок ребра жесткости сопряжения=46.50 мм; Площадь сечения=242.0 см²; Сопряжение ребра жесткости=20.00 мм; Толщина полки=26.50 мм; Толщина ребра жесткости=16.50 мм; Чистая высота ребра жесткости=312.00 мм; Ширина=353.00 мм
- 35К6: ADSK_Масса на единицу длины=207.90 кг/м; Ix=64960.86 см4; Iy=22183.47 см4; Sx=1991.8 см³; Sy=938.4 см³; Wx=3520.9 см³; Wy=1232.4 см³; b=360.00 мм; h=369.00 мм; ix=156.63 мм; iy=91.53 мм; r=20.00 мм; s=18.00 мм; t=28.50 мм; Вертикальный центроид=184.50 мм; Высота=369.00 мм; Горизонтальный центроид=180.00 мм; Номинальный вес=207.90 килограмм-сила/м; Носок полки сопряжения=29.00 мм; Носок ребра жесткости сопряжения=48.50 мм; Площадь сечения=264.8 см²; Сопряжение ребра жесткости=20.00 мм; Толщина полки=28.50 мм; Толщина ребра жесткости=18.00 мм; Чистая высота ребра жесткости=312.00 мм; Ширина=360.00 мм
- 35К7: ADSK_Масса на единицу длины=233.10 кг/м; Ix=74398.83 см4; Iy=25119.61 см4; Sx=2256.3 см³; Sy=1060.7 см³; Wx=3957.4 см³; Wy=1391.7 см³; b=361.00 мм; h=376.00 мм; ix=158.31 мм; iy=91.99 мм; r=20.00 мм; s=20.00 мм; t=32.00 мм; Вертикальный центроид=188.00 мм; Высота=376.00 мм; Горизонтальный центроид=180.50 мм; Номинальный вес=233.10 килограмм-сила/м; Носок полки сопряжения=30.00 мм; Носок ребра жесткости сопряжения=52.00 мм; Площадь сечения=296.9 см²; Сопряжение ребра жесткости=20.00 мм; Толщина полки=32.00 мм; Толщина ребра жесткости=20.00 мм; Чистая высота ребра жесткости=312.00 мм; Ширина=361.00 мм
- 35К8: ADSK_Масса на единицу длины=255.50 кг/м; Ix=82894.78 см4; Iy=27708.51 см4; Sx=2492.0 см³; Sy=1168.2 см³; Wx=4340.0 см³; Wy=1530.9 см³; b=362.00 мм; h=382.00 мм; ix=159.59 мм; iy=92.27 мм; r=20.00 мм; s=22.00 мм; t=35.00 мм; Вертикальный центроид=191.00 мм; Высота=382.00 мм; Горизонтальный центроид=181.00 мм; Номинальный вес=255.50 килограмм-сила/м; Носок полки сопряжения=31.00 мм; Носок ребра жесткости сопряжения=55.00 мм; Площадь сечения=325.5 см²; Сопряжение ребра жесткости=20.00 мм; Толщина полки=35.00 мм; Толщина ребра жесткости=22.00 мм; Чистая высота ребра жесткости=312.00 мм; Ширина=362.00 мм
- 35К9: ADSK_Масса на единицу длины=280.90 кг/м; Ix=93053.12 см4; Iy=30738.03 см4; Sx=2767.3 см³; Sy=1293.6 см³; Wx=4784.2 см³; Wy=1693.6 см³; b=363.00 мм; h=389.00 мм; ix=161.26 мм; iy=92.68 мм; r=20.00 мм; s=24.00 мм; t=38.50 мм; Вертикальный центроид=194.50 мм; Высота=389.00 мм; Горизонтальный центроид=181.50 мм; Номинальный вес=280.90 килограмм-сила/м; Носок полки сопряжения=32.00 мм; Носок ребра жесткости сопряжения=58.50 мм; Площадь сечения=357.8 см²; Сопряжение ребра жесткости=20.00 мм; Толщина полки=38.50 мм; Толщина ребра жесткости=24.00 мм; Чистая высота ребра жесткости=312.00 мм; Ширина=363.00 мм
- 35К10: ADSK_Масса на единицу длины=307.60 кг/м; Ix=103736.94 см4; Iy=33819.63 см4; Sx=3054.4 см³; Sy=1421.6 см³; Wx=5239.2 см³; Wy=1858.2 см³; b=364.00 мм; h=396.00 мм; ix=162.70 мм; iy=92.90 мм; r=20.00 мм; s=26.50 мм; t=42.00 мм; Вертикальный центроид=198.00 мм; Высота=396.00 мм; Горизонтальный центроид=182.00 мм; Номинальный вес=307.60 килограмм-сила/м; Носок полки сопряжения=33.25 мм; Носок ребра жесткости сопряжения=62.00 мм; Площадь сечения=391.9 см²; Сопряжение ребра жесткости=20.00 мм; Толщина полки=42.00 мм; Толщина ребра жесткости=26.50 мм; Чистая высота ребра жесткости=312.00 мм; Ширина=364.00 мм
- 35К11: ADSK_Масса на единицу длины=343.80 кг/м; Ix=118982.06 см4; Iy=40183.36 см4; Sx=3458.4 см³; Sy=1644.6 см³; Wx=5890.2 см³; Wy=2148.8 см³; b=374.00 мм; h=404.00 мм; ix=164.82 мм; iy=95.78 мм; r=20.00 мм; s=29.00 мм; t=46.00 мм; Вертикальный центроид=202.00 мм; Высота=404.00 мм; Горизонтальный центроид=187.00 мм; Номинальный вес=343.80 килограмм-сила/м; Носок полки сопряжения=34.50 мм; Носок ребра жесткости сопряжения=66.00 мм; Площадь сечения=438.0 см²; Сопряжение ребра жесткости=20.00 мм; Толщина полки=46.00 мм; Толщина ребра жесткости=29.00 мм; Чистая высота ребра жесткости=312.00 мм; Ширина=374.00 мм
- 35К12: ADSK_Масса на единицу длины=381.30 кг/м; Ix=135721.11 см4; Iy=44924.28 см4; Sx=3886.6 см³; Sy=1836.4 см³; Wx=6556.6 см³; Wy=2396.0 см³; b=375.00 мм; h=414.00 мм; ix=167.15 мм; iy=96.17 мм; r=20.00 мм; s=32.00 мм; t=51.00 мм; Вертикальный центроид=207.00 мм; Высота=414.00 мм; Горизонтальный центроид=187.50 мм; Номинальный вес=381.30 килограмм-сила/м; Носок полки сопряжения=36.00 мм; Носок ребра жесткости сопряжения=71.00 мм; Площадь сечения=485.8 см²; Сопряжение ребра жесткости=20.00 мм; Толщина полки=51.00 мм; Толщина ребра жесткости=32.00 мм; Чистая высота ребра жесткости=312.00 мм; Ширина=375.00 мм
- 35К13: ADSK_Масса на единицу длины=419.00 кг/м; Ix=153322.14 см4; Iy=49742.08 см4; Sx=4326.2 см³; Sy=2030.8 см³; Wx=7232.2 см³; Wy=2645.9 см³; b=376.00 мм; h=424.00 мм; ix=169.49 мм; iy=96.54 мм; r=20.00 мм; s=35.00 мм; t=56.00 мм; Вертикальный центроид=212.00 мм; Высота=424.00 мм; Горизонтальный центроид=188.00 мм; Номинальный вес=419.00 килограмм-сила/м; Носок полки сопряжения=37.50 мм; Носок ребра жесткости сопряжения=76.00 мм; Площадь сечения=533.8 см²; Сопряжение ребра жесткости=20.00 мм; Толщина полки=56.00 мм; Толщина ребра жесткости=35.00 мм; Чистая высота ребра жесткости=312.00 мм; Ширина=376.00 мм
- 35К14: ADSK_Масса на единицу длины=456.80 кг/м; Ix=171810.18 см4; Iy=54637.74 см4; Sx=4777.3 см³; Sy=2227.8 см³; Wx=7917.5 см³; Wy=2898.6 см³; b=377.00 мм; h=434.00 мм; ix=171.83 мм; iy=96.90 мм; r=20.00 мм; s=38.00 мм; t=61.00 мм; Вертикальный центроид=217.00 мм; Высота=434.00 мм; Горизонтальный центроид=188.50 мм; Номинальный вес=456.80 килограмм-сила/м; Носок полки сопряжения=39.00 мм; Носок ребра жесткости сопряжения=81.00 мм; Площадь сечения=581.9 см²; Сопряжение ребра жесткости=20.00 мм; Толщина полки=61.00 мм; Толщина ребра жесткости=38.00 мм; Чистая высота ребра жесткости=312.00 мм; Ширина=377.00 мм
- 35К15: ADSK_Масса на единицу длины=503.20 кг/м; Ix=195206.29 см4; Iy=60526.72 см4; Sx=5336.4 см³; Sy=2466.5 см³; Wx=8753.7 см³; Wy=3202.5 см³; b=378.00 мм; h=446.00 мм; ix=174.51 мм; iy=97.17 мм; r=20.00 мм; s=42.00 мм; t=67.00 мм; Вертикальный центроид=223.00 мм; Высота=446.00 мм; Горизонтальный центроид=189.00 мм; Номинальный вес=503.20 килограмм-сила/м; Носок полки сопряжения=41.00 мм; Носок ребра жесткости сопряжения=87.00 мм; Площадь сечения=641.0 см²; Сопряжение ребра жесткости=20.00 мм; Толщина полки=67.00 мм; Толщина ребра жесткости=42.00 мм; Чистая высота ребра жесткости=312.00 мм; Ширина=378.00 мм
- 35К16: ADSK_Масса на единицу длины=564.60 кг/м; Ix=227053.17 см4; Iy=73566.95 см4; Sx=6094.3 см³; Sy=2891.6 см³; Wx=9915.0 см³; Wy=3753.4 см³; b=392.00 мм; h=458.00 мм; ix=177.67 мм; iy=101.13 мм; r=20.00 мм; s=46.00 мм; t=73.00 мм; Вертикальный центроид=229.00 мм; Высота=458.00 мм; Горизонтальный центроид=196.00 мм; Номинальный вес=564.60 килограмм-сила/м; Носок полки сопряжения=43.00 мм; Носок ребра жесткости сопряжения=93.00 мм; Площадь сечения=719.3 см²; Сопряжение ребра жесткости=20.00 мм; Толщина полки=73.00 мм; Толщина ребра жесткости=46.00 мм; Чистая высота ребра жесткости=312.00 мм; Ширина=392.00 мм
- 35К17: ADSK_Масса на единицу длины=618.80 кг/м; Ix=258357.05 см4; Iy=81286.57 см4; Sx=6796.7 см³; Sy=3191.5 см³; Wx=10947.3 см³; Wy=4136.7 см³; b=393.00 мм; h=472.00 мм; ix=181.04 мм; iy=101.55 мм; r=20.00 мм; s=50.00 мм; t=80.00 мм; Вертикальный центроид=236.00 мм; Высота=472.00 мм; Горизонтальный центроид=196.50 мм; Номинальный вес=618.80 килограмм-сила/м; Носок полки сопряжения=45.00 мм; Носок ребра жесткости сопряжения=100.00 мм; Площадь сечения=788.2 см²; Сопряжение ребра жесткости=20.00 мм; Толщина полки=80.00 мм; Толщина ребра жесткости=50.00 мм; Чистая высота ребра жесткости=312.00 мм; Ширина=393.00 мм
- 35К18: ADSK_Масса на единицу длины=681.80 кг/м; Ix=296560.11 см4; Iy=90173.86 см4; Sx=7629.7 см³; Sy=3538.7 см³; Wx=12154.1 см³; Wy=4577.4 см³; b=394.00 мм; h=488.00 мм; ix=184.79 мм; iy=101.90 мм; r=20.00 мм; s=55.00 мм; t=88.00 мм; Вертикальный центроид=244.00 мм; Высота=488.00 мм; Горизонтальный центроид=197.00 мм; Номинальный вес=681.80 килограмм-сила/м; Носок полки сопряжения=47.50 мм; Носок ребра жесткости сопряжения=108.00 мм; Площадь сечения=868.5 см²; Сопряжение ребра жесткости=20.00 мм; Толщина полки=88.00 мм; Толщина ребра жесткости=55.00 мм; Чистая высота ребра жесткости=312.00 мм; Ширина=394.00 мм
- 35К19: ADSK_Масса на единицу длины=751.20 кг/м; Ix=342451.59 см4; Iy=100237.84 см4; Sx=8591.5 см³; Sy=3929.9 см³; Wx=13535.6 см³; Wy=5075.3 см³; b=395.00 мм; h=506.00 мм; ix=189.17 мм; iy=102.35 мм; r=20.00 мм; s=60.00 мм; t=97.00 мм; Вертикальный центроид=253.00 мм; Высота=506.00 мм; Горизонтальный центроид=197.50 мм; Номинальный вес=751.20 килограмм-сила/м; Носок полки сопряжения=50.00 мм; Носок ребра жесткости сопряжения=117.00 мм; Площадь сечения=956.9 см²; Сопряжение ребра жесткости=20.00 мм; Толщина полки=97.00 мм; Толщина ребра жесткости=60.00 мм; Чистая высота ребра жесткости=312.00 мм; Ширина=395.00 мм
- 35К20: ADSK_Масса на единицу длины=829.70 кг/м; Ix=392963.38 см4; Iy=119352.51 см4; Sx=9664.4 см³; Sy=4520.4 см³; Wx=15114.0 см³; Wy=5836.3 см³; b=409.00 мм; h=520.00 мм; ix=192.82 мм; iy=106.26 мм; r=20.00 мм; s=65.00 мм; t=104.00 мм; Вертикальный центроид=260.00 мм; Высота=520.00 мм; Горизонтальный центроид=204.50 мм; Номинальный вес=829.70 килограмм-сила/м; Носок полки сопряжения=52.50 мм; Носок ребра жесткости сопряжения=124.00 мм; Площадь сечения=1057.0 см²; Сопряжение ребра жесткости=20.00 мм; Толщина полки=104.00 мм; Толщина ребра жесткости=65.00 мм; Чистая высота ребра жесткости=312.00 мм; Ширина=409.00 мм
- 35К21: ADSK_Масса на единицу длины=912.20 кг/м; Ix=454051.02 см4; Iy=132896.31 см4; Sx=10869.9 см³; Sy=5017.7 см³; Wx=16816.7 см³; Wy=6467.0 см³; b=411.00 мм; h=540.00 мм; ix=197.67 мм; iy=106.94 мм; r=20.00 мм; s=71.00 мм; t=114.00 мм; Вертикальный центроид=270.00 мм; Высота=540.00 мм; Горизонтальный центроид=205.50 мм; Номинальный вес=912.20 килограмм-сила/м; Носок полки сопряжения=55.50 мм; Носок ребра жесткости сопряжения=134.00 мм; Площадь сечения=1162.0 см²; Сопряжение ребра жесткости=20.00 мм; Толщина полки=114.00 мм; Толщина ребра жесткости=71.00 мм; Чистая высота ребра жесткости=312.00 мм; Ширина=411.00 мм
- 35К22: ADSK_Масса на единицу длины=1001.80 кг/м; Ix=526659.93 см4; Iy=148011.27 см4; Sx=12243.0 см³; Sy=5568.9 см³; Wx=18742.4 см³; Wy=7167.6 см³; b=413.00 мм; h=562.00 мм; ix=203.15 мм; iy=107.69 мм; r=20.00 мм; s=77.00 мм; t=125.00 мм; Вертикальный центроид=281.00 мм; Высота=562.00 мм; Горизонтальный центроид=206.50 мм; Номинальный вес=1001.80 килограмм-сила/м; Носок полки сопряжения=58.50 мм; Носок ребра жесткости сопряжения=145.00 мм; Площадь сечения=1276.2 см²; Сопряжение ребра жесткости=20.00 мм; Толщина полки=125.00 мм; Толщина ребра жесткости=77.00 мм; Чистая высота ребра жесткости=312.00 мм; Ширина=413.00 мм
- 35К23: ADSK_Масса на единицу длины=1104.70 кг/м; Ix=606878.23 см4; Iy=174271.92 см4; Sx=13777.9 см³; Sy=6362.6 см³; Wx=20926.8 см³; Wy=8181.8 см³; b=426.00 мм; h=580.00 мм; ix=207.67 мм; iy=111.29 мм; r=20.00 мм; s=84.00 мм; t=134.00 мм; Вертикальный центроид=290.00 мм; Высота=580.00 мм; Горизонтальный центроид=213.00 мм; Номинальный вес=1104.70 килограмм-сила/м; Носок полки сопряжения=62.00 мм; Носок ребра жесткости сопряжения=154.00 мм; Площадь сечения=1407.2 см²; Сопряжение ребра жесткости=20.00 мм; Толщина полки=134.00 мм; Толщина ребра жесткости=84.00 мм; Чистая высота ребра жесткости=312.00 мм; Ширина=426.00 мм
- 35К24: ADSK_Масса на единицу длины=1213.70 кг/м; Ix=704826.44 см4; Iy=195579.56 см4; Sx=15522.1 см³; Sy=7087.6 см³; Wx=23338.6 см³; Wy=9096.7 см³; b=430.00 мм; h=604.00 мм; ix=213.51 мм; iy=112.47 мм; r=20.00 мм; s=92.00 мм; t=146.00 мм; Вертикальный центроид=302.00 мм; Высота=604.00 мм; Горизонтальный центроид=215.00 мм; Номинальный вес=1213.70 килограмм-сила/м; Носок полки сопряжения=66.00 мм; Носок ребра жесткости сопряжения=166.00 мм; Площадь сечения=1546.1 см²; Сопряжение ребра жесткости=20.00 мм; Толщина полки=146.00 мм; Толщина ребра жесткости=92.00 мм; Чистая высота ребра жесткости=312.00 мм; Ширина=430.00 мм
- 40К1: ADSK_Масса на единицу длины=146.70 кг/м; Ix=56145.31 см4; Iy=18922.62 см4; Sx=1559.2 см³; Sy=720.4 см³; Wx=2850.0 см³; Wy=950.9 см³; b=398.00 мм; h=394.00 мм; ix=173.36 мм; iy=100.64 мм; r=22.00 мм; s=11.00 мм; t=18.00 мм; Вертикальный центроид=197.00 мм; Высота=394.00 мм; Горизонтальный центроид=199.00 мм; Номинальный вес=146.70 килограмм-сила/м; Носок полки сопряжения=27.50 мм; Носок ребра жесткости сопряжения=40.00 мм; Площадь сечения=186.8 см²; Сопряжение ребра жесткости=22.00 мм; Толщина полки=18.00 мм; Толщина ребра жесткости=11.00 мм; Чистая высота ребра жесткости=358.00 мм; Ширина=398.00 мм
- 40К2: ADSK_Масса на единицу длины=171.70 кг/м; Ix=66621.41 см4; Iy=22412.67 см4; Sx=1836.2 см³; Sy=849.9 см³; Wx=3331.1 см³; Wy=1120.6 см³; b=400.00 мм; h=400.00 мм; ix=174.54 мм; iy=101.23 мм; r=22.00 мм; s=13.00 мм; t=21.00 мм; Вертикальный центроид=200.00 мм; Высота=400.00 мм; Горизонтальный центроид=200.00 мм; Номинальный вес=171.70 килограмм-сила/м; Носок полки сопряжения=28.50 мм; Носок ребра жесткости сопряжения=43.00 мм; Площадь сечения=218.7 см²; Сопряжение ребра жесткости=22.00 мм; Толщина полки=21.00 мм; Толщина ребра жесткости=13.00 мм; Чистая высота ребра жесткости=358.00 мм; Ширина=400.00 мм
- 40К3: ADSK_Масса на единицу длины=200.10 кг/м; Ix=78039.22 см4; Iy=26200.19 см4; Sx=2139.8 см³; Sy=988.6 см³; Wx=3844.3 см³; Wy=1300.3 см³; b=403.00 мм; h=406.00 мм; ix=174.98 мм; iy=101.39 мм; r=22.00 мм; s=16.00 мм; t=24.00 мм; Вертикальный центроид=203.00 мм; Высота=406.00 мм; Горизонтальный центроид=201.50 мм; Номинальный вес=200.10 килограмм-сила/м; Носок полки сопряжения=30.00 мм; Носок ребра жесткости сопряжения=46.00 мм; Площадь сечения=254.9 см²; Сопряжение ребра жесткости=22.00 мм; Толщина полки=24.00 мм; Толщина ребра жесткости=16.00 мм; Чистая высота ребра жесткости=358.00 мм; Ширина=403.00 мм
- 40К4: ADSK_Масса на единицу длины=231.90 кг/м; Ix=92771.14 см4; Iy=31026.87 см4; Sx=2513.2 см³; Sy=1165.6 см³; Wx=4481.7 см³; Wy=1532.2 см³; b=405.00 мм; h=414.00 мм; ix=177.22 мм; iy=102.49 мм; r=22.00 мм; s=18.00 мм; t=28.00 мм; Вертикальный центроид=207.00 мм; Высота=414.00 мм; Горизонтальный центроид=202.50 мм; Номинальный вес=231.90 килограмм-сила/м; Носок полки сопряжения=31.00 мм; Носок ребра жесткости сопряжения=50.00 мм; Площадь сечения=295.4 см²; Сопряжение ребра жесткости=22.00 мм; Толщина полки=28.00 мм; Толщина ребра жесткости=18.00 мм; Чистая высота ребра жесткости=358.00 мм; Ширина=405.00 мм
- 40К4.5: ADSK_Масса на единицу длины=255.60 кг/м; Ix=103629.70 см4; Iy=33850.08 см4; Sx=2786.5 см³; Sy=1279.7 см³; Wx=4934.8 см³; Wy=1679.9 см³; b=403.00 мм; h=420.00 мм; ix=178.40 мм; iy=101.96 мм; r=22.00 мм; s=20.00 мм; t=31.00 мм; Вертикальный центроид=210.00 мм; Высота=420.00 мм; Горизонтальный центроид=201.50 мм; Номинальный вес=255.60 килограмм-сила/м; Носок полки сопряжения=32.00 мм; Носок ребра жесткости сопряжения=53.00 мм; Площадь сечения=325.6 см²; Сопряжение ребра жесткости=22.00 мм; Толщина полки=31.00 мм; Толщина ребра жесткости=20.00 мм; Чистая высота ребра жесткости=358.00 мм; Ширина=403.00 мм
- 40К5: ADSK_Масса на единицу длины=290.80 кг/м; Ix=120290.27 см4; Iy=37914.87 см4; Sx=3198.5 см³; Sy=1447.1 см³; Wx=5607.9 см³; Wy=1895.7 см³; b=400.00 мм; h=429.00 мм; ix=180.19 мм; iy=101.16 мм; r=22.00 мм; s=23.00 мм; t=35.50 мм; Вертикальный центроид=214.50 мм; Высота=429.00 мм; Горизонтальный центроид=200.00 мм; Номинальный вес=290.80 килограмм-сила/м; Носок полки сопряжения=33.50 мм; Носок ребра жесткости сопряжения=57.50 мм; Площадь сечения=370.5 см²; Сопряжение ребра жесткости=22.00 мм; Толщина полки=35.50 мм; Толщина ребра жесткости=23.00 мм; Чистая высота ребра жесткости=358.00 мм; Ширина=400.00 мм
- 40К6: ADSK_Масса на единицу длины=305.90 кг/м; Ix=128432.35 см4; Iy=33828.59 см4; Sx=3381.9 см³; Sy=1400.6 см³; Wx=5864.5 см³; Wy=1828.6 см³; b=370.00 мм; h=438.00 мм; ix=181.55 мм; iy=93.18 мм; r=22.00 мм; s=25.00 мм; t=40.00 мм; Вертикальный центроид=219.00 мм; Высота=438.00 мм; Горизонтальный центроид=185.00 мм; Номинальный вес=305.90 килограмм-сила/м; Носок полки сопряжения=34.50 мм; Носок ребра жесткости сопряжения=62.00 мм; Площадь сечения=389.7 см²; Сопряжение ребра жесткости=22.00 мм; Толщина полки=40.00 мм; Толщина ребра жесткости=25.00 мм; Чистая высота ребра жесткости=358.00 мм; Ширина=370.00 мм
- 40К7: ADSK_Масса на единицу длины=344.10 кг/м; Ix=148100.16 см4; Iy=38379.67 см4; Sx=3848.8 см³; Sy=1587.5 см³; Wx=6611.6 см³; Wy=2069.0 см³; b=371.00 мм; h=448.00 мм; ix=183.82 мм; iy=93.58 мм; r=22.00 мм; s=28.00 мм; t=45.00 мм; Вертикальный центроид=224.00 мм; Высота=448.00 мм; Горизонтальный центроид=185.50 мм; Номинальный вес=344.10 килограмм-сила/м; Носок полки сопряжения=36.00 мм; Носок ребра жесткости сопряжения=67.00 мм; Площадь сечения=438.3 см²; Сопряжение ребра жесткости=22.00 мм; Толщина полки=45.00 мм; Толщина ребра жесткости=28.00 мм; Чистая высота ребра жесткости=358.00 мм; Ширина=371.00 мм
- 40К8: ADSK_Масса на единицу длины=382.40 кг/м; Ix=168699.38 см4; Iy=43005.94 см4; Sx=4327.2 см³; Sy=1777.1 см³; Wx=7366.8 см³; Wy=2312.2 см³; b=372.00 мм; h=458.00 мм; ix=186.09 мм; iy=93.96 мм; r=22.00 мм; s=31.00 мм; t=50.00 мм; Вертикальный центроид=229.00 мм; Высота=458.00 мм; Горизонтальный центроид=186.00 мм; Номинальный вес=382.40 килограмм-сила/м; Носок полки сопряжения=37.50 мм; Носок ребра жесткости сопряжения=72.00 мм; Площадь сечения=487.1 см²; Сопряжение ребра жесткости=22.00 мм; Толщина полки=50.00 мм; Толщина ребра жесткости=31.00 мм; Чистая высота ребра жесткости=358.00 мм; Ширина=372.00 мм
- 40К9: ADSK_Масса на единицу длины=429.60 кг/м; Ix=194740.01 см4; Iy=48584.93 см4; Sx=4920.7 см³; Sy=2007.3 см³; Wx=8286.8 см³; Wy=2605.1 см³; b=373.00 мм; h=470.00 мм; ix=188.65 мм; iy=94.23 мм; r=22.00 мм; s=35.00 мм; t=56.00 мм; Вертикальный центроид=235.00 мм; Высота=470.00 мм; Горизонтальный центроид=186.50 мм; Номинальный вес=429.60 килограмм-сила/м; Носок полки сопряжения=39.50 мм; Носок ребра жесткости сопряжения=78.00 мм; Площадь сечения=547.2 см²; Сопряжение ребра жесткости=22.00 мм; Толщина полки=56.00 мм; Толщина ребра жесткости=35.00 мм; Чистая высота ребра жесткости=358.00 мм; Ширина=373.00 мм
- 40К10: ADSK_Масса на единицу длины=482.80 кг/м; Ix=226537.95 см4; Iy=55131.74 см4; Sx=5620.8 см³; Sy=2276.2 см³; Wx=9361.1 см³; Wy=2948.2 см³; b=374.00 мм; h=484.00 мм; ix=191.92 мм; iy=94.68 мм; r=22.00 мм; s=39.00 мм; t=63.00 мм; Вертикальный центроид=242.00 мм; Высота=484.00 мм; Горизонтальный центроид=187.00 мм; Номинальный вес=482.80 килограмм-сила/м; Носок полки сопряжения=41.50 мм; Носок ребра жесткости сопряжения=85.00 мм; Площадь сечения=615.0 см²; Сопряжение ребра жесткости=22.00 мм; Толщина полки=63.00 мм; Толщина ребра жесткости=39.00 мм; Чистая высота ребра жесткости=358.00 мм; Ширина=374.00 мм
- 40К11: ADSK_Масса на единицу длины=542.60 кг/м; Ix=261626.63 см4; Iy=68534.68 см4; Sx=6402.8 см³; Sy=2700.5 см³; Wx=10592.2 см³; Wy=3496.7 см³; b=392.00 мм; h=494.00 мм; ix=194.55 мм; iy=99.57 мм; r=22.00 мм; s=43.00 мм; t=68.00 мм; Вертикальный центроид=247.00 мм; Высота=494.00 мм; Горизонтальный центроид=196.00 мм; Номинальный вес=542.60 килограмм-сила/м; Носок полки сопряжения=43.50 мм; Носок ребра жесткости сопряжения=90.00 мм; Площадь сечения=691.2 см²; Сопряжение ребра жесткости=22.00 мм; Толщина полки=68.00 мм; Толщина ребра жесткости=43.00 мм; Чистая высота ребра жесткости=358.00 мм; Ширина=392.00 мм
- 40К12: ADSK_Масса на единицу длины=607.10 кг/м; Ix=303779.05 см4; Iy=77250.09 см4; Sx=7286.5 см³; Sy=3043.6 см³; Wx=11912.9 см³; Wy=3931.3 см³; b=393.00 мм; h=510.00 мм; ix=198.19 мм; iy=99.94 мм; r=22.00 мм; s=48.00 мм; t=76.00 мм; Вертикальный центроид=255.00 мм; Высота=510.00 мм; Горизонтальный центроид=196.50 мм; Номинальный вес=607.10 килограмм-сила/м; Носок полки сопряжения=46.00 мм; Носок ребра жесткости сопряжения=98.00 мм; Площадь сечения=773.4 см²; Сопряжение ребра жесткости=22.00 мм; Толщина полки=76.00 мм; Толщина ребра жесткости=48.00 мм; Чистая высота ребра жесткости=358.00 мм; Ширина=393.00 мм
- 40К13: ADSK_Масса на единицу длины=678.00 кг/м; Ix=354176.39 см4; Iy=87133.42 см4; Sx=8303.3 см³; Sy=3431.0 см³; Wx=13415.8 см³; Wy=4423.0 см³; b=394.00 мм; h=528.00 мм; ix=202.50 мм; iy=100.44 мм; r=22.00 мм; s=53.00 мм; t=85.00 мм; Вертикальный центроид=264.00 мм; Высота=528.00 мм; Горизонтальный центроид=197.00 мм; Номинальный вес=678.00 килограмм-сила/м; Носок полки сопряжения=48.50 мм; Носок ребра жесткости сопряжения=107.00 мм; Площадь сечения=863.7 см²; Сопряжение ребра жесткости=22.00 мм; Толщина полки=85.00 мм; Толщина ребра жесткости=53.00 мм; Чистая высота ребра жесткости=358.00 мм; Ширина=394.00 мм
- 40К14: ADSK_Масса на единицу длины=758.20 кг/м; Ix=414486.60 см4; Iy=98243.26 см4; Sx=9480.8 см³; Sy=3868.5 см³; Wx=15127.3 см³; Wy=4974.3 см³; b=395.00 мм; h=548.00 мм; ix=207.15 мм; iy=100.85 мм; r=22.00 мм; s=59.00 мм; t=95.00 мм; Вертикальный центроид=274.00 мм; Высота=548.00 мм; Горизонтальный центроид=197.50 мм; Номинальный вес=758.20 килограмм-сила/м; Носок полки сопряжения=51.50 мм; Носок ребра жесткости сопряжения=117.00 мм; Площадь сечения=965.9 см²; Сопряжение ребра жесткости=22.00 мм; Толщина полки=95.00 мм; Толщина ребра жесткости=59.00 мм; Чистая высота ребра жесткости=358.00 мм; Ширина=395.00 мм
- 40К15: ADSK_Масса на единицу длины=848.90 кг/м; Ix=482318.02 см4; Iy=119192.55 см4; Sx=10811.5 см³; Sy=4525.4 см³; Wx=17103.5 см³; Wy=5814.3 см³; b=410.00 мм; h=564.00 мм; ix=211.18 мм; iy=104.98 мм; r=22.00 мм; s=65.00 мм; t=103.00 мм; Вертикальный центроид=282.00 мм; Высота=564.00 мм; Горизонтальный центроид=205.00 мм; Номинальный вес=848.90 килограмм-сила/м; Носок полки сопряжения=54.50 мм; Носок ребра жесткости сопряжения=125.00 мм; Площадь сечения=1081.5 см²; Сопряжение ребра жесткости=22.00 мм; Толщина полки=103.00 мм; Толщина ребра жесткости=65.00 мм; Чистая высота ребра жесткости=358.00 мм; Ширина=410.00 мм
- 40К16: ADSK_Масса на единицу длины=949.50 кг/м; Ix=569246.79 см4; Iy=135224.96 см4; Sx=12395.0 см³; Sy=5120.6 см³; Wx=19362.1 см³; Wy=6564.3 см³; b=412.00 мм; h=588.00 мм; ix=216.94 мм; iy=105.74 мм; r=22.00 мм; s=72.00 мм; t=115.00 мм; Вертикальный центроид=294.00 мм; Высота=588.00 мм; Горизонтальный центроид=206.00 мм; Номинальный вес=949.50 килограмм-сила/м; Носок полки сопряжения=58.00 мм; Носок ребра жесткости сопряжения=137.00 мм; Площадь сечения=1209.5 см²; Сопряжение ребра жесткости=22.00 мм; Толщина полки=115.00 мм; Толщина ребра жесткости=72.00 мм; Чистая высота ребра жесткости=358.00 мм; Ширина=412.00 мм
- 40К17: ADSK_Масса на единицу длины=1066.60 кг/м; Ix=679972.83 см4; Iy=154171.56 см4; Sx=14322.2 см³; Sy=5823.3 см³; Wx=22077.0 см³; Wy=7447.9 см³; b=414.00 мм; h=616.00 мм; ix=223.71 мм; iy=106.52 мм; r=22.00 мм; s=80.00 мм; t=129.00 мм; Вертикальный центроид=308.00 мм; Высота=616.00 мм; Горизонтальный центроид=207.00 мм; Номинальный вес=1066.60 килограмм-сила/м; Носок полки сопряжения=62.00 мм; Носок ребра жесткости сопряжения=151.00 мм; Площадь сечения=1358.7 см²; Сопряжение ребра жесткости=22.00 мм; Толщина полки=129.00 мм; Толщина ребра жесткости=80.00 мм; Чистая высота ребра жесткости=358.00 мм; Ширина=414.00 мм
- 40К18: ADSK_Масса на единицу длины=1192.90 кг/м; Ix=800682.16 см4; Iy=187578.96 см4; Sx=16419.8 см³; Sy=6820.3 см³; Wx=25099.8 см³; Wy=8724.6 см³; b=430.00 мм; h=638.00 мм; ix=229.54 мм; iy=111.10 мм; r=22.00 мм; s=87.00 мм; t=140.00 мм; Вертикальный центроид=319.00 мм; Высота=638.00 мм; Горизонтальный центроид=215.00 мм; Номинальный вес=1192.90 килограмм-сила/м; Носок полки сопряжения=65.50 мм; Носок ребра жесткости сопряжения=162.00 мм; Площадь сечения=1519.6 см²; Сопряжение ребра жесткости=22.00 мм; Толщина полки=140.00 мм; Толщина ребра жесткости=87.00 мм; Чистая высота ребра жесткости=358.00 мм; Ширина=430.00 мм
- 40К19: ADSK_Масса на единицу длины=1331.60 кг/м; Ix=952172.58 см4; Iy=215398.09 см4; Sx=18868.6 см³; Sy=7755.9 см³; Wx=28508.2 см³; Wy=9903.4 см³; b=435.00 мм; h=668.00 мм; ix=236.92 мм; iy=112.68 мм; r=22.00 мм; s=96.00 мм; t=155.00 мм; Вертикальный центроид=334.00 мм; Высота=668.00 мм; Горизонтальный центроид=217.50 мм; Номинальный вес=1331.60 килограмм-сила/м; Носок полки сопряжения=70.00 мм; Носок ребра жесткости сопряжения=177.00 мм; Площадь сечения=1696.3 см²; Сопряжение ребра жесткости=22.00 мм; Толщина полки=155.00 мм; Толщина ребра жесткости=96.00 мм; Чистая высота ребра жесткости=358.00 мм; Ширина=435.00 мм
- 13С1: ADSK_Масса на единицу длины=24.74 кг/м; Ix=838.38 см4; Iy=223.59 см4; Sx=76.7 см³; Sy=30.8 см³; Wx=132.6 см³; Wy=39.2 см³; b=114.00 мм; h=126.50 мм; ix=51.57 мм; iy=26.63 мм; r=12.00 мм; s=9.00 мм; t=9.00 мм; Вертикальный центроид=63.25 мм; Высота=126.50 мм; Горизонтальный центроид=57.00 мм; Номинальный вес=24.74 килограмм-сила/м; Носок полки сопряжения=16.50 мм; Носок ребра жесткости сопряжения=21.00 мм; Площадь сечения=31.5 см²; Сопряжение ребра жесткости=12.00 мм; Толщина полки=9.00 мм; Толщина ребра жесткости=9.00 мм; Чистая высота ребра жесткости=108.50 мм; Ширина=114.00 мм
- 20С1: ADSK_Масса на единицу длины=56.20 кг/м; Ix=4982.30 см4; Iy=1701.70 см4; Sx=282.8 см³; Sy=128.7 см³; Wx=498.2 см³; Wy=166.8 см³; b=204.00 мм; h=200.00 мм; ix=83.46 мм; iy=48.77 мм; r=13.00 мм; s=12.00 мм; t=12.00 мм; Вертикальный центроид=100.00 мм; Высота=200.00 мм; Горизонтальный центроид=102.00 мм; Номинальный вес=56.20 килограмм-сила/м; Носок полки сопряжения=19.00 мм; Носок ребра жесткости сопряжения=25.00 мм; Площадь сечения=71.5 см²; Сопряжение ребра жесткости=13.00 мм; Толщина полки=12.00 мм; Толщина ребра жесткости=12.00 мм; Чистая высота ребра жесткости=176.00 мм; Ширина=204.00 мм
- 25С1: ADSK_Масса на единицу длины=64.40 кг/м; Ix=8786.78 см4; Iy=2938.35 см4; Sx=402.5 см³; Sy=179.0 см³; Wx=720.2 см³; Wy=233.2 см³; b=252.00 мм; h=244.00 мм; ix=103.48 мм; iy=59.84 мм; r=16.00 мм; s=11.00 мм; t=11.00 мм; Вертикальный центроид=122.00 мм; Высота=244.00 мм; Горизонтальный центроид=126.00 мм; Номинальный вес=64.40 килограмм-сила/м; Носок полки сопряжения=21.50 мм; Носок ребра жесткости сопряжения=27.00 мм; Площадь сечения=82.1 см²; Сопряжение ребра жесткости=16.00 мм; Толщина полки=11.00 мм; Толщина ребра жесткости=11.00 мм; Чистая высота ребра жесткости=222.00 мм; Ширина=252.00 мм
- 25С2: ADSK_Масса на единицу длины=82.20 кг/м; Ix=11483.65 см4; Iy=3876.72 см4; Sx=519.3 см³; Sy=234.2 см³; Wx=918.7 см³; Wy=304.1 см³; b=255.00 мм; h=250.00 мм; ix=104.74 мм; iy=60.86 мм; r=16.00 мм; s=14.00 мм; t=14.00 мм; Вертикальный центроид=125.00 мм; Высота=250.00 мм; Горизонтальный центроид=127.50 мм; Номинальный вес=82.20 килограмм-сила/м; Носок полки сопряжения=23.00 мм; Носок ребра жесткости сопряжения=30.00 мм; Площадь сечения=104.7 см²; Сопряжение ребра жесткости=16.00 мм; Толщина полки=14.00 мм; Толщина ребра жесткости=14.00 мм; Чистая высота ребра жесткости=222.00 мм; Ширина=255.00 мм
- 30С1: ADSK_Масса на единицу длины=84.50 кг/м; Ix=16864.20 см4; Iy=5515.72 см4; Sx=638.6 см³; Sy=279.9 см³; Wx=1147.2 см³; Wy=365.3 см³; b=302.00 мм; h=294.00 мм; ix=125.16 мм; iy=71.58 мм; r=18.00 мм; s=12.00 мм; t=12.00 мм; Вертикальный центроид=147.00 мм; Высота=294.00 мм; Горизонтальный центроид=151.00 мм; Номинальный вес=84.50 килограмм-сила/м; Носок полки сопряжения=24.00 мм; Носок ребра жесткости сопряжения=30.00 мм; Площадь сечения=107.7 см²; Сопряжение ребра жесткости=18.00 мм; Толщина полки=12.00 мм; Толщина ребра жесткости=12.00 мм; Чистая высота ребра жесткости=270.00 мм; Ширина=302.00 мм
- 30С2: ADSK_Масса на единицу длины=105.80 кг/м; Ix=21535.21 см4; Iy=7104.76 см4; Sx=806.8 см³; Sy=358.0 см³; Wx=1435.7 см³; Wy=465.9 см³; b=305.00 мм; h=300.00 мм; ix=126.40 мм; iy=72.60 мм; r=18.00 мм; s=15.00 мм; t=15.00 мм; Вертикальный центроид=150.00 мм; Высота=300.00 мм; Горизонтальный центроид=152.50 мм; Номинальный вес=105.80 килограмм-сила/м; Носок полки сопряжения=25.50 мм; Носок ребра жесткости сопряжения=33.00 мм; Площадь сечения=134.8 см²; Сопряжение ребра жесткости=18.00 мм; Толщина полки=15.00 мм; Толщина ребра жесткости=15.00 мм; Чистая высота ребра жесткости=270.00 мм; Ширина=305.00 мм
- 32С1: ADSK_Масса на единицу длины=180.00 кг/м; Ix=40972.83 см4; Iy=13546.38 см4; Sx=1448.3 см³; Sy=656.6 см³; Wx=2508.3 см³; Wy=847.4 см³; b=319.70 мм; h=326.70 мм; ix=133.68 мм; iy=76.87 мм; r=15.20 мм; s=24.80 мм; t=24.80 мм; Вертикальный центроид=163.35 мм; Высота=326.70 мм; Горизонтальный центроид=159.85 мм; Номинальный вес=180.00 килограмм-сила/м; Носок полки сопряжения=27.60 мм; Носок ребра жесткости сопряжения=40.00 мм; Площадь сечения=229.3 см²; Сопряжение ребра жесткости=15.20 мм; Толщина полки=24.80 мм; Толщина ребра жесткости=24.80 мм; Чистая высота ребра жесткости=277.10 мм; Ширина=319.70 мм
- 32С2: ADSK_Масса на единицу длины=222.90 кг/м; Ix=52698.77 см4; Iy=17576.76 см4; Sx=1826.6 см³; Sy=839.9 см³; Wx=3119.2 см³; Wy=1079.3 см³; b=325.70 мм; h=337.90 мм; ix=136.23 мм; iy=78.67 мм; r=15.20 мм; s=30.30 мм; t=30.40 мм; Вертикальный центроид=168.95 мм; Высота=337.90 мм; Горизонтальный центроид=162.85 мм; Номинальный вес=222.90 килограмм-сила/м; Носок полки сопряжения=30.35 мм; Носок ребра жесткости сопряжения=45.60 мм; Площадь сечения=284.0 см²; Сопряжение ребра жесткости=15.20 мм; Толщина полки=30.40 мм; Толщина ребра жесткости=30.30 мм; Чистая высота ребра жесткости=277.10 мм; Ширина=325.70 мм
- 35С1: ADSK_Масса на единицу длины=106.20 кг/м; Ix=28190.34 см4; Iy=9379.76 см4; Sx=925.7 см³; Sy=408.9 см³; Wx=1668.1 см³; Wy=534.5 см³; b=351.00 мм; h=338.00 мм; ix=144.37 мм; iy=83.28 мм; r=20.00 мм; s=13.00 мм; t=13.00 мм; Вертикальный центроид=169.00 мм; Высота=338.00 мм; Горизонтальный центроид=175.50 мм; Номинальный вес=106.20 килограмм-сила/м; Носок полки сопряжения=26.50 мм; Носок ребра жесткости сопряжения=33.00 мм; Площадь сечения=135.3 см²; Сопряжение ребра жесткости=20.00 мм; Толщина полки=13.00 мм; Толщина ребра жесткости=13.00 мм; Чистая высота ребра жесткости=312.00 мм; Ширина=351.00 мм
- 35С2: ADSK_Масса на единицу длины=130.80 кг/м; Ix=35330.38 см4; Iy=11846.30 см4; Sx=1149.6 см³; Sy=513.4 см³; Wx=2054.1 см³; Wy=669.3 см³; b=354.00 мм; h=344.00 мм; ix=145.61 мм; iy=84.32 мм; r=20.00 мм; s=16.00 мм; t=16.00 мм; Вертикальный центроид=172.00 мм; Высота=344.00 мм; Горизонтальный центроид=177.00 мм; Номинальный вес=130.80 килограмм-сила/м; Носок полки сопряжения=28.00 мм; Носок ребра жесткости сопряжения=36.00 мм; Площадь сечения=166.6 см²; Сопряжение ребра жесткости=20.00 мм; Толщина полки=16.00 мм; Толщина ребра жесткости=16.00 мм; Чистая высота ребра жесткости=312.00 мм; Ширина=354.00 мм
- 35С3: ADSK_Масса на единицу длины=155.70 кг/м; Ix=42796.14 см4; Iy=14433.12 см4; Sx=1379.8 см³; Sy=621.9 см³; Wx=2445.5 см³; Wy=808.6 см³; b=357.00 мм; h=350.00 мм; ix=146.88 мм; iy=85.30 мм; r=20.00 мм; s=19.00 мм; t=19.00 мм; Вертикальный центроид=175.00 мм; Высота=350.00 мм; Горизонтальный центроид=178.50 мм; Номинальный вес=155.70 килограмм-сила/м; Носок полки сопряжения=29.50 мм; Носок ребра жесткости сопряжения=39.00 мм; Площадь сечения=198.4 см²; Сопряжение ребра жесткости=20.00 мм; Толщина полки=19.00 мм; Толщина ребра жесткости=19.00 мм; Чистая высота ребра жесткости=312.00 мм; Ширина=357.00 мм
- 40С1: ADSK_Масса на единицу длины=140.10 кг/м; Ix=48965.17 см4; Iy=16258.38 см4; Sx=1401.1 см³; Sy=618.7 см³; Wx=2524.0 см³; Wy=808.9 см³; b=402.00 мм; h=388.00 мм; ix=165.65 мм; iy=95.45 мм; r=22.00 мм; s=15.00 мм; t=15.00 мм; Вертикальный центроид=194.00 мм; Высота=388.00 мм; Горизонтальный центроид=201.00 мм; Номинальный вес=140.10 килограмм-сила/м; Носок полки сопряжения=29.50 мм; Носок ребра жесткости сопряжения=37.00 мм; Площадь сечения=178.5 см²; Сопряжение ребра жесткости=22.00 мм; Толщина полки=15.00 мм; Толщина ребра жесткости=15.00 мм; Чистая высота ребра жесткости=358.00 мм; Ширина=402.00 мм
- 40С2: ADSK_Масса на единицу длины=168.30 кг/м; Ix=59713.15 см4; Iy=19955.19 см4; Sx=1695.1 см³; Sy=755.5 см³; Wx=3031.1 см³; Wy=985.4 см³; b=405.00 мм; h=394.00 мм; ix=166.89 мм; iy=96.48 мм; r=22.00 мм; s=18.00 мм; t=18.00 мм; Вертикальный центроид=197.00 мм; Высота=394.00 мм; Горизонтальный центроид=202.50 мм; Номинальный вес=168.30 килограмм-сила/м; Носок полки сопряжения=31.00 мм; Носок ребра жесткости сопряжения=40.00 мм; Площадь сечения=214.4 см²; Сопряжение ребра жесткости=22.00 мм; Толщина полки=18.00 мм; Толщина ребра жесткости=18.00 мм; Чистая высота ребра жесткости=358.00 мм; Ширина=405.00 мм
- 40С3: ADSK_Масса на единицу длины=196.80 кг/м; Ix=70888.08 см4; Iy=23809.27 см4; Sx=1996.2 см³; Sy=896.9 см³; Wx=3544.4 см³; Wy=1167.1 см³; b=408.00 мм; h=400.00 мм; ix=168.16 мм; iy=97.45 мм; r=22.00 мм; s=21.00 мм; t=21.00 мм; Вертикальный центроид=200.00 мм; Высота=400.00 мм; Горизонтальный центроид=204.00 мм; Номинальный вес=196.80 килограмм-сила/м; Носок полки сопряжения=32.50 мм; Носок ребра жесткости сопряжения=43.00 мм; Площадь сечения=250.7 см²; Сопряжение ребра жесткости=22.00 мм; Толщина полки=21.00 мм; Толщина ребра жесткости=21.00 мм; Чистая высота ребра жесткости=358.00 мм; Ширина=408.00 мм
- 20ДБ1: ADSK_Масса на единицу длины=26.60 кг/м; Ix=2580.37 см4; Iy=329.79 см4; Sx=139.5 см³; Sy=38.1 см³; Wx=249.3 см³; Wy=49.6 см³; b=133.00 мм; h=207.00 мм; ix=87.28 мм; iy=31.20 мм; r=7.60 мм; s=5.80 мм; t=8.40 мм; Вертикальный центроид=103.50 мм; Высота=207.00 мм; Горизонтальный центроид=66.50 мм; Номинальный вес=26.60 килограмм-сила/м; Носок полки сопряжения=10.50 мм; Носок ребра жесткости сопряжения=16.00 мм; Площадь сечения=33.9 см²; Сопряжение ребра жесткости=7.60 мм; Толщина полки=8.40 мм; Толщина ребра жесткости=5.80 мм; Чистая высота ребра жесткости=190.20 мм; Ширина=133.00 мм
- 20ДБ2: ADSK_Масса на единицу длины=31.40 кг/м; Ix=3137.00 см4; Iy=409.58 см4; Sx=167.6 см³; Sy=46.9 см³; Wx=298.8 см³; Wy=61.1 см³; b=134.00 мм; h=210.00 мм; ix=88.60 мм; iy=32.01 мм; r=7.60 мм; s=6.40 мм; t=10.20 мм; Вертикальный центроид=105.00 мм; Высота=210.00 мм; Горизонтальный центроид=67.00 мм; Номинальный вес=31.40 килограмм-сила/м; Носок полки сопряжения=10.80 мм; Носок ребра жесткости сопряжения=17.80 мм; Площадь сечения=40.0 см²; Сопряжение ребра жесткости=7.60 мм; Толщина полки=10.20 мм; Толщина ребра жесткости=6.40 мм; Чистая высота ребра жесткости=189.60 мм; Ширина=134.00 мм
- 25ДБ1: ADSK_Масса на единицу длины=31.10 кг/м; Ix=4395.18 см4; Iy=446.61 см4; Sx=196.0 см³; Sy=47.0 см³; Wx=350.2 см³; Wy=61.2 см³; b=146.00 мм; h=251.00 мм; ix=105.30 мм; iy=33.57 мм; r=7.60 мм; s=6.00 мм; t=8.60 мм; Вертикальный центроид=125.50 мм; Высота=251.00 мм; Горизонтальный центроид=73.00 мм; Номинальный вес=31.10 килограмм-сила/м; Носок полки сопряжения=10.60 мм; Носок ребра жесткости сопряжения=16.20 мм; Площадь сечения=39.6 см²; Сопряжение ребра жесткости=7.60 мм; Толщина полки=8.60 мм; Толщина ребра жесткости=6.00 мм; Чистая высота ребра жесткости=233.80 мм; Ширина=146.00 мм
- 25ДБ2: ADSK_Масса на единицу длины=37.00 кг/м; Ix=5523.69 см4; Iy=565.99 см4; Sx=241.1 см³; Sy=59.4 см³; Wx=431.5 см³; Wy=77.5 см³; b=146.00 мм; h=256.00 мм; ix=108.32 мм; iy=34.67 мм; r=7.60 мм; s=6.30 мм; t=10.90 мм; Вертикальный центроид=128.00 мм; Высота=256.00 мм; Горизонтальный центроид=73.00 мм; Номинальный вес=37.00 килограмм-сила/м; Носок полки сопряжения=10.75 мм; Носок ребра жесткости сопряжения=18.50 мм; Площадь сечения=47.1 см²; Сопряжение ребра жесткости=7.60 мм; Толщина полки=10.90 мм; Толщина ребра жесткости=6.30 мм; Чистая высота ребра жесткости=234.20 мм; Ширина=146.00 мм
- 25ДБ3: ADSK_Масса на единицу длины=43.00 кг/м; Ix=6554.72 см4; Iy=673.24 см4; Sx=283.2 см³; Sy=70.3 см³; Wx=504.2 см³; Wy=91.6 см³; b=147.00 мм; h=260.00 мм; ix=109.44 мм; iy=35.07 мм; r=7.60 мм; s=7.20 мм; t=12.70 мм; Вертикальный центроид=130.00 мм; Высота=260.00 мм; Горизонтальный центроид=73.50 мм; Номинальный вес=43.00 килограмм-сила/м; Носок полки сопряжения=11.20 мм; Носок ребра жесткости сопряжения=20.30 мм; Площадь сечения=54.7 см²; Сопряжение ребра жесткости=7.60 мм; Толщина полки=12.70 мм; Толщина ребра жесткости=7.20 мм; Чистая высота ребра жесткости=234.60 мм; Ширина=147.00 мм
- 25ДБ4: ADSK_Масса на единицу длины=32.70 кг/м; Ix=4887.50 см4; Iy=472.58 см4; Sx=212.1 см³; Sy=49.7 см³; Wx=378.9 см³; Wy=64.7 см³; b=146.00 мм; h=258.00 мм; ix=108.27 мм; iy=33.67 мм; r=7.60 мм; s=6.10 мм; t=9.10 мм; Вертикальный центроид=129.00 мм; Высота=258.00 мм; Горизонтальный центроид=73.00 мм; Номинальный вес=32.70 килограмм-сила/м; Носок полки сопряжения=10.65 мм; Носок ребра жесткости сопряжения=16.70 мм; Площадь сечения=41.7 см²; Сопряжение ребра жесткости=7.60 мм; Толщина полки=9.10 мм; Толщина ребра жесткости=6.10 мм; Чистая высота ребра жесткости=239.80 мм; Ширина=146.00 мм
- 25ДБ5: ADSK_Масса на единицу длины=38.70 кг/м; Ix=6007.11 см4; Iy=593.66 см4; Sx=256.8 см³; Sy=61.9 см³; Wx=458.6 см³; Wy=80.8 см³; b=147.00 мм; h=262.00 мм; ix=110.45 мм; iy=34.72 мм; r=7.60 мм; s=6.60 мм; t=11.20 мм; Вертикальный центроид=131.00 мм; Высота=262.00 мм; Горизонтальный центроид=73.50 мм; Номинальный вес=38.70 килограмм-сила/м; Носок полки сопряжения=10.90 мм; Носок ребра жесткости сопряжения=18.80 мм; Площадь сечения=49.2 см²; Сопряжение ребра жесткости=7.60 мм; Толщина полки=11.20 мм; Толщина ребра жесткости=6.60 мм; Чистая высота ребра жесткости=239.60 мм; Ширина=147.00 мм
- 25ДБ6: ADSK_Масса на единицу длины=44.90 кг/м; Ix=7108.01 см4; Iy=703.43 см4; Sx=301.0 см³; Sy=73.1 см³; Wx=534.4 см³; Wy=95.1 см³; b=148.00 мм; h=266.00 мм; ix=111.46 мм; iy=35.06 мм; r=7.60 мм; s=7.60 мм; t=13.00 мм; Вертикальный центроид=133.00 мм; Высота=266.00 мм; Горизонтальный центроид=74.00 мм; Номинальный вес=44.90 килограмм-сила/м; Носок полки сопряжения=11.40 мм; Носок ребра жесткости сопряжения=20.60 мм; Площадь сечения=57.2 см²; Сопряжение ребра жесткости=7.60 мм; Толщина полки=13.00 мм; Толщина ребра жесткости=7.60 мм; Чистая высота ребра жесткости=240.00 мм; Ширина=148.00 мм
- 30ДБ1: ADSK_Масса на единицу длины=28.40 кг/м; Ix=5426.36 см4; Iy=158.06 см4; Sx=203.4 см³; Sy=24.6 см³; Wx=351.2 см³; Wy=31.0 см³; b=102.00 мм; h=309.00 мм; ix=122.56 мм; iy=20.92 мм; r=7.60 мм; s=6.00 мм; t=8.90 мм; Вертикальный центроид=154.50 мм; Высота=309.00 мм; Горизонтальный центроид=51.00 мм; Номинальный вес=28.40 килограмм-сила/м; Носок полки сопряжения=10.60 мм; Носок ребра жесткости сопряжения=16.50 мм; Площадь сечения=36.1 см²; Сопряжение ребра жесткости=7.60 мм; Толщина полки=8.90 мм; Толщина ребра жесткости=6.00 мм; Чистая высота ребра жесткости=291.20 мм; Ширина=102.00 мм
- 30ДБ2: ADSK_Масса на единицу длины=32.80 кг/м; Ix=6496.06 см4; Iy=191.85 см4; Sx=240.1 см³; Sy=29.8 см³; Wx=415.1 см³; Wy=37.6 см³; b=102.00 мм; h=313.00 мм; ix=124.72 мм; iy=21.43 мм; r=7.60 мм; s=6.60 мм; t=10.80 мм; Вертикальный центроид=156.50 мм; Высота=313.00 мм; Горизонтальный центроид=51.00 мм; Номинальный вес=32.80 килограмм-сила/м; Носок полки сопряжения=10.90 мм; Носок ребра жесткости сопряжения=18.40 мм; Площадь сечения=41.8 см²; Сопряжение ребра жесткости=7.60 мм; Толщина полки=10.80 мм; Толщина ребра жесткости=6.60 мм; Чистая высота ребра жесткости=291.40 мм; Ширина=102.00 мм
- 30ДБ3: ADSK_Масса на единицу длины=38.90 кг/м; Ix=8544.97 см4; Iy=726.88 см4; Sx=306.4 см³; Sy=67.4 см³; Wx=551.3 см³; Wy=88.1 см³; b=165.00 мм; h=310.00 мм; ix=131.33 мм; iy=38.30 мм; r=8.90 мм; s=5.80 мм; t=9.70 мм; Вертикальный центроид=155.00 мм; Высота=310.00 мм; Горизонтальный центроид=82.50 мм; Номинальный вес=38.90 килограмм-сила/м; Носок полки сопряжения=11.80 мм; Носок ребра жесткости сопряжения=18.60 мм; Площадь сечения=49.5 см²; Сопряжение ребра жесткости=8.90 мм; Толщина полки=9.70 мм; Толщина ребра жесткости=5.80 мм; Чистая высота ребра жесткости=290.60 мм; Ширина=165.00 мм
- 30ДБ4: ADSK_Масса на единицу длины=44.80 кг/м; Ix=9960.39 см4; Iy=854.77 см4; Sx=355.1 см³; Sy=78.9 см³; Wx=636.5 см³; Wy=103.0 см³; b=166.00 мм; h=313.00 мм; ix=132.14 мм; iy=38.71 мм; r=8.90 мм; s=6.60 мм; t=11.20 мм; Вертикальный центроид=156.50 мм; Высота=313.00 мм; Горизонтальный центроид=83.00 мм; Номинальный вес=44.80 килограмм-сила/м; Носок полки сопряжения=12.20 мм; Носок ребра жесткости сопряжения=20.10 мм; Площадь сечения=57.0 см²; Сопряжение ребра жесткости=8.90 мм; Толщина полки=11.20 мм; Толщина ребра жесткости=6.60 мм; Чистая высота ребра жесткости=290.60 мм; Ширина=166.00 мм
- 30ДБ5: ADSK_Масса на единицу длины=52.50 кг/м; Ix=11873.01 см4; Iy=1025.95 см4; Sx=420.0 см³; Sy=94.3 см³; Wx=749.1 см³; Wy=122.9 см³; b=167.00 мм; h=317.00 мм; ix=133.27 мм; iy=39.17 мм; r=8.90 мм; s=7.60 мм; t=13.20 мм; Вертикальный центроид=158.50 мм; Высота=317.00 мм; Горизонтальный центроид=83.50 мм; Номинальный вес=52.50 килограмм-сила/м; Носок полки сопряжения=12.70 мм; Носок ребра жесткости сопряжения=22.10 мм; Площадь сечения=66.9 см²; Сопряжение ребра жесткости=8.90 мм; Толщина полки=13.20 мм; Толщина ребра жесткости=7.60 мм; Чистая высота ребра жесткости=290.60 мм; Ширина=167.00 мм
- 30ДБ6: ADSK_Масса на единицу длины=40.30 кг/м; Ix=8477.69 см4; Iy=764.36 см4; Sx=311.0 см³; Sy=70.9 см³; Wx=559.6 см³; Wy=92.7 см³; b=165.00 мм; h=303.00 мм; ix=128.56 мм; iy=38.60 мм; r=8.90 мм; s=6.00 мм; t=10.20 мм; Вертикальный центроид=151.50 мм; Высота=303.00 мм; Горизонтальный центроид=82.50 мм; Номинальный вес=40.30 килограмм-сила/м; Носок полки сопряжения=11.90 мм; Носок ребра жесткости сопряжения=19.10 мм; Площадь сечения=51.3 см²; Сопряжение ребра жесткости=8.90 мм; Толщина полки=10.20 мм; Толщина ребра жесткости=6.00 мм; Чистая высота ребра жесткости=282.60 мм; Ширина=165.00 мм
- 30ДБ7: ADSK_Масса на единицу длины=46.20 кг/м; Ix=9942.92 см4; Iy=900.53 см4; Sx=361.1 см³; Sy=83.1 см³; Wx=647.8 см³; Wy=108.5 см³; b=166.00 мм; h=307.00 мм; ix=129.99 мм; iy=39.12 мм; r=8.90 мм; s=6.70 мм; t=11.80 мм; Вертикальный центроид=153.50 мм; Высота=307.00 мм; Горизонтальный центроид=83.00 мм; Номинальный вес=46.20 килограмм-сила/м; Носок полки сопряжения=12.25 мм; Носок ребра жесткости сопряжения=20.70 мм; Площадь сечения=58.8 см²; Сопряжение ребра жесткости=8.90 мм; Толщина полки=11.80 мм; Толщина ребра жесткости=6.70 мм; Чистая высота ребра жесткости=283.40 мм; Ширина=166.00 мм
- 30ДБ8: ADSK_Масса на единицу длины=54.00 кг/м; Ix=11668.10 см4; Iy=1064.87 см4; Sx=422.6 см³; Sy=97.9 см³; Wx=752.8 см³; Wy=127.5 см³; b=167.00 мм; h=310.00 мм; ix=130.26 мм; iy=39.35 мм; r=8.90 мм; s=7.90 мм; t=13.70 мм; Вертикальный центроид=155.00 мм; Высота=310.00 мм; Горизонтальный центроид=83.50 мм; Номинальный вес=54.00 килограмм-сила/м; Носок полки сопряжения=12.85 мм; Носок ребра жесткости сопряжения=22.60 мм; Площадь сечения=68.8 см²; Сопряжение ребра жесткости=8.90 мм; Толщина полки=13.70 мм; Толщина ребра жесткости=7.90 мм; Чистая высота ребра жесткости=282.60 мм; Ширина=167.00 мм
- 35ДБ1: ADSK_Масса на единицу длины=32.80 кг/м; Ix=8267.33 см4; Iy=291.00 см4; Sx=271.0 см³; Sy=35.9 см³; Wx=473.8 см³; Wy=45.8 см³; b=127.00 мм; h=349.00 мм; ix=140.74 мм; iy=26.40 мм; r=10.20 мм; s=5.80 мм; t=8.50 мм; Вертикальный центроид=174.50 мм; Высота=349.00 мм; Горизонтальный центроид=63.50 мм; Номинальный вес=32.80 килограмм-сила/м; Носок полки сопряжения=13.10 мм; Носок ребра жесткости сопряжения=18.70 мм; Площадь сечения=41.7 см²; Сопряжение ребра жесткости=10.20 мм; Толщина полки=8.50 мм; Толщина ребра жесткости=5.80 мм; Чистая высота ребра жесткости=332.00 мм; Ширина=127.00 мм
- 35ДБ2: ADSK_Масса на единицу длины=39.10 кг/м; Ix=10240.24 см4; Iy=375.06 см4; Sx=331.1 см³; Sy=45.8 см³; Wx=580.2 см³; Wy=58.6 см³; b=128.00 мм; h=353.00 мм; ix=143.34 мм; iy=27.43 мм; r=10.20 мм; s=6.50 мм; t=10.70 мм; Вертикальный центроид=176.50 мм; Высота=353.00 мм; Горизонтальный центроид=64.00 мм; Номинальный вес=39.10 килограмм-сила/м; Носок полки сопряжения=13.45 мм; Носок ребра жесткости сопряжения=20.90 мм; Площадь сечения=49.8 см²; Сопряжение ребра жесткости=10.20 мм; Толщина полки=10.70 мм; Толщина ребра жесткости=6.50 мм; Чистая высота ребра жесткости=331.60 мм; Ширина=128.00 мм
- 35ДБ3: ADSK_Масса на единицу длины=45.00 кг/м; Ix=12166.36 см4; Iy=817.94 см4; Sx=389.4 см³; Sy=73.9 см³; Wx=691.3 см³; Wy=95.7 см³; b=171.00 мм; h=352.00 мм; ix=145.66 мм; iy=37.77 мм; r=10.20 мм; s=6.90 мм; t=9.80 мм; Вертикальный центроид=176.00 мм; Высота=352.00 мм; Горизонтальный центроид=85.50 мм; Номинальный вес=45.00 килограмм-сила/м; Носок полки сопряжения=13.65 мм; Носок ребра жесткости сопряжения=20.00 мм; Площадь сечения=57.3 см²; Сопряжение ребра жесткости=10.20 мм; Толщина полки=9.80 мм; Толщина ребра жесткости=6.90 мм; Чистая высота ребра жесткости=332.40 мм; Ширина=171.00 мм
- 35ДБ4: ADSK_Масса на единицу длины=50.60 кг/м; Ix=14130.93 см4; Iy=968.08 см4; Sx=447.0 см³; Sy=87.2 см³; Wx=796.1 см³; Wy=113.2 см³; b=171.00 мм; h=355.00 мм; ix=148.07 мм; iy=38.76 мм; r=10.20 мм; s=7.20 мм; t=11.60 мм; Вертикальный центроид=177.50 мм; Высота=355.00 мм; Горизонтальный центроид=85.50 мм; Номинальный вес=50.60 килограмм-сила/м; Носок полки сопряжения=13.80 мм; Носок ребра жесткости сопряжения=21.80 мм; Площадь сечения=64.5 см²; Сопряжение ребра жесткости=10.20 мм; Толщина полки=11.60 мм; Толщина ребра жесткости=7.20 мм; Чистая высота ребра жесткости=331.80 мм; Ширина=171.00 мм
- 35ДБ5: ADSK_Масса на единицу длины=56.70 кг/м; Ix=16051.94 см4; Iy=1112.72 см4; Sx=504.6 см³; Sy=99.8 см³; Wx=896.8 см³; Wy=129.4 см³; b=172.00 мм; h=358.00 мм; ix=149.14 мм; iy=39.27 мм; r=10.20 мм; s=7.90 мм; t=13.10 мм; Вертикальный центроид=179.00 мм; Высота=358.00 мм; Горизонтальный центроид=86.00 мм; Номинальный вес=56.70 килограмм-сила/м; Носок полки сопряжения=14.15 мм; Носок ребра жесткости сопряжения=23.30 мм; Площадь сечения=72.2 см²; Сопряжение ребра жесткости=10.20 мм; Толщина полки=13.10 мм; Толщина ребра жесткости=7.90 мм; Чистая высота ребра жесткости=331.80 мм; Ширина=172.00 мм
- 35ДБ6: ADSK_Масса на единицу длины=67.10 кг/м; Ix=19414.43 см4; Iy=1362.07 см4; Sx=604.6 см³; Sy=121.5 см³; Wx=1069.7 см³; Wy=157.3 см³; b=173.20 мм; h=363.00 мм; ix=150.73 мм; iy=39.92 мм; r=10.20 мм; s=9.10 мм; t=15.70 мм; Вертикальный центроид=181.50 мм; Высота=363.00 мм; Горизонтальный центроид=86.60 мм; Номинальный вес=67.10 килограмм-сила/м; Носок полки сопряжения=14.75 мм; Носок ребра жесткости сопряжения=25.90 мм; Площадь сечения=85.5 см²; Сопряжение ребра жесткости=10.20 мм; Толщина полки=15.70 мм; Толщина ребра жесткости=9.10 мм; Чистая высота ребра жесткости=331.60 мм; Ширина=173.20 мм
- 35ДБ7: ADSK_Масса на единицу длины=91.00 кг/м; Ix=26754.31 см4; Iy=4483.14 см4; Sx=840.0 см³; Sy=269.0 см³; Wx=1515.8 см³; Wy=353.0 см³; b=254.00 мм; h=353.00 мм; ix=151.92 мм; iy=62.19 мм; r=16.00 мм; s=9.50 мм; t=16.40 мм; Вертикальный центроид=176.50 мм; Высота=353.00 мм; Горизонтальный центроид=127.00 мм; Номинальный вес=91.00 килограмм-сила/м; Носок полки сопряжения=20.75 мм; Носок ребра жесткости сопряжения=32.40 мм; Площадь сечения=115.9 см²; Сопряжение ребра жесткости=16.00 мм; Толщина полки=16.40 мм; Толщина ребра жесткости=9.50 мм; Чистая высота ребра жесткости=320.20 мм; Ширина=254.00 мм
- 35ДБ8: ADSK_Масса на единицу длины=101.40 кг/м; Ix=30209.80 см4; Iy=5062.32 см4; Sx=942.2 см³; Sy=302.9 см³; Wx=1692.4 см³; Wy=397.0 см³; b=255.00 мм; h=357.00 мм; ix=152.93 мм; iy=62.60 мм; r=16.00 мм; s=10.50 мм; t=18.30 мм; Вертикальный центроид=178.50 мм; Высота=357.00 мм; Горизонтальный центроид=127.50 мм; Номинальный вес=101.40 килограмм-сила/м; Носок полки сопряжения=21.25 мм; Носок ребра жесткости сопряжения=34.30 мм; Площадь сечения=129.2 см²; Сопряжение ребра жесткости=16.00 мм; Толщина полки=18.30 мм; Толщина ребра жесткости=10.50 мм; Чистая высота ребра жесткости=320.40 мм; Ширина=255.00 мм
- 35ДБ9: ADSK_Масса на единицу длины=110.40 кг/м; Ix=33153.98 см4; Iy=5570.48 см4; Sx=1029.6 см³; Sy=332.3 см³; Wx=1841.9 см³; Wy=435.2 см³; b=256.00 мм; h=360.00 мм; ix=153.57 мм; iy=62.95 мм; r=16.00 мм; s=11.40 мм; t=19.90 мм; Вертикальный центроид=180.00 мм; Высота=360.00 мм; Горизонтальный центроид=128.00 мм; Номинальный вес=110.40 килограмм-сила/м; Носок полки сопряжения=21.70 мм; Носок ребра жесткости сопряжения=35.90 мм; Площадь сечения=140.6 см²; Сопряжение ребра жесткости=16.00 мм; Толщина полки=19.90 мм; Толщина ребра жесткости=11.40 мм; Чистая высота ребра жесткости=320.20 мм; Ширина=256.00 мм
- 35ДБ10: ADSK_Масса на единицу длины=121.90 кг/м; Ix=36598.33 см4; Iy=6147.42 см4; Sx=1134.9 см³; Sy=366.2 см³; Wx=2016.4 см³; Wy=478.4 см³; b=257.00 мм; h=363.00 мм; ix=153.52 мм; iy=62.92 мм; r=16.00 мм; s=13.00 мм; t=21.70 мм; Вертикальный центроид=181.50 мм; Высота=363.00 мм; Горизонтальный центроид=128.50 мм; Номинальный вес=121.90 килограмм-сила/м; Носок полки сопряжения=22.50 мм; Носок ребра жесткости сопряжения=37.70 мм; Площадь сечения=155.3 см²; Сопряжение ребра жесткости=16.00 мм; Толщина полки=21.70 мм; Толщина ребра жесткости=13.00 мм; Чистая высота ребра жесткости=319.60 мм; Ширина=257.00 мм
- 40ДБ1: ADSK_Масса на единицу длины=39.20 кг/м; Ix=12656.64 см4; Iy=403.59 см4; Sx=365.2 см³; Sy=45.3 см³; Wx=634.4 см³; Wy=57.7 см³; b=140.00 мм; h=399.00 мм; ix=159.19 мм; iy=28.43 мм; r=10.20 мм; s=6.40 мм; t=8.80 мм; Вертикальный центроид=199.50 мм; Высота=399.00 мм; Горизонтальный центроид=70.00 мм; Номинальный вес=39.20 килограмм-сила/м; Носок полки сопряжения=13.40 мм; Носок ребра жесткости сопряжения=19.00 мм; Площадь сечения=49.9 см²; Сопряжение ребра жесткости=10.20 мм; Толщина полки=8.80 мм; Толщина ребра жесткости=6.40 мм; Чистая высота ребра жесткости=381.40 мм; Ширина=140.00 мм
- 40ДБ2: ADSK_Масса на единицу длины=46.20 кг/м; Ix=15570.06 см4; Iy=513.63 см4; Sx=442.3 см³; Sy=57.5 см³; Wx=772.7 см³; Wy=73.4 см³; b=140.00 мм; h=403.00 мм; ix=162.59 мм; iy=29.53 мм; r=10.20 мм; s=7.00 мм; t=11.20 мм; Вертикальный центроид=201.50 мм; Высота=403.00 мм; Горизонтальный центроид=70.00 мм; Номинальный вес=46.20 килограмм-сила/м; Носок полки сопряжения=13.70 мм; Носок ребра жесткости сопряжения=21.40 мм; Площадь сечения=58.9 см²; Сопряжение ребра жесткости=10.20 мм; Толщина полки=11.20 мм; Толщина ребра жесткости=7.00 мм; Чистая высота ребра жесткости=380.60 мм; Ширина=140.00 мм
- 40ДБ3: ADSK_Масса на единицу длины=53.40 кг/м; Ix=18613.44 см4; Iy=1009.08 см4; Sx=522.9 см³; Sy=88.3 см³; Wx=923.7 см³; Wy=114.0 см³; b=177.00 мм; h=403.00 мм; ix=165.36 мм; iy=38.50 мм; r=10.20 мм; s=7.50 мм; t=10.90 мм; Вертикальный центроид=201.50 мм; Высота=403.00 мм; Горизонтальный центроид=88.50 мм; Номинальный вес=53.40 килограмм-сила/м; Носок полки сопряжения=13.95 мм; Носок ребра жесткости сопряжения=21.10 мм; Площадь сечения=68.1 см²; Сопряжение ребра жесткости=10.20 мм; Толщина полки=10.90 мм; Толщина ребра жесткости=7.50 мм; Чистая высота ребра жесткости=381.20 мм; Ширина=177.00 мм
- 40ДБ4: ADSK_Масса на единицу длины=59.50 кг/м; Ix=21585.78 см4; Iy=1204.97 см4; Sx=597.5 см³; Sy=104.5 см³; Wx=1060.7 см³; Wy=135.4 см³; b=178.00 мм; h=407.00 мм; ix=168.72 мм; iy=39.86 мм; r=10.20 мм; s=7.70 мм; t=12.80 мм; Вертикальный центроид=203.50 мм; Высота=407.00 мм; Горизонтальный центроид=89.00 мм; Номинальный вес=59.50 килограмм-сила/м; Носок полки сопряжения=14.05 мм; Носок ребра жесткости сопряжения=23.00 мм; Площадь сечения=75.8 см²; Сопряжение ребра жесткости=10.20 мм; Толщина полки=12.80 мм; Толщина ребра жесткости=7.70 мм; Чистая высота ребра жесткости=381.40 мм; Ширина=178.00 мм
- 40ДБ5: ADSK_Масса на единицу длины=67.50 кг/м; Ix=24557.50 см4; Iy=1379.08 см4; Sx=678.1 см³; Sy=119.3 см³; Wx=1197.9 см³; Wy=154.1 см³; b=179.00 мм; h=410.00 мм; ix=168.99 мм; iy=40.05 мм; r=10.20 мм; s=8.80 мм; t=14.40 мм; Вертикальный центроид=205.00 мм; Высота=410.00 мм; Горизонтальный центроид=89.50 мм; Номинальный вес=67.50 килограмм-сила/м; Носок полки сопряжения=14.60 мм; Носок ребра жесткости сопряжения=24.60 мм; Площадь сечения=86.0 см²; Сопряжение ребра жесткости=10.20 мм; Толщина полки=14.40 мм; Толщина ребра жесткости=8.80 мм; Чистая высота ребра жесткости=381.20 мм; Ширина=179.00 мм
- 40ДБ6: ADSK_Масса на единицу длины=74.90 кг/м; Ix=27495.01 см4; Iy=1558.58 см4; Sx=756.1 см³; Sy=134.4 см³; Wx=1331.5 см³; Wy=173.2 см³; b=180.00 мм; h=413.00 мм; ix=169.72 мм; iy=40.41 мм; r=10.20 мм; s=9.70 мм; t=16.00 мм; Вертикальный центроид=206.50 мм; Высота=413.00 мм; Горизонтальный центроид=90.00 мм; Номинальный вес=74.90 килограмм-сила/м; Носок полки сопряжения=15.05 мм; Носок ребра жесткости сопряжения=26.20 мм; Площадь сечения=95.5 см²; Сопряжение ребра жесткости=10.20 мм; Толщина полки=16.00 мм; Толщина ребра жесткости=9.70 мм; Чистая высота ребра жесткости=381.00 мм; Ширина=180.00 мм
- 40ДБ7: ADSK_Масса на единицу длины=85.00 кг/м; Ix=31537.51 см4; Iy=1803.36 см4; Sx=862.6 см³; Sy=155.1 см³; Wx=1512.6 см³; Wy=199.3 см³; b=181.00 мм; h=417.00 мм; ix=170.68 мм; iy=40.81 мм; r=10.20 мм; s=10.90 мм; t=18.20 мм; Вертикальный центроид=208.50 мм; Высота=417.00 мм; Горизонтальный центроид=90.50 мм; Номинальный вес=85.00 килограмм-сила/м; Носок полки сопряжения=15.65 мм; Носок ребра жесткости сопряжения=28.40 мм; Площадь сечения=108.3 см²; Сопряжение ребра жесткости=10.20 мм; Толщина полки=18.20 мм; Толщина ребра жесткости=10.90 мм; Чистая высота ребра жесткости=380.60 мм; Ширина=181.00 мм
- 45ДБ1: ADSK_Масса на единицу длины=52.00 кг/м; Ix=21216.72 см4; Iy=634.06 см4; Sx=544.3 см³; Sy=65.8 см³; Wx=943.0 см³; Wy=83.4 см³; b=152.00 мм; h=450.00 мм; ix=178.91 мм; iy=30.93 мм; r=10.20 мм; s=7.60 мм; t=10.80 мм; Вертикальный центроид=225.00 мм; Высота=450.00 мм; Горизонтальный центроид=76.00 мм; Номинальный вес=52.00 килограмм-сила/м; Носок полки сопряжения=14.00 мм; Носок ребра жесткости сопряжения=21.00 мм; Площадь сечения=66.3 см²; Сопряжение ребра жесткости=10.20 мм; Толщина полки=10.80 мм; Толщина ребра жесткости=7.60 мм; Чистая высота ребра жесткости=428.40 мм; Ширина=152.00 мм
- 45ДБ2: ADSK_Масса на единицу длины=59.60 кг/м; Ix=25498.98 см4; Iy=796.13 см4; Sx=642.4 см³; Sy=81.5 см³; Wx=1120.8 см³; Wy=104.1 см³; b=153.00 мм; h=455.00 мм; ix=183.34 мм; iy=32.39 мм; r=10.20 мм; s=8.00 мм; t=13.30 мм; Вертикальный центроид=227.50 мм; Высота=455.00 мм; Горизонтальный центроид=76.50 мм; Номинальный вес=59.60 килограмм-сила/м; Носок полки сопряжения=14.20 мм; Носок ребра жесткости сопряжения=23.50 мм; Площадь сечения=75.9 см²; Сопряжение ребра жесткости=10.20 мм; Толщина полки=13.30 мм; Толщина ребра жесткости=8.00 мм; Чистая высота ребра жесткости=428.40 мм; Ширина=153.00 мм
- 45ДБ3: ADSK_Масса на единицу длины=68.50 кг/м; Ix=29698.29 см4; Iy=940.55 см4; Sx=744.1 см³; Sy=96.0 см³; Wx=1294.0 см³; Wy=122.2 см³; b=154.00 мм; h=459.00 мм; ix=184.45 мм; iy=32.83 мм; r=10.20 мм; s=9.10 мм; t=15.40 мм; Вертикальный центроид=229.50 мм; Высота=459.00 мм; Горизонтальный центроид=77.00 мм; Номинальный вес=68.50 килограмм-сила/м; Носок полки сопряжения=14.75 мм; Носок ребра жесткости сопряжения=25.60 мм; Площадь сечения=87.3 см²; Сопряжение ребра жесткости=10.20 мм; Толщина полки=15.40 мм; Толщина ребра жесткости=9.10 мм; Чистая высота ребра жесткости=428.20 мм; Ширина=154.00 мм
- 45ДБ4: ADSK_Масса на единицу длины=74.20 кг/м; Ix=32674.03 см4; Iy=1046.53 см4; Sx=813.3 см³; Sy=106.6 см³; Wx=1414.5 см³; Wy=135.6 см³; b=154.40 мм; h=462.00 мм; ix=185.97 мм; iy=33.28 мм; r=10.20 мм; s=9.60 мм; t=17.00 мм; Вертикальный центроид=231.00 мм; Высота=462.00 мм; Горизонтальный центроид=77.20 мм; Номинальный вес=74.20 килограмм-сила/м; Носок полки сопряжения=15.00 мм; Носок ребра жесткости сопряжения=27.20 мм; Площадь сечения=94.5 см²; Сопряжение ребра жесткости=10.20 мм; Толщина полки=17.00 мм; Толщина ребра жесткости=9.60 мм; Чистая высота ребра жесткости=428.00 мм; Ширина=154.40 мм
- 45ДБ5: ADSK_Масса на единицу длины=82.10 кг/м; Ix=36624.87 см4; Iy=1184.51 см4; Sx=906.3 см³; Sy=120.2 см³; Wx=1571.9 см³; Wy=152.6 см³; b=155.30 мм; h=466.00 мм; ix=187.16 мм; iy=33.66 мм; r=10.20 мм; s=10.50 мм; t=18.90 мм; Вертикальный центроид=233.00 мм; Высота=466.00 мм; Горизонтальный центроид=77.65 мм; Номинальный вес=82.10 килограмм-сила/м; Носок полки сопряжения=15.45 мм; Носок ребра жесткости сопряжения=29.10 мм; Площадь сечения=104.6 см²; Сопряжение ребра жесткости=10.20 мм; Толщина полки=18.90 мм; Толщина ребра жесткости=10.50 мм; Чистая высота ребра жесткости=428.20 мм; Ширина=155.30 мм
- 45ДБ6: ADSK_Масса на единицу длины=67.10 кг/м; Ix=29321.46 см4; Iy=1452.13 см4; Sx=734.7 см³; Sy=118.7 см³; Wx=1294.6 см³; Wy=152.9 см³; b=189.90 мм; h=453.00 мм; ix=185.22 мм; iy=41.22 мм; r=10.20 мм; s=8.50 мм; t=12.70 мм; Вертикальный центроид=226.50 мм; Высота=453.00 мм; Горизонтальный центроид=94.95 мм; Номинальный вес=67.10 килограмм-сила/м; Носок полки сопряжения=14.45 мм; Носок ребра жесткости сопряжения=22.90 мм; Площадь сечения=85.5 см²; Сопряжение ребра жесткости=10.20 мм; Толщина полки=12.70 мм; Толщина ребра жесткости=8.50 мм; Чистая высота ребра жесткости=427.60 мм; Ширина=189.90 мм
- 45ДБ7: ADSK_Масса на единицу длины=74.20 кг/м; Ix=33262.54 см4; Iy=1660.63 см4; Sx=825.1 см³; Sy=135.5 см³; Wx=1455.7 см³; Wy=174.8 см³; b=190.00 мм; h=457.00 мм; ix=187.60 мм; iy=41.92 мм; r=10.20 мм; s=9.00 мм; t=14.50 мм; Вертикальный центроид=228.50 мм; Высота=457.00 мм; Горизонтальный центроид=95.00 мм; Номинальный вес=74.20 килограмм-сила/м; Носок полки сопряжения=14.70 мм; Носок ребра жесткости сопряжения=24.70 мм; Площадь сечения=94.5 см²; Сопряжение ребра жесткости=10.20 мм; Толщина полки=14.50 мм; Толщина ребра жесткости=9.00 мм; Чистая высота ребра жесткости=428.00 мм; Ширина=190.00 мм
- 45ДБ8: ADSK_Масса на единицу длины=81.90 кг/м; Ix=37004.02 см4; Iy=1862.06 см4; Sx=914.6 см³; Sy=151.5 см³; Wx=1608.9 см³; Wy=195.0 см³; b=191.00 мм; h=460.00 мм; ix=188.28 мм; iy=42.24 мм; r=10.20 мм; s=9.90 мм; t=16.00 мм; Вертикальный центроид=230.00 мм; Высота=460.00 мм; Горизонтальный центроид=95.50 мм; Номинальный вес=81.90 килограмм-сила/м; Носок полки сопряжения=15.15 мм; Носок ребра жесткости сопряжения=26.20 мм; Площадь сечения=104.4 см²; Сопряжение ребра жесткости=10.20 мм; Толщина полки=16.00 мм; Толщина ребра жесткости=9.90 мм; Чистая высота ребра жесткости=428.00 мм; Ширина=191.00 мм
- 45ДБ9: ADSK_Масса на единицу длины=89.30 кг/м; Ix=40952.17 см4; Iy=2092.64 см4; Sx=1006.1 см³; Sy=169.4 см³; Wx=1769.0 см³; Wy=218.0 см³; b=192.00 мм; h=463.00 мм; ix=189.73 мм; iy=42.89 мм; r=10.20 мм; s=10.50 мм; t=17.70 мм; Вертикальный центроид=231.50 мм; Высота=463.00 мм; Горизонтальный центроид=96.00 мм; Номинальный вес=89.30 килограмм-сила/м; Носок полки сопряжения=15.45 мм; Носок ребра жесткости сопряжения=27.90 мм; Площадь сечения=113.8 см²; Сопряжение ребра жесткости=10.20 мм; Толщина полки=17.70 мм; Толщина ребра жесткости=10.50 мм; Чистая высота ребра жесткости=427.60 мм; Ширина=192.00 мм
- 45ДБ10: ADSK_Масса на единицу длины=96.60 кг/м; Ix=44505.67 см4; Iy=2282.42 см4; Sx=1090.1 см³; Sy=184.2 см³; Wx=1910.1 см³; Wy=236.5 см³; b=193.00 мм; h=466.00 мм; ix=190.20 мм; iy=43.07 мм; r=10.20 мм; s=11.40 мм; t=19.00 мм; Вертикальный центроид=233.00 мм; Высота=466.00 мм; Горизонтальный центроид=96.50 мм; Номинальный вес=96.60 килограмм-сила/м; Носок полки сопряжения=15.90 мм; Носок ребра жесткости сопряжения=29.20 мм; Площадь сечения=123.0 см²; Сопряжение ребра жесткости=10.20 мм; Толщина полки=19.00 мм; Толщина ребра жесткости=11.40 мм; Чистая высота ребра жесткости=428.00 мм; Ширина=193.00 мм
- 45ДБ11: ADSK_Масса на единицу длины=105.80 кг/м; Ix=48825.33 см4; Iy=2514.63 см4; Sx=1193.7 см³; Sy=202.7 см³; Wx=2082.1 см³; Wy=259.2 см³; b=194.00 мм; h=469.00 мм; ix=190.37 мм; iy=43.20 мм; r=10.20 мм; s=12.60 мм; t=20.60 мм; Вертикальный центроид=234.50 мм; Высота=469.00 мм; Горизонтальный центроид=97.00 мм; Номинальный вес=105.80 килограмм-сила/м; Носок полки сопряжения=16.50 мм; Носок ребра жесткости сопряжения=30.80 мм; Площадь сечения=134.7 см²; Сопряжение ребра жесткости=10.20 мм; Толщина полки=20.60 мм; Толщина ребра жесткости=12.60 мм; Чистая высота ребра жесткости=427.80 мм; Ширина=194.00 мм
- 53ДБ1: ADSK_Масса на единицу длины=72.00 кг/м; Ix=40061.27 см4; Iy=1615.22 см4; Sx=880.1 см³; Sy=122.5 см³; Wx=1529.1 см³; Wy=156.1 см³; b=207.00 мм; h=524.00 мм; ix=209.02 мм; iy=41.97 мм; r=12.70 мм; s=9.00 мм; t=10.90 мм; Вертикальный центроид=262.00 мм; Высота=524.00 мм; Горизонтальный центроид=103.50 мм; Номинальный вес=72.00 килограмм-сила/м; Носок полки сопряжения=17.20 мм; Носок ребра жесткости сопряжения=23.60 мм; Площадь сечения=91.7 см²; Сопряжение ребра жесткости=12.70 мм; Толщина полки=10.90 мм; Толщина ребра жесткости=9.00 мм; Чистая высота ребра жесткости=502.20 мм; Ширина=207.00 мм
- 53ДБ2: ADSK_Масса на единицу длины=82.00 кг/м; Ix=47614.76 см4; Iy=2028.08 см4; Sx=1031.0 см³; Sy=152.2 см³; Wx=1802.3 см³; Wy=194.0 см³; b=209.00 мм; h=528.00 мм; ix=213.56 мм; iy=44.07 мм; r=12.70 мм; s=9.50 мм; t=13.30 мм; Вертикальный центроид=264.00 мм; Высота=528.00 мм; Горизонтальный центроид=104.50 мм; Номинальный вес=82.00 килограмм-сила/м; Носок полки сопряжения=17.45 мм; Носок ребра жесткости сопряжения=26.00 мм; Площадь сечения=104.4 см²; Сопряжение ребра жесткости=12.70 мм; Толщина полки=13.30 мм; Толщина ребра жесткости=9.50 мм; Чистая высота ребра жесткости=501.40 мм; Ширина=209.00 мм
- 53ДБ3: ADSK_Масса на единицу длины=92.50 кг/м; Ix=55246.34 см4; Iy=2379.01 см4; Sx=1181.7 см³; Sy=177.4 см³; Wx=2073.0 см³; Wy=227.7 см³; b=209.00 мм; h=533.00 мм; ix=216.58 мм; iy=44.94 мм; r=12.70 мм; s=10.20 мм; t=15.60 мм; Вертикальный центроид=266.50 мм; Высота=533.00 мм; Горизонтальный центроид=104.50 мм; Номинальный вес=92.50 килограмм-сила/м; Носок полки сопряжения=17.80 мм; Носок ребра жесткости сопряжения=28.30 мм; Площадь сечения=117.8 см²; Сопряжение ребра жесткости=12.70 мм; Толщина полки=15.60 мм; Толщина ребра жесткости=10.20 мм; Чистая высота ребра жесткости=501.80 мм; Ширина=209.00 мм
- 53ДБ4: ADSK_Масса на единицу длины=101.40 кг/м; Ix=61702.67 см4; Iy=2692.14 см4; Sx=1310.1 см³; Sy=199.9 см³; Wx=2298.1 см³; Wy=256.4 см³; b=210.00 мм; h=537.00 мм; ix=218.53 мм; iy=45.65 мм; r=12.70 мм; s=10.90 мм; t=17.40 мм; Вертикальный центроид=268.50 мм; Высота=537.00 мм; Горизонтальный центроид=105.00 мм; Номинальный вес=101.40 килограмм-сила/м; Носок полки сопряжения=18.15 мм; Носок ребра жесткости сопряжения=30.10 мм; Площадь сечения=129.2 см²; Сопряжение ребра жесткости=12.70 мм; Толщина полки=17.40 мм; Толщина ребра жесткости=10.90 мм; Чистая высота ребра жесткости=502.20 мм; Ширина=210.00 мм
- 53ДБ5: ADSK_Масса на единицу длины=109.00 кг/м; Ix=66731.56 см4; Iy=2951.06 см4; Sx=1413.5 см³; Sy=218.3 см³; Wx=2476.1 см³; Wy=279.7 см³; b=211.00 мм; h=539.00 мм; ix=219.20 мм; iy=46.10 мм; r=12.70 мм; s=11.60 мм; t=18.80 мм; Вертикальный центроид=269.50 мм; Высота=539.00 мм; Горизонтальный центроид=105.50 мм; Номинальный вес=109.00 килограмм-сила/м; Носок полки сопряжения=18.50 мм; Носок ребра жесткости сопряжения=31.50 мм; Площадь сечения=138.9 см²; Сопряжение ребра жесткости=12.70 мм; Толщина полки=18.80 мм; Толщина ребра жесткости=11.60 мм; Чистая высота ребра жесткости=501.40 мм; Ширина=211.00 мм
- 53ДБ6: ADSK_Масса на единицу длины=123.20 кг/м; Ix=76082.72 см4; Iy=3377.30 см4; Sx=1604.0 см³; Sy=249.6 см³; Wx=2797.2 см³; Wy=318.6 см³; b=212.00 мм; h=544.00 мм; ix=220.15 мм; iy=46.38 мм; r=12.70 мм; s=13.10 мм; t=21.20 мм; Вертикальный центроид=272.00 мм; Высота=544.00 мм; Горизонтальный центроид=106.00 мм; Номинальный вес=123.20 килограмм-сила/м; Носок полки сопряжения=19.25 мм; Носок ребра жесткости сопряжения=33.90 мм; Площадь сечения=157.0 см²; Сопряжение ребра жесткости=12.70 мм; Толщина полки=21.20 мм; Толщина ребра жесткости=13.10 мм; Чистая высота ребра жесткости=501.60 мм; Ширина=212.00 мм
- 53ДБ7: ADSK_Масса на единицу длины=138.30 кг/м; Ix=86084.33 см4; Iy=3869.60 см4; Sx=1806.6 см³; Sy=284.5 см³; Wx=3136.0 см³; Wy=361.6 см³; b=214.00 мм; h=549.00 мм; ix=221.06 мм; iy=46.87 мм; r=12.70 мм; s=14.70 мм; t=23.60 мм; Вертикальный центроид=274.50 мм; Высота=549.00 мм; Горизонтальный центроид=107.00 мм; Номинальный вес=138.30 килограмм-сила/м; Носок полки сопряжения=20.05 мм; Носок ребра жесткости сопряжения=36.30 мм; Площадь сечения=176.2 см²; Сопряжение ребра жесткости=12.70 мм; Толщина полки=23.60 мм; Толщина ребра жесткости=14.70 мм; Чистая высота ребра жесткости=501.80 мм; Ширина=214.00 мм
- 60ДБ1: ADSK_Масса на единицу длины=81.90 кг/м; Ix=55978.87 см4; Iy=1208.85 см4; Sx=1098.4 см³; Sy=109.1 см³; Wx=1869.1 см³; Wy=135.8 см³; b=178.00 мм; h=599.00 мм; ix=231.68 мм; iy=34.05 мм; r=12.70 мм; s=10.00 мм; t=12.80 мм; Вертикальный центроид=299.50 мм; Высота=599.00 мм; Горизонтальный центроид=89.00 мм; Номинальный вес=81.90 килограмм-сила/м; Носок полки сопряжения=17.70 мм; Носок ребра жесткости сопряжения=25.50 мм; Площадь сечения=104.3 см²; Сопряжение ребра жесткости=12.70 мм; Толщина полки=12.80 мм; Толщина ребра жесткости=10.00 мм; Чистая высота ребра жесткости=573.40 мм; Ширина=178.00 мм
- 60ДБ2: ADSK_Масса на единицу длины=92.30 кг/м; Ix=64629.04 см4; Iy=1441.05 см4; Sx=1256.4 см³; Sy=129.2 см³; Wx=2143.6 см³; Wy=161.0 см³; b=179.00 мм; h=603.00 мм; ix=234.49 мм; iy=35.01 мм; r=12.70 мм; s=10.90 мм; t=15.00 мм; Вертикальный центроид=301.50 мм; Высота=603.00 мм; Горизонтальный центроид=89.50 мм; Номинальный вес=92.30 килограмм-сила/м; Носок полки сопряжения=18.15 мм; Носок ребра жесткости сопряжения=27.70 мм; Площадь сечения=117.5 см²; Сопряжение ребра жесткости=12.70 мм; Толщина полки=15.00 мм; Толщина ребра жесткости=10.90 мм; Чистая высота ребра жесткости=573.00 мм; Ширина=179.00 мм
- 60ДБ3: ADSK_Масса на единицу длины=101.70 кг/м; Ix=76354.38 см4; Iy=2949.85 см4; Sx=1449.8 см³; Sy=202.1 см³; Wx=2532.5 см³; Wy=258.8 см³; b=228.00 мм; h=603.00 мм; ix=242.81 мм; iy=47.72 мм; r=12.70 мм; s=10.50 мм; t=14.90 мм; Вертикальный центроид=301.50 мм; Высота=603.00 мм; Горизонтальный центроид=114.00 мм; Номинальный вес=101.70 килограмм-сила/м; Носок полки сопряжения=17.95 мм; Носок ребра жесткости сопряжения=27.60 мм; Площадь сечения=129.5 см²; Сопряжение ребра жесткости=12.70 мм; Толщина полки=14.90 мм; Толщина ребра жесткости=10.50 мм; Чистая высота ребра жесткости=573.20 мм; Ширина=228.00 мм
- 60ДБ4: ADSK_Масса на единицу длины=113.40 кг/м; Ix=87546.50 см4; Iy=3425.21 см4; Sx=1644.9 см³; Sy=234.4 см³; Wx=2879.8 см³; Wy=300.5 см³; b=228.00 мм; h=608.00 мм; ix=246.15 мм; iy=48.69 мм; r=12.70 мм; s=11.20 мм; t=17.30 мм; Вертикальный центроид=304.00 мм; Высота=608.00 мм; Горизонтальный центроид=114.00 мм; Номинальный вес=113.40 килограмм-сила/м; Носок полки сопряжения=18.30 мм; Носок ребра жесткости сопряжения=30.00 мм; Площадь сечения=144.5 см²; Сопряжение ребра жесткости=12.70 мм; Толщина полки=17.30 мм; Толщина ребра жесткости=11.20 мм; Чистая высота ребра жесткости=573.40 мм; Ширина=228.00 мм
- 60ДБ5: ADSK_Масса на единицу длины=125.10 кг/м; Ix=98536.48 см4; Iy=3932.13 см4; Sx=1837.1 см³; Sy=267.7 см³; Wx=3220.2 см³; Wy=343.4 см³; b=229.00 мм; h=612.00 мм; ix=248.70 мм; iy=49.68 мм; r=12.70 мм; s=11.90 мм; t=19.60 мм; Вертикальный центроид=306.00 мм; Высота=612.00 мм; Горизонтальный центроид=114.50 мм; Номинальный вес=125.10 килограмм-сила/м; Носок полки сопряжения=18.65 мм; Носок ребра жесткости сопряжения=32.30 мм; Площадь сечения=159.3 см²; Сопряжение ребра жесткости=12.70 мм; Толщина полки=19.60 мм; Толщина ребра жесткости=11.90 мм; Чистая высота ребра жесткости=572.80 мм; Ширина=229.00 мм
- 60ДБ6: ADSK_Масса на единицу длины=140.10 кг/м; Ix=111971.15 см4; Iy=4513.82 см4; Sx=2075.0 см³; Sy=306.5 см³; Wx=3629.5 см³; Wy=392.5 см³; b=230.00 мм; h=617.00 мм; ix=250.45 мм; iy=50.28 мм; r=12.70 мм; s=13.10 мм; t=22.20 мм; Вертикальный центроид=308.50 мм; Высота=617.00 мм; Горизонтальный центроид=115.00 мм; Номинальный вес=140.10 килограмм-сила/м; Носок полки сопряжения=19.25 мм; Носок ребра жесткости сопряжения=34.90 мм; Площадь сечения=178.5 см²; Сопряжение ребра жесткости=12.70 мм; Толщина полки=22.20 мм; Толщина ребра жесткости=13.10 мм; Чистая высота ребра жесткости=572.60 мм; Ширина=230.00 мм
- 60ДБ7: ADSK_Масса на единицу длины=153.00 кг/м; Ix=125134.40 см4; Iy=4998.26 см4; Sx=2299.9 см³; Sy=341.2 см³; Wx=4017.2 см³; Wy=436.5 см³; b=229.00 мм; h=623.00 мм; ix=252.89 мм; iy=50.54 мм; r=12.70 мм; s=14.00 мм; t=24.90 мм; Вертикальный центроид=311.50 мм; Высота=623.00 мм; Горизонтальный центроид=114.50 мм; Номинальный вес=153.00 килограмм-сила/м; Носок полки сопряжения=19.70 мм; Носок ребра жесткости сопряжения=37.60 мм; Площадь сечения=195.7 см²; Сопряжение ребра жесткости=12.70 мм; Толщина полки=24.90 мм; Толщина ребра жесткости=14.00 мм; Чистая высота ребра жесткости=573.20 мм; Ширина=229.00 мм
- 70ДБ1: ADSK_Масса на единицу длины=125.00 кг/м; Ix=118774.60 см4; Iy=4409.92 см4; Sx=2007.7 см³; Sy=272.8 см³; Wx=3500.6 см³; Wy=348.6 см³; b=253.00 мм; h=678.00 мм; ix=272.46 мм; iy=52.50 мм; r=15.70 мм; s=11.70 мм; t=16.30 мм; Вертикальный центроид=339.00 мм; Высота=678.00 мм; Горизонтальный центроид=126.50 мм; Номинальный вес=125.00 килограмм-сила/м; Носок полки сопряжения=21.55 мм; Носок ребра жесткости сопряжения=32.00 мм; Площадь сечения=160.0 см²; Сопряжение ребра жесткости=15.70 мм; Толщина полки=16.30 мм; Толщина ребра жесткости=11.70 мм; Чистая высота ребра жесткости=645.40 мм; Ширина=253.00 мм
- 70ДБ2: ADSK_Масса на единицу длины=140.00 кг/м; Ix=135901.80 см4; Iy=5155.91 см4; Sx=2272.6 см³; Sy=317.5 см³; Wx=3974.9 см³; Wy=406.5 см³; b=254.00 мм; h=684.00 мм; ix=276.32 мм; iy=53.82 мм; r=15.70 мм; s=12.40 мм; t=18.90 мм; Вертикальный центроид=342.00 мм; Высота=684.00 мм; Горизонтальный центроид=127.00 мм; Номинальный вес=140.00 килограмм-сила/м; Носок полки сопряжения=21.90 мм; Носок ребра жесткости сопряжения=34.60 мм; Площадь сечения=178.0 см²; Сопряжение ребра жесткости=15.70 мм; Толщина полки=18.90 мм; Толщина ребра жесткости=12.40 мм; Чистая высота ребра жесткости=646.20 мм; Ширина=254.00 мм
- 70ДБ3: ADSK_Масса на единицу длины=152.00 кг/м; Ix=150835.90 см4; Iy=5804.27 см4; Sx=2504.5 см³; Sy=356.3 см³; Wx=4384.8 см³; Wy=456.3 см³; b=254.00 мм; h=688.00 мм; ix=278.88 мм; iy=54.71 мм; r=15.70 мм; s=13.10 мм; t=21.10 мм; Вертикальный центроид=344.00 мм; Высота=688.00 мм; Горизонтальный центроид=127.00 мм; Номинальный вес=152.00 килограмм-сила/м; Носок полки сопряжения=22.25 мм; Носок ребра жесткости сопряжения=36.80 мм; Площадь сечения=193.9 см²; Сопряжение ребра жесткости=15.70 мм; Толщина полки=21.10 мм; Толщина ребра жесткости=13.10 мм; Чистая высота ребра жесткости=645.80 мм; Ширина=254.00 мм
- 70ДБ4: ADSK_Масса на единицу длины=170.00 кг/м; Ix=169986.50 см4; Iy=6617.85 см4; Sx=2809.7 см³; Sy=404.7 см³; Wx=4905.8 см³; Wy=517.0 см³; b=256.00 мм; h=693.00 мм; ix=280.24 мм; iy=55.29 мм; r=15.70 мм; s=14.50 мм; t=23.60 мм; Вертикальный центроид=346.50 мм; Высота=693.00 мм; Горизонтальный центроид=128.00 мм; Номинальный вес=170.00 килограмм-сила/м; Носок полки сопряжения=22.95 мм; Носок ребра жесткости сопряжения=39.30 мм; Площадь сечения=216.5 см²; Сопряжение ребра жесткости=15.70 мм; Толщина полки=23.60 мм; Толщина ребра жесткости=14.50 мм; Чистая высота ребра жесткости=645.80 мм; Ширина=256.00 мм
- 70ДБ5: ADSK_Масса на единицу длины=192.00 кг/м; Ix=197984.50 см4; Iy=7642.66 см4; Sx=3229.3 см³; Sy=470.6 см³; Wx=5640.6 см³; Wy=601.8 см³; b=254.00 мм; h=702.00 мм; ix=284.92 мм; iy=55.98 мм; r=15.70 мм; s=15.50 мм; t=27.90 мм; Вертикальный центроид=351.00 мм; Высота=702.00 мм; Горизонтальный центроид=127.00 мм; Номинальный вес=192.00 килограмм-сила/м; Носок полки сопряжения=23.45 мм; Носок ребра жесткости сопряжения=43.60 мм; Площадь сечения=243.9 см²; Сопряжение ребра жесткости=15.70 мм; Толщина полки=27.90 мм; Толщина ребра жесткости=15.50 мм; Чистая высота ребра жесткости=646.20 мм; Ширина=254.00 мм
- 85ДБ1: ADSK_Масса на единицу длины=176.00 кг/м; Ix=246276.80 см4; Iy=7822.90 см4; Sx=3406.7 см³; Sy=421.7 см³; Wx=5898.9 см³; Wy=535.8 см³; b=292.00 мм; h=835.00 мм; ix=331.47 мм; iy=59.08 мм; r=17.00 мм; s=14.00 мм; t=18.80 мм; Вертикальный центроид=417.50 мм; Высота=835.00 мм; Горизонтальный центроид=146.00 мм; Номинальный вес=176.00 килограмм-сила/м; Носок полки сопряжения=24.00 мм; Носок ребра жесткости сопряжения=35.80 мм; Площадь сечения=224.2 см²; Сопряжение ребра жесткости=17.00 мм; Толщина полки=18.80 мм; Толщина ребра жесткости=14.00 мм; Чистая высота ребра жесткости=797.40 мм; Ширина=292.00 мм
- 85ДБ2: ADSK_Масса на единицу длины=193.00 кг/м; Ix=278350.20 см4; Iy=9029.33 см4; Sx=3812.3 см³; Sy=485.6 см³; Wx=6627.4 см³; Wy=618.5 см³; b=292.00 мм; h=840.00 мм; ix=336.00 мм; iy=60.52 мм; r=17.00 мм; s=14.70 мм; t=21.70 мм; Вертикальный центроид=420.00 мм; Высота=840.00 мм; Горизонтальный центроид=146.00 мм; Номинальный вес=193.00 килограмм-сила/м; Носок полки сопряжения=24.35 мм; Носок ребра жесткости сопряжения=38.70 мм; Площадь сечения=246.6 см²; Сопряжение ребра жесткости=17.00 мм; Толщина полки=21.70 мм; Толщина ребра жесткости=14.70 мм; Чистая высота ребра жесткости=796.60 мм; Ширина=292.00 мм
- 85ДБ3: ADSK_Масса на единицу длины=210.00 кг/м; Ix=310620.90 см4; Iy=10257.47 см4; Sx=4214.0 см³; Sy=548.9 см³; Wx=7343.3 см³; Wy=700.2 см³; b=293.00 мм; h=846.00 мм; ix=340.15 мм; iy=61.81 мм; r=17.00 мм; s=15.40 мм; t=24.40 мм; Вертикальный центроид=423.00 мм; Высота=846.00 мм; Горизонтальный центроид=146.50 мм; Номинальный вес=210.00 килограмм-сила/м; Носок полки сопряжения=24.70 мм; Носок ребра жесткости сопряжения=41.40 мм; Площадь сечения=268.5 см²; Сопряжение ребра жесткости=17.00 мм; Толщина полки=24.40 мм; Толщина ребра жесткости=15.40 мм; Чистая высота ребра жесткости=797.20 мм; Ширина=293.00 мм
- 85ДБ4: ADSK_Масса на единицу длины=226.00 кг/м; Ix=339977.20 см4; Iy=11382.74 см4; Sx=4580.3 см³; Sy=606.5 см³; Wx=7990.1 см³; Wy=774.3 см³; b=294.00 мм; h=851.00 мм; ix=343.17 мм; iy=62.79 мм; r=17.00 мм; s=16.10 мм; t=26.80 мм; Вертикальный центроид=425.50 мм; Высота=851.00 мм; Горизонтальный центроид=147.00 мм; Номинальный вес=226.00 килограмм-сила/м; Носок полки сопряжения=25.05 мм; Носок ребра жесткости сопряжения=43.80 мм; Площадь сечения=288.7 см²; Сопряжение ребра жесткости=17.00 мм; Толщина полки=26.80 мм; Толщина ребра жесткости=16.10 мм; Чистая высота ребра жесткости=797.40 мм; Ширина=294.00 мм
- 85ДБ5: ADSK_Масса на единицу длины=251.00 кг/м; Ix=386394.30 см4; Iy=12900.66 см4; Sx=5150.9 см³; Sy=691.3 см³; Wx=8996.4 см³; Wy=883.6 см³; b=292.00 мм; h=859.00 мм; ix=347.90 мм; iy=63.57 мм; r=17.00 мм; s=17.00 мм; t=31.00 мм; Вертикальный центроид=429.50 мм; Высота=859.00 мм; Горизонтальный центроид=146.00 мм; Номинальный вес=251.00 килограмм-сила/м; Носок полки сопряжения=25.50 мм; Носок ребра жесткости сопряжения=48.00 мм; Площадь сечения=319.3 см²; Сопряжение ребра жесткости=17.00 мм; Толщина полки=31.00 мм; Толщина ребра жесткости=17.00 мм; Чистая высота ребра жесткости=797.00 мм; Ширина=292.00 мм
- 90ДБ1: ADSK_Масса на единицу длины=201.00 кг/м; Ix=325421.40 см4; Iy=9441.91 см4; Sx=4181.0 см³; Sy=491.4 см³; Wx=7207.5 см³; Wy=621.2 см³; b=304.00 мм; h=903.00 мм; ix=356.14 мм; iy=60.66 мм; r=18.20 мм; s=15.20 мм; t=20.10 мм; Вертикальный центроид=451.50 мм; Высота=903.00 мм; Горизонтальный центроид=152.00 мм; Номинальный вес=201.00 килограмм-сила/м; Носок полки сопряжения=25.80 мм; Носок ребра жесткости сопряжения=38.30 мм; Площадь сечения=256.6 см²; Сопряжение ребра жесткости=18.20 мм; Толщина полки=20.10 мм; Толщина ребра жесткости=15.20 мм; Чистая высота ребра жесткости=862.80 мм; Ширина=304.00 мм
- 90ДБ2: ADSK_Масса на единицу длины=223.00 кг/м; Ix=376536.80 см4; Iy=11224.62 см4; Sx=4762.4 см³; Sy=581.2 см³; Wx=8266.4 см³; Wy=738.5 см³; b=304.00 мм; h=911.00 мм; ix=363.53 мм; iy=62.76 мм; r=18.20 мм; s=15.90 мм; t=23.90 мм; Вертикальный центроид=455.50 мм; Высота=911.00 мм; Горизонтальный центроид=152.00 мм; Номинальный вес=223.00 килограмм-сила/м; Носок полки сопряжения=26.15 мм; Носок ребра жесткости сопряжения=42.10 мм; Площадь сечения=284.9 см²; Сопряжение ребра жесткости=18.20 мм; Толщина полки=23.90 мм; Толщина ребра жесткости=15.90 мм; Чистая высота ребра жесткости=863.20 мм; Ширина=304.00 мм
- 90ДБ3: ADSK_Масса на единицу длины=238.00 кг/м; Ix=406354.50 см4; Iy=12285.06 см4; Sx=5117.5 см³; Sy=634.6 см³; Wx=8878.3 см³; Wy=805.5 см³; b=305.00 мм; h=915.00 мм; ix=366.09 мм; iy=63.65 мм; r=18.20 мм; s=16.50 мм; t=25.90 мм; Вертикальный центроид=457.50 мм; Высота=915.00 мм; Горизонтальный центроид=152.50 мм; Номинальный вес=238.00 килограмм-сила/м; Носок полки сопряжения=26.45 мм; Носок ребра жесткости сопряжения=44.10 мм; Площадь сечения=303.2 см²; Сопряжение ребра жесткости=18.20 мм; Толщина полки=25.90 мм; Толщина ребра жесткости=16.50 мм; Чистая высота ребра жесткости=863.20 мм; Ширина=305.00 мм
- 90ДБ4: ADSK_Масса на единицу длины=253.00 кг/м; Ix=438001.80 см4; Iy=13366.98 см4; Sx=5487.3 см³; Sy=686.1 см³; Wx=9532.1 см³; Wy=873.7 см³; b=306.00 мм; h=919.00 мм; ix=367.65 мм; iy=64.23 мм; r=18.20 мм; s=17.30 мм; t=27.90 мм; Вертикальный центроид=459.50 мм; Высота=919.00 мм; Горизонтальный центроид=153.00 мм; Номинальный вес=253.00 килограмм-сила/м; Носок полки сопряжения=26.85 мм; Носок ребра жесткости сопряжения=46.10 мм; Площадь сечения=324.1 см²; Сопряжение ребра жесткости=18.20 мм; Толщина полки=27.90 мм; Толщина ребра жесткости=17.30 мм; Чистая высота ребра жесткости=863.20 мм; Ширина=306.00 мм
- 90ДБ5: ADSK_Масса на единицу длины=271.00 кг/м; Ix=471631.30 см4; Iy=14518.10 см4; Sx=5892.7 см³; Sy=745.9 см³; Wx=10219.5 см³; Wy=845.8 см³; b=307.00 мм; h=923.00 мм; ix=369.14 мм; iy=64.77 мм; r=18.20 мм; s=18.40 мм; t=30.00 мм; Вертикальный центроид=461.50 мм; Высота=923.00 мм; Горизонтальный центроид=153.50 мм; Номинальный вес=271.00 килограмм-сила/м; Носок полки сопряжения=27.40 мм; Носок ребра жесткости сопряжения=48.20 мм; Площадь сечения=346.1 см²; Сопряжение ребра жесткости=18.20 мм; Толщина полки=30.00 мм; Толщина ребра жесткости=18.40 мм; Чистая высота ребра жесткости=863.00 мм; Ширина=307.00 мм
- 90ДБ6: ADSK_Масса на единицу длины=289.00 кг/м; Ix=504537.30 см4; Iy=15642.01 см4; Sx=6283.7 см³; Sy=801.5 см³; Wx=10885.4 см³; Wy=1015.7 см³; b=308.00 мм; h=927.00 мм; ix=370.44 мм; iy=65.23 мм; r=18.20 мм; s=19.40 мм; t=32.00 мм; Вертикальный центроид=463.50 мм; Высота=927.00 мм; Горизонтальный центроид=154.00 мм; Номинальный вес=289.00 килограмм-сила/м; Носок полки сопряжения=27.90 мм; Носок ребра жесткости сопряжения=50.20 мм; Площадь сечения=367.7 см²; Сопряжение ребра жесткости=18.20 мм; Толщина полки=32.00 мм; Толщина ребра жесткости=19.40 мм; Чистая высота ребра жесткости=863.00 мм; Ширина=308.00 мм
- 100ДБ1: ADSK_Масса на единицу длины=222.00 кг/м; Ix=407664.40 см4; Iy=9545.79 см4; Sx=4902.0 см³; Sy=510.4 см³; Wx=8405.5 см³; Wy=636.4 см³; b=300.00 мм; h=970.00 мм; ix=379.63 мм; iy=58.10 мм; r=29.00 мм; s=16.00 мм; t=21.10 мм; Вертикальный центроид=485.00 мм; Высота=970.00 мм; Горизонтальный центроид=150.00 мм; Номинальный вес=222.00 килограмм-сила/м; Носок полки сопряжения=37.00 мм; Носок ребра жесткости сопряжения=50.10 мм; Площадь сечения=282.8 см²; Сопряжение ребра жесткости=29.00 мм; Толщина полки=21.10 мм; Толщина ребра жесткости=16.00 мм; Чистая высота ребра жесткости=927.80 мм; Ширина=300.00 мм
- 100ДБ2: ADSK_Масса на единицу длины=249.00 кг/м; Ix=481076.70 см4; Iy=11754.44 см4; Sx=5673.0 см³; Sy=624.2 см³; Wx=9817.9 см³; Wy=783.5 см³; b=300.00 мм; h=980.00 мм; ix=389.66 мм; iy=60.91 мм; r=29.00 мм; s=16.50 мм; t=26.00 мм; Вертикальный центроид=490.00 мм; Высота=980.00 мм; Горизонтальный центроид=150.00 мм; Номинальный вес=249.00 килограмм-сила/м; Носок полки сопряжения=37.25 мм; Носок ребра жесткости сопряжения=55.00 мм; Площадь сечения=316.8 см²; Сопряжение ребра жесткости=29.00 мм; Толщина полки=26.00 мм; Толщина ребра жесткости=16.50 мм; Чистая высота ребра жесткости=928.00 мм; Ширина=300.00 мм
- 100ДБ3: ADSK_Масса на единицу длины=272.00 кг/м; Ix=553844.20 см4; Iy=14004.44 см4; Sx=6411.3 см³; Sy=737.0 см³; Wx=11188.8 см³; Wy=933.5 см³; b=300.00 мм; h=990.00 мм; ix=399.60 мм; iy=63.54 мм; r=29.00 мм; s=16.50 мм; t=31.00 мм; Вертикальный центроид=495.00 мм; Высота=990.00 мм; Горизонтальный центроид=150.00 мм; Номинальный вес=272.00 килограмм-сила/м; Носок полки сопряжения=37.25 мм; Носок ребра жесткости сопряжения=60.00 мм; Площадь сечения=346.8 см²; Сопряжение ребра жесткости=29.00 мм; Толщина полки=31.00 мм; Толщина ребра жесткости=16.50 мм; Чистая высота ребра жесткости=928.00 мм; Ширина=300.00 мм
- 10ДК0: ADSK_Масса на единицу длины=12.20 кг/м; Ix=236.51 см4; Iy=92.06 см4; Sx=29.2 см³; Sy=14.2 см³; Wx=52.0 см³; Wy=18.4 см³; b=100.00 мм; h=91.00 мм; ix=38.94 мм; iy=24.29 мм; r=12.00 мм; s=4.20 мм; t=5.50 мм; Вертикальный центроид=45.50 мм; Высота=91.00 мм; Горизонтальный центроид=50.00 мм; Номинальный вес=12.20 килограмм-сила/м; Носок полки сопряжения=14.10 мм; Носок ребра жесткости сопряжения=17.50 мм; Площадь сечения=15.6 см²; Сопряжение ребра жесткости=12.00 мм; Толщина полки=5.50 мм; Толщина ребра жесткости=4.20 мм; Чистая высота ребра жесткости=80.00 мм; Ширина=100.00 мм
- 10ДК1: ADSK_Масса на единицу длины=16.70 кг/м; Ix=349.23 см4; Iy=133.81 см4; Sx=41.5 см³; Sy=20.6 см³; Wx=72.8 см³; Wy=26.8 см³; b=100.00 мм; h=96.00 мм; ix=40.55 мм; iy=25.10 мм; r=12.00 мм; s=5.00 мм; t=8.00 мм; Вертикальный центроид=48.00 мм; Высота=96.00 мм; Горизонтальный центроид=50.00 мм; Номинальный вес=16.70 килограмм-сила/м; Носок полки сопряжения=14.50 мм; Носок ребра жесткости сопряжения=20.00 мм; Площадь сечения=21.2 см²; Сопряжение ребра жесткости=12.00 мм; Толщина полки=8.00 мм; Толщина ребра жесткости=5.00 мм; Чистая высота ребра жесткости=80.00 мм; Ширина=100.00 мм
- 10ДК2: ADSK_Масса на единицу длины=20.40 кг/м; Ix=449.55 см4; Iy=167.27 см4; Sx=52.1 см³; Sy=25.7 см³; Wx=89.9 см³; Wy=33.5 см³; b=100.00 мм; h=100.00 мм; ix=41.55 мм; iy=25.35 мм; r=12.00 мм; s=6.00 мм; t=10.00 мм; Вертикальный центроид=50.00 мм; Высота=100.00 мм; Горизонтальный центроид=50.00 мм; Номинальный вес=20.40 килограмм-сила/м; Носок полки сопряжения=15.00 мм; Носок ребра жесткости сопряжения=22.00 мм; Площадь сечения=26.0 см²; Сопряжение ребра жесткости=12.00 мм; Толщина полки=10.00 мм; Толщина ребра жесткости=6.00 мм; Чистая высота ребра жесткости=80.00 мм; Ширина=100.00 мм
- 10ДК3: ADSK_Масса на единицу длины=41.80 кг/м; Ix=1142.61 см4; Iy=399.15 см4; Sx=117.9 см³; Sy=58.2 см³; Wx=190.4 см³; Wy=75.3 см³; b=106.00 мм; h=120.00 мм; ix=46.33 мм; iy=27.38 мм; r=12.00 мм; s=12.00 мм; t=20.00 мм; Вертикальный центроид=60.00 мм; Высота=120.00 мм; Горизонтальный центроид=53.00 мм; Номинальный вес=41.80 килограмм-сила/м; Носок полки сопряжения=18.00 мм; Носок ребра жесткости сопряжения=32.00 мм; Площадь сечения=53.2 см²; Сопряжение ребра жесткости=12.00 мм; Толщина полки=20.00 мм; Толщина ребра жесткости=12.00 мм; Чистая высота ребра жесткости=80.00 мм; Ширина=106.00 мм
- 12ДК0: ADSK_Масса на единицу длины=14.60 кг/м; Ix=413.36 см4; Iy=158.81 см4; Sx=42.2 см³; Sy=20.3 см³; Wx=75.9 см³; Wy=26.5 см³; b=120.00 мм; h=109.00 мм; ix=47.21 мм; iy=29.26 мм; r=12.00 мм; s=4.20 мм; t=5.50 мм; Вертикальный центроид=54.50 мм; Высота=109.00 мм; Горизонтальный центроид=60.00 мм; Номинальный вес=14.60 килограмм-сила/м; Носок полки сопряжения=14.10 мм; Носок ребра жесткости сопряжения=17.50 мм; Площадь сечения=18.6 см²; Сопряжение ребра жесткости=12.00 мм; Толщина полки=5.50 мм; Толщина ребра жесткости=4.20 мм; Чистая высота ребра жесткости=98.00 мм; Ширина=120.00 мм
- 12ДК1: ADSK_Масса на единицу длины=19.90 кг/м; Ix=606.15 см4; Iy=230.90 см4; Sx=59.8 см³; Sy=29.4 см³; Wx=106.3 см³; Wy=38.5 см³; b=120.00 мм; h=114.00 мм; ix=48.91 мм; iy=30.19 мм; r=12.00 мм; s=5.00 мм; t=8.00 мм; Вертикальный центроид=57.00 мм; Высота=114.00 мм; Горизонтальный центроид=60.00 мм; Номинальный вес=19.90 килограмм-сила/м; Носок полки сопряжения=14.50 мм; Носок ребра жесткости сопряжения=20.00 мм; Площадь сечения=25.3 см²; Сопряжение ребра жесткости=12.00 мм; Толщина полки=8.00 мм; Толщина ребра жесткости=5.00 мм; Чистая высота ребра жесткости=98.00 мм; Ширина=120.00 мм
- 12ДК2: ADSK_Масса на единицу длины=26.70 кг/м; Ix=864.37 см4; Iy=317.52 см4; Sx=82.6 см³; Sy=40.5 см³; Wx=144.1 см³; Wy=52.9 см³; b=120.00 мм; h=120.00 мм; ix=50.42 мм; iy=30.56 мм; r=12.00 мм; s=6.50 мм; t=11.00 мм; Вертикальный центроид=60.00 мм; Высота=120.00 мм; Горизонтальный центроид=60.00 мм; Номинальный вес=26.70 килограмм-сила/м; Носок полки сопряжения=15.25 мм; Носок ребра жесткости сопряжения=23.00 мм; Площадь сечения=34.0 см²; Сопряжение ребра жесткости=12.00 мм; Толщина полки=11.00 мм; Толщина ребра жесткости=6.50 мм; Чистая высота ребра жесткости=98.00 мм; Ширина=120.00 мм
- 12ДК3: ADSK_Масса на единицу длины=52.10 кг/м; Ix=2017.57 см4; Iy=702.78 см4; Sx=175.3 см³; Sy=85.8 см³; Wx=288.2 см³; Wy=111.6 см³; b=126.00 мм; h=140.00 мм; ix=55.12 мм; iy=32.53 мм; r=12.00 мм; s=12.50 мм; t=21.00 мм; Вертикальный центроид=70.00 мм; Высота=140.00 мм; Горизонтальный центроид=63.00 мм; Номинальный вес=52.10 килограмм-сила/м; Носок полки сопряжения=18.25 мм; Носок ребра жесткости сопряжения=33.00 мм; Площадь сечения=66.4 см²; Сопряжение ребра жесткости=12.00 мм; Толщина полки=21.00 мм; Толщина ребра жесткости=12.50 мм; Чистая высота ребра жесткости=98.00 мм; Ширина=126.00 мм
- 14ДК0: ADSK_Масса на единицу длины=18.10 кг/м; Ix=719.45 см4; Iy=274.83 см4; Sx=61.9 см³; Sy=30.0 см³; Wx=112.4 см³; Wy=39.3 см³; b=140.00 мм; h=128.00 мм; ix=55.90 мм; iy=34.55 мм; r=12.00 мм; s=4.30 мм; t=6.00 мм; Вертикальный центроид=64.00 мм; Высота=128.00 мм; Горизонтальный центроид=70.00 мм; Номинальный вес=18.10 килограмм-сила/м; Носок полки сопряжения=14.15 мм; Носок ребра жесткости сопряжения=18.00 мм; Площадь сечения=23.0 см²; Сопряжение ребра жесткости=12.00 мм; Толщина полки=6.00 мм; Толщина ребра жесткости=4.30 мм; Чистая высота ребра жесткости=116.00 мм; Ширина=140.00 мм
- 14ДК1: ADSK_Масса на единицу длины=24.70 кг/м; Ix=1033.13 см4; Iy=389.32 см4; Sx=86.8 см³; Sy=42.4 см³; Wx=155.4 см³; Wy=55.6 см³; b=140.00 мм; h=133.00 мм; ix=57.35 мм; iy=35.20 мм; r=12.00 мм; s=5.50 мм; t=8.50 мм; Вертикальный центроид=66.50 мм; Высота=133.00 мм; Горизонтальный центроид=70.00 мм; Номинальный вес=24.70 килограмм-сила/м; Носок полки сопряжения=14.75 мм; Носок ребра жесткости сопряжения=20.50 мм; Площадь сечения=31.4 см²; Сопряжение ребра жесткости=12.00 мм; Толщина полки=8.50 мм; Толщина ребра жесткости=5.50 мм; Чистая высота ребра жесткости=116.00 мм; Ширина=140.00 мм
- 14ДК2: ADSK_Масса на единицу длины=33.70 кг/м; Ix=1509.23 см4; Iy=549.67 см4; Sx=122.7 см³; Sy=59.9 см³; Wx=215.6 см³; Wy=78.5 см³; b=140.00 мм; h=140.00 мм; ix=59.27 мм; iy=35.77 мм; r=12.00 мм; s=7.00 мм; t=12.00 мм; Вертикальный центроид=70.00 мм; Высота=140.00 мм; Горизонтальный центроид=70.00 мм; Номинальный вес=33.70 килограмм-сила/м; Носок полки сопряжения=15.50 мм; Носок ребра жесткости сопряжения=24.00 мм; Площадь сечения=43.0 см²; Сопряжение ребра жесткости=12.00 мм; Толщина полки=12.00 мм; Толщина ребра жесткости=7.00 мм; Чистая высота ребра жесткости=116.00 мм; Ширина=140.00 мм
- 14ДК3: ADSK_Масса на единицу длины=62.90 кг/м; Ix=3270.24 см4; Iy=1121.06 см4; Sx=245.4 см³; Sy=118.7 см³; Wx=408.8 см³; Wy=154.6 см³; b=145.00 мм; h=160.00 мм; ix=63.89 мм; iy=37.41 мм; r=12.00 мм; s=13.00 мм; t=22.00 мм; Вертикальный центроид=80.00 мм; Высота=160.00 мм; Горизонтальный центроид=72.50 мм; Номинальный вес=62.90 килограмм-сила/м; Носок полки сопряжения=18.50 мм; Носок ребра жесткости сопряжения=34.00 мм; Площадь сечения=80.1 см²; Сопряжение ребра жесткости=12.00 мм; Толщина полки=22.00 мм; Толщина ребра жесткости=13.00 мм; Чистая высота ребра жесткости=116.00 мм; Ширина=145.00 мм
- 15ДК1: ADSK_Масса на единицу длины=22.50 кг/м; Ix=1213.15 см4; Iy=386.64 см4; Sx=88.6 см³; Sy=38.8 см³; Wx=159.6 см³; Wy=50.9 см³; b=152.00 мм; h=152.00 мм; ix=65.12 мм; iy=36.76 мм; r=7.60 мм; s=5.80 мм; t=6.60 мм; Вертикальный центроид=76.00 мм; Высота=152.00 мм; Горизонтальный центроид=76.00 мм; Номинальный вес=22.50 килограмм-сила/м; Носок полки сопряжения=10.50 мм; Носок ребра жесткости сопряжения=14.20 мм; Площадь сечения=28.6 см²; Сопряжение ребра жесткости=7.60 мм; Толщина полки=6.60 мм; Толщина ребра жесткости=5.80 мм; Чистая высота ребра жесткости=138.80 мм; Ширина=152.00 мм
- 15ДК2: ADSK_Масса на единицу длины=29.90 кг/м; Ix=1722.51 см4; Iy=555.61 см4; Sx=122.6 см³; Sy=55.3 см³; Wx=219.4 см³; Wy=72.6 см³; b=153.00 мм; h=157.00 мм; ix=67.25 мм; iy=38.19 мм; r=7.60 мм; s=6.60 мм; t=9.30 мм; Вертикальный центроид=78.50 мм; Высота=157.00 мм; Горизонтальный центроид=76.50 мм; Номинальный вес=29.90 килограмм-сила/м; Носок полки сопряжения=10.90 мм; Носок ребра жесткости сопряжения=16.90 мм; Площадь сечения=38.1 см²; Сопряжение ребра жесткости=7.60 мм; Толщина полки=9.30 мм; Толщина ребра жесткости=6.60 мм; Чистая высота ребра жесткости=138.40 мм; Ширина=153.00 мм
- 15ДК3: ADSK_Масса на единицу длины=37.30 кг/м; Ix=2227.67 см4; Iy=706.89 см4; Sx=155.5 см³; Sy=70.1 см³; Wx=275.0 см³; Wy=91.8 см³; b=154.00 мм; h=162.00 мм; ix=68.51 мм; iy=38.59 мм; r=7.60 мм; s=8.10 мм; t=11.60 мм; Вертикальный центроид=81.00 мм; Высота=162.00 мм; Горизонтальный центроид=77.00 мм; Номинальный вес=37.30 килограмм-сила/м; Носок полки сопряжения=11.65 мм; Носок ребра жесткости сопряжения=19.20 мм; Площадь сечения=47.5 см²; Сопряжение ребра жесткости=7.60 мм; Толщина полки=11.60 мм; Толщина ребра жесткости=8.10 мм; Чистая высота ребра жесткости=138.80 мм; Ширина=154.00 мм
- 16ДК0: ADSK_Масса на единицу длины=23.80 кг/м; Ix=1282.88 см4; Iy=478.73 см4; Sx=95.2 см³; Sy=45.7 см³; Wx=173.4 см³; Wy=59.8 см³; b=160.00 мм; h=148.00 мм; ix=65.00 мм; iy=39.71 мм; r=15.00 мм; s=4.50 мм; t=7.00 мм; Вертикальный центроид=74.00 мм; Высота=148.00 мм; Горизонтальный центроид=80.00 мм; Номинальный вес=23.80 килограмм-сила/м; Носок полки сопряжения=17.25 мм; Носок ребра жесткости сопряжения=22.00 мм; Площадь сечения=30.4 см²; Сопряжение ребра жесткости=15.00 мм; Толщина полки=7.00 мм; Толщина ребра жесткости=4.50 мм; Чистая высота ребра жесткости=134.00 мм; Ширина=160.00 мм
- 16ДК1: ADSK_Масса на единицу длины=30.40 кг/м; Ix=1672.98 см4; Iy=615.57 см4; Sx=122.6 см³; Sy=58.8 см³; Wx=220.1 см³; Wy=77.0 см³; b=160.00 мм; h=152.00 мм; ix=65.69 мм; iy=39.85 мм; r=15.00 мм; s=6.00 мм; t=9.00 мм; Вертикальный центроид=76.00 мм; Высота=152.00 мм; Горизонтальный центроид=80.00 мм; Номинальный вес=30.40 килограмм-сила/м; Носок полки сопряжения=18.00 мм; Носок ребра жесткости сопряжения=24.00 мм; Площадь сечения=38.8 см²; Сопряжение ребра жесткости=15.00 мм; Толщина полки=9.00 мм; Толщина ребра жесткости=6.00 мм; Чистая высота ребра жесткости=134.00 мм; Ширина=160.00 мм
- 16ДК2: ADSK_Масса на единицу длины=42.60 кг/м; Ix=2492.00 см4; Iy=889.23 см4; Sx=177.0 см³; Sy=85.0 см³; Wx=311.5 см³; Wy=111.2 см³; b=160.00 мм; h=160.00 мм; ix=67.77 мм; iy=40.49 мм; r=15.00 мм; s=8.00 мм; t=13.00 мм; Вертикальный центроид=80.00 мм; Высота=160.00 мм; Горизонтальный центроид=80.00 мм; Номинальный вес=42.60 килограмм-сила/м; Носок полки сопряжения=19.00 мм; Носок ребра жесткости сопряжения=28.00 мм; Площадь сечения=54.3 см²; Сопряжение ребра жесткости=15.00 мм; Толщина полки=13.00 мм; Толщина ребра жесткости=8.00 мм; Чистая высота ребра жесткости=134.00 мм; Ширина=160.00 мм
- 16ДК3: ADSK_Масса на единицу длины=76.20 кг/м; Ix=5098.27 см4; Iy=1758.77 см4; Sx=337.3 см³; Sy=162.7 см³; Wx=566.5 см³; Wy=211.9 см³; b=166.00 мм; h=180.00 мм; ix=72.48 мм; iy=42.57 мм; r=15.00 мм; s=14.00 мм; t=23.00 мм; Вертикальный центроид=90.00 мм; Высота=180.00 мм; Горизонтальный центроид=83.00 мм; Номинальный вес=76.20 килограмм-сила/м; Носок полки сопряжения=22.00 мм; Носок ребра жесткости сопряжения=38.00 мм; Площадь сечения=97.1 см²; Сопряжение ребра жесткости=15.00 мм; Толщина полки=23.00 мм; Толщина ребра жесткости=14.00 мм; Чистая высота ребра жесткости=134.00 мм; Ширина=166.00 мм
- 18ДК0: ADSK_Масса на единицу длины=28.70 кг/м; Ix=1966.90 см4; Iy=723.97 см4; Sx=129.1 см³; Sy=61.8 см³; Wx=235.6 см³; Wy=81.1 см³; b=180.00 мм; h=167.00 мм; ix=73.38 мм; iy=44.70 мм; r=15.00 мм; s=5.00 мм; t=7.50 мм; Вертикальный центроид=83.50 мм; Высота=167.00 мм; Горизонтальный центроид=90.00 мм; Номинальный вес=28.70 килограмм-сила/м; Носок полки сопряжения=17.50 мм; Носок ребра жесткости сопряжения=22.50 мм; Площадь сечения=36.5 см²; Сопряжение ребра жесткости=15.00 мм; Толщина полки=7.50 мм; Толщина ребра жесткости=5.00 мм; Чистая высота ребра жесткости=152.00 мм; Ширина=180.00 мм
- 18ДК1: ADSK_Масса на единицу длины=35.50 кг/м; Ix=2510.29 см4; Iy=924.61 см4; Sx=162.4 см³; Sy=78.3 см³; Wx=293.6 см³; Wy=102.7 см³; b=180.00 мм; h=171.00 мм; ix=74.48 мм; iy=45.20 мм; r=15.00 мм; s=6.00 мм; t=9.50 мм; Вертикальный центроид=85.50 мм; Высота=171.00 мм; Горизонтальный центроид=90.00 мм; Номинальный вес=35.50 килограмм-сила/м; Носок полки сопряжения=18.00 мм; Носок ребра жесткости сопряжения=24.50 мм; Площадь сечения=45.3 см²; Сопряжение ребра жесткости=15.00 мм; Толщина полки=9.50 мм; Толщина ребра жесткости=6.00 мм; Чистая высота ребра жесткости=152.00 мм; Ширина=180.00 мм
- 18ДК2: ADSK_Масса на единицу длины=51.00 кг/м; Ix=3825.28 см4; Iy=1362.76 см4; Sx=240.2 см³; Sy=115.4 см³; Wx=425.0 см³; Wy=151.4 см³; b=180.00 мм; h=180.00 мм; ix=76.75 мм; iy=45.81 мм; r=15.00 мм; s=8.30 мм; t=14.00 мм; Вертикальный центроид=90.00 мм; Высота=180.00 мм; Горизонтальный центроид=90.00 мм; Номинальный вес=51.00 килограмм-сила/м; Носок полки сопряжения=19.15 мм; Носок ребра жесткости сопряжения=29.00 мм; Площадь сечения=65.0 см²; Сопряжение ребра жесткости=15.00 мм; Толщина полки=14.00 мм; Толщина ребра жесткости=8.30 мм; Чистая высота ребра жесткости=152.00 мм; Ширина=180.00 мм
- 18ДК3: ADSK_Масса на единицу длины=88.90 кг/м; Ix=7483.13 см4; Iy=2580.13 см4; Sx=441.7 см³; Sy=212.6 см³; Wx=748.3 см³; Wy=277.4 см³; b=186.00 мм; h=200.00 мм; ix=81.29 мм; iy=47.73 мм; r=15.00 мм; s=14.50 мм; t=24.00 мм; Вертикальный центроид=100.00 мм; Высота=200.00 мм; Горизонтальный центроид=93.00 мм; Номинальный вес=88.90 килограмм-сила/м; Носок полки сопряжения=22.25 мм; Носок ребра жесткости сопряжения=39.00 мм; Площадь сечения=113.3 см²; Сопряжение ребра жесткости=15.00 мм; Толщина полки=24.00 мм; Толщина ребра жесткости=14.50 мм; Чистая высота ребра жесткости=152.00 мм; Ширина=186.00 мм
- 20ДК1: ADSK_Масса на единицу длины=46.00 кг/м; Ix=4545.70 см4; Iy=1534.57 см4; Sx=247.8 см³; Sy=114.8 см³; Wx=447.9 см³; Wy=151.2 см³; b=203.00 мм; h=203.00 мм; ix=88.09 мм; iy=51.18 мм; r=10.20 мм; s=7.20 мм; t=11.00 мм; Вертикальный центроид=101.50 мм; Высота=203.00 мм; Горизонтальный центроид=101.50 мм; Номинальный вес=46.00 килограмм-сила/м; Носок полки сопряжения=13.80 мм; Носок ребра жесткости сопряжения=21.20 мм; Площадь сечения=58.6 см²; Сопряжение ребра жесткости=10.20 мм; Толщина полки=11.00 мм; Толщина ребра жесткости=7.20 мм; Чистая высота ребра жесткости=181.00 мм; Ширина=203.00 мм
- 20ДК2: ADSK_Масса на единицу длины=52.30 кг/м; Ix=5272.37 см4; Iy=1783.95 см4; Sx=284.8 см³; Sy=132.8 см³; Wx=511.9 см³; Wy=174.9 см³; b=204.00 мм; h=206.00 мм; ix=88.99 мм; iy=51.76 мм; r=10.20 мм; s=7.90 мм; t=12.60 мм; Вертикальный центроид=103.00 мм; Высота=206.00 мм; Горизонтальный центроид=102.00 мм; Номинальный вес=52.30 килограмм-сила/м; Носок полки сопряжения=14.15 мм; Носок ребра жесткости сопряжения=22.80 мм; Площадь сечения=66.6 см²; Сопряжение ребра жесткости=10.20 мм; Толщина полки=12.60 мм; Толщина ребра жесткости=7.90 мм; Чистая высота ребра жесткости=180.80 мм; Ширина=204.00 мм
- 20ДК3: ADSK_Масса на единицу длины=59.40 кг/м; Ix=6114.00 см4; Iy=2040.50 см4; Sx=326.5 см³; Sy=151.4 см³; Wx=582.3 см³; Wy=199.1 см³; b=205.00 мм; h=210.00 мм; ix=89.91 мм; iy=51.94 мм; r=10.20 мм; s=9.10 мм; t=14.20 мм; Вертикальный центроид=105.00 мм; Высота=210.00 мм; Горизонтальный центроид=102.50 мм; Номинальный вес=59.40 килограмм-сила/м; Носок полки сопряжения=14.75 мм; Носок ребра жесткости сопряжения=24.40 мм; Площадь сечения=75.6 см²; Сопряжение ребра жесткости=10.20 мм; Толщина полки=14.20 мм; Толщина ребра жесткости=9.10 мм; Чистая высота ребра жесткости=181.60 мм; Ширина=205.00 мм
- 20ДК4: ADSK_Масса на единицу длины=71.50 кг/м; Ix=7662.28 см4; Iy=2537.25 см4; Sx=401.7 см³; Sy=187.3 см³; Wx=709.5 см³; Wy=246.3 см³; b=206.00 мм; h=216.00 мм; ix=91.73 мм; iy=52.78 мм; r=10.20 мм; s=10.20 мм; t=17.40 мм; Вертикальный центроид=108.00 мм; Высота=216.00 мм; Горизонтальный центроид=103.00 мм; Номинальный вес=71.50 килограмм-сила/м; Носок полки сопряжения=15.30 мм; Носок ребра жесткости сопряжения=27.60 мм; Площадь сечения=91.1 см²; Сопряжение ребра жесткости=10.20 мм; Толщина полки=17.40 мм; Толщина ребра жесткости=10.20 мм; Чистая высота ребра жесткости=181.20 мм; Ширина=206.00 мм
- 20ДК5: ADSK_Масса на единицу длины=86.80 кг/м; Ix=9471.87 см4; Iy=3138.43 см4; Sx=490.6 см³; Sy=229.2 см³; Wx=853.3 см³; Wy=300.3 см³; b=209.00 мм; h=222.00 мм; ix=92.58 мм; iy=53.29 мм; r=10.20 мм; s=13.00 мм; t=20.60 мм; Вертикальный центроид=111.00 мм; Высота=222.00 мм; Горизонтальный центроид=104.50 мм; Номинальный вес=86.80 килограмм-сила/м; Носок полки сопряжения=16.70 мм; Носок ребра жесткости сопряжения=30.80 мм; Площадь сечения=110.5 см²; Сопряжение ребра жесткости=10.20 мм; Толщина полки=20.60 мм; Толщина ребра жесткости=13.00 мм; Чистая высота ребра жесткости=180.80 мм; Ширина=209.00 мм
- 20ДК6: ADSK_Масса на единицу длины=99.50 кг/м; Ix=11328.82 см4; Iy=3663.55 см4; Sx=574.6 см³; Sy=266.5 см³; Wx=989.4 см³; Wy=348.9 см³; b=210.00 мм; h=229.00 мм; ix=94.53 мм; iy=53.76 мм; r=10.20 мм; s=14.50 мм; t=23.70 мм; Вертикальный центроид=114.50 мм; Высота=229.00 мм; Горизонтальный центроид=105.00 мм; Номинальный вес=99.50 килограмм-сила/м; Носок полки сопряжения=17.45 мм; Носок ребра жесткости сопряжения=33.90 мм; Площадь сечения=126.8 см²; Сопряжение ребра жесткости=10.20 мм; Толщина полки=23.70 мм; Толщина ребра жесткости=14.50 мм; Чистая высота ребра жесткости=181.60 мм; Ширина=210.00 мм
- 25ДК1: ADSK_Масса на единицу длины=72.90 кг/м; Ix=11274.05 см4; Iy=3880.25 см4; Sx=492.5 см³; Sy=231.6 см³; Wx=891.2 см³; Wy=305.5 см³; b=254.00 мм; h=253.00 мм; ix=110.20 мм; iy=64.65 мм; r=12.70 мм; s=8.60 мм; t=14.20 мм; Вертикальный центроид=126.50 мм; Высота=253.00 мм; Горизонтальный центроид=127.00 мм; Номинальный вес=72.90 килограмм-сила/м; Носок полки сопряжения=17.00 мм; Носок ребра жесткости сопряжения=26.90 мм; Площадь сечения=92.8 см²; Сопряжение ребра жесткости=12.70 мм; Толщина полки=14.20 мм; Толщина ребра жесткости=8.60 мм; Чистая высота ребра жесткости=224.60 мм; Ширина=254.00 мм
- 25ДК2: ADSK_Масса на единицу длины=80.10 кг/м; Ix=12567.16 см4; Iy=4313.58 см4; Sx=545.1 см³; Sy=256.6 см³; Wx=981.8 см³; Wy=338.3 см³; b=255.00 мм; h=256.00 мм; ix=110.96 мм; iy=65.01 мм; r=12.70 мм; s=9.40 мм; t=15.60 мм; Вертикальный центроид=128.00 мм; Высота=256.00 мм; Горизонтальный центроид=127.50 мм; Номинальный вес=80.10 килограмм-сила/м; Носок полки сопряжения=17.40 мм; Носок ребра жесткости сопряжения=28.30 мм; Площадь сечения=102.1 см²; Сопряжение ребра жесткости=12.70 мм; Толщина полки=15.60 мм; Толщина ребра жесткости=9.40 мм; Чистая высота ребра жесткости=224.80 мм; Ширина=255.00 мм
- 25ДК3: ADSK_Масса на единицу длины=89.60 кг/м; Ix=14253.92 см4; Iy=4840.74 см4; Sx=613.0 см³; Sy=287.2 см³; Wx=1096.5 см³; Wy=378.2 см³; b=256.00 мм; h=260.00 мм; ix=111.78 мм; iy=65.14 мм; r=12.70 мм; s=10.70 мм; t=17.30 мм; Вертикальный центроид=130.00 мм; Высота=260.00 мм; Горизонтальный центроид=128.00 мм; Номинальный вес=89.60 килограмм-сила/м; Носок полки сопряжения=18.05 мм; Носок ребра жесткости сопряжения=30.00 мм; Площадь сечения=114.1 см²; Сопряжение ребра жесткости=12.70 мм; Толщина полки=17.30 мм; Толщина ребра жесткости=10.70 мм; Чистая высота ребра жесткости=225.40 мм; Ширина=256.00 мм
- 25ДК4: ADSK_Масса на единицу длины=101.20 кг/м; Ix=16369.03 см4; Iy=5549.34 см4; Sx=698.3 см³; Sy=328.2 см³; Wx=1240.1 см³; Wy=431.9 см³; b=257.00 мм; h=264.00 мм; ix=112.70 мм; iy=65.62 мм; r=12.70 мм; s=11.90 мм; t=19.60 мм; Вертикальный центроид=132.00 мм; Высота=264.00 мм; Горизонтальный центроид=128.50 мм; Номинальный вес=101.20 килограмм-сила/м; Носок полки сопряжения=18.65 мм; Носок ребра жесткости сопряжения=32.30 мм; Площадь сечения=128.9 см²; Сопряжение ребра жесткости=12.70 мм; Толщина полки=19.60 мм; Толщина ребра жесткости=11.90 мм; Чистая высота ребра жесткости=224.80 мм; Ширина=257.00 мм
- 25ДК5: ADSK_Масса на единицу длины=115.00 кг/м; Ix=18890.39 см4; Iy=6404.89 см4; Sx=797.6 см³; Sy=376.2 см³; Wx=1404.5 см³; Wy=494.6 см³; b=259.00 мм; h=269.00 мм; ix=113.80 мм; iy=66.30 мм; r=10.70 мм; s=13.50 мм; t=22.10 мм; Вертикальный центроид=134.50 мм; Высота=269.00 мм; Горизонтальный центроид=129.50 мм; Номинальный вес=115.00 килограмм-сила/м; Носок полки сопряжения=17.45 мм; Носок ребра жесткости сопряжения=32.80 мм; Площадь сечения=146.0 см²; Сопряжение ребра жесткости=10.70 мм; Толщина полки=22.10 мм; Толщина ребра жесткости=13.50 мм; Чистая высота ребра жесткости=224.80 мм; Ширина=259.00 мм
- 25ДК6: ADSK_Масса на единицу длины=131.00 кг/м; Ix=22101.48 см4; Iy=7445.67 см4; Sx=921.3 см³; Sy=434.6 см³; Wx=1607.4 см³; Wy=570.6 см³; b=261.00 мм; h=275.00 мм; ix=115.17 мм; iy=66.85 мм; r=10.70 мм; s=15.40 мм; t=25.10 мм; Вертикальный центроид=137.50 мм; Высота=275.00 мм; Горизонтальный центроид=130.50 мм; Номинальный вес=131.00 килограмм-сила/м; Носок полки сопряжения=18.40 мм; Носок ребра жесткости сопряжения=35.80 мм; Площадь сечения=167.0 см²; Сопряжение ребра жесткости=10.70 мм; Толщина полки=25.10 мм; Толщина ребра жесткости=15.40 мм; Чистая высота ребра жесткости=224.80 мм; Ширина=261.00 мм
- 25ДК7: ADSK_Масса на единицу длины=149.00 кг/м; Ix=25884.67 см4; Iy=8621.57 см4; Sx=1062.1 см³; Sy=500.1 см³; Wx=1835.8 см³; Wy=655.6 см³; b=263.00 мм; h=282.00 мм; ix=116.93 мм; iy=67.48 мм; r=10.70 мм; s=17.30 мм; t=28.40 мм; Вертикальный центроид=141.00 мм; Высота=282.00 мм; Горизонтальный центроид=131.50 мм; Номинальный вес=149.00 килограмм-сила/м; Носок полки сопряжения=19.35 мм; Носок ребра жесткости сопряжения=39.10 мм; Площадь сечения=190.0 см²; Сопряжение ребра жесткости=10.70 мм; Толщина полки=28.40 мм; Толщина ребра жесткости=17.30 мм; Чистая высота ребра жесткости=225.20 мм; Ширина=263.00 мм
- 25ДК8: ADSK_Масса на единицу длины=167.00 кг/м; Ix=29966.97 см4; Iy=9877.85 см4; Sx=1211.0 см³; Sy=569.2 см³; Wx=2073.8 см³; Wy=745.5 см³; b=265.00 мм; h=289.00 мм; ix=118.67 мм; iy=68.13 мм; r=10.70 мм; s=19.20 мм; t=31.80 мм; Вертикальный центроид=144.50 мм; Высота=289.00 мм; Горизонтальный центроид=132.50 мм; Номинальный вес=167.00 килограмм-сила/м; Носок полки сопряжения=20.30 мм; Носок ребра жесткости сопряжения=42.50 мм; Площадь сечения=212.0 см²; Сопряжение ребра жесткости=10.70 мм; Толщина полки=31.80 мм; Толщина ребра жесткости=19.20 мм; Чистая высота ребра жесткости=225.40 мм; Ширина=265.00 мм

note: column(s) folded — value = type name in every type: ADSK_Наименование, Номер профиля
